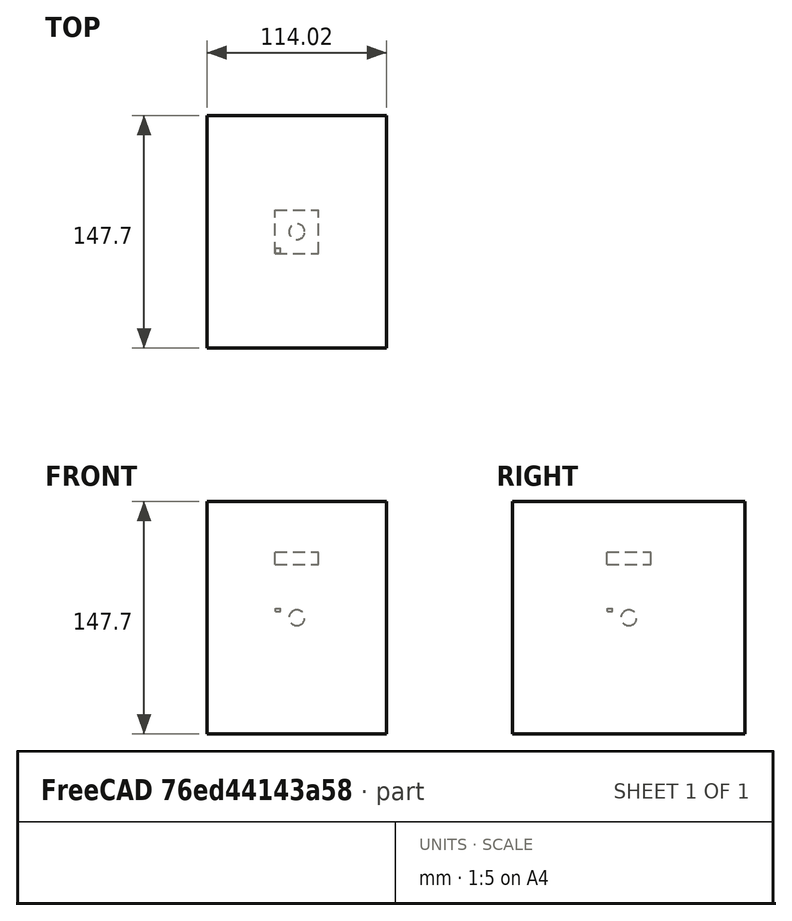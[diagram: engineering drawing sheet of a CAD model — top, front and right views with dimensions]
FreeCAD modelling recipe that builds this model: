
FCSTD DOCUMENT  (FreeCAD 0.20R29177 (Git))
Label: borderTest-1
License: All rights reserved
objects: App::DocumentObjectGroupPython×1272, Part::FeaturePython×7, App::Part×4, App::FeaturePython×1
note: 4 computed .brp shape members not serialized (recipe doc carries the construction recipe); baked Part::Feature solids carry a one-line shape summary decoded from their .brp

FEATURE [App::DocumentObjectGroupPython] HALFPI  # scripted group (container) (typed FeaturePython)
  name = HALFPI
  value = pi/2.
FEATURE [App::DocumentObjectGroupPython] PI  # scripted group (container) (typed FeaturePython)
  name = PI
  value = 1.*pi
FEATURE [App::DocumentObjectGroupPython] TWOPI  # scripted group (container) (typed FeaturePython)
  name = TWOPI
  value = 2.*pi
FEATURE [App::DocumentObjectGroupPython] Constants  # scripted group (container) (typed FeaturePython)
  Group = -> [HALFPI,PI,TWOPI]
FEATURE [App::DocumentObjectGroupPython] Variables  # scripted group (container) (typed FeaturePython)
FEATURE [App::DocumentObjectGroupPython] Quantities  # scripted group (container) (typed FeaturePython)
FEATURE [App::DocumentObjectGroupPython] Isotopes  # scripted group (container) (typed FeaturePython)
FEATURE [App::DocumentObjectGroupPython] Elements  # scripted group (container) (typed FeaturePython)
FEATURE [App::DocumentObjectGroupPython] G4_AIR  label="G4_AIR : 1.000"  # scripted group (container) (typed FeaturePython)
  n = 1
FEATURE [App::DocumentObjectGroupPython] Air  # scripted group (container) (typed FeaturePython)
  Dunit = mg/cm3
  Dvalue = 1.29
  Group = -> [G4_AIR]
  RINDEX = AirRINDEX
  conduct = 2
  density = 1
  expand = 3
  name = Air
  specific = 4
FEATURE [App::DocumentObjectGroupPython] SY  # scripted group (container) (typed FeaturePython)
  coldim = 1
  values = 100000/MeV
FEATURE [App::DocumentObjectGroupPython] RS  # scripted group (container) (typed FeaturePython)
  coldim = 1
  values = 1
FEATURE [App::DocumentObjectGroupPython] FTC  # scripted group (container) (typed FeaturePython)
  coldim = 1
  values = 21.5*ns
FEATURE [App::DocumentObjectGroupPython] STC  # scripted group (container) (typed FeaturePython)
  coldim = 1
  values = 43.8*ns
FEATURE [App::DocumentObjectGroupPython] RY1  # scripted group (container) (typed FeaturePython)
  coldim = 1
  values = 95
FEATURE [App::DocumentObjectGroupPython] RY2  # scripted group (container) (typed FeaturePython)
  coldim = 1
  values = 5
FEATURE [App::DocumentObjectGroupPython] YR  # scripted group (container) (typed FeaturePython)
  coldim = 1
  values = 0.8
FEATURE [App::DocumentObjectGroupPython] SCINTLAR  # scripted group (container) (typed FeaturePython)
  coldim = 2
  values = <blob: 2358 chars omitted>
FEATURE [App::DocumentObjectGroupPython] RINDEXLAR  # scripted group (container) (typed FeaturePython)
  coldim = 2
  values = <blob: 9384 chars omitted>
FEATURE [App::DocumentObjectGroupPython] ABSLENGTHLAR  # scripted group (container) (typed FeaturePython)
  coldim = 2
  values = 7.74901*eV 10.0*m 7.77525*eV 10.0*m 7.80167*eV 10.0*m 7.82827*eV 10.0*m 7.85506*eV 10.0*m 7.88202*eV 10.0*m 7.90917*eV 10.0*m 7.93651*eV 10.0*m 7.96404*eV 10.0*m 7.99176*eV 10.0*m 8.01968*eV 10.0*m 8.04779*eV 10.0*m 8.07609*eV 10.0*m 8.1046*eV 10.0*m 8.13331*eV 10.0*m 8.16222*eV 10.0*m 8.19134*eV 10.0*m 8.22067*eV 10.0*m 8.25021*eV 10.0*m 8.27996*eV 10.0*m 8.30993*eV 10.0*m 8.34012*eV 10.0*m 8.37052*eV 10.0*m 8.40115*eV 10.0*m 8.432*eV 10.0*m 8.46308*eV 10.0*m 8.4944*eV 10.0*m 8.52594*eV 10.0*m 8.55772*eV 10.0*m 8.58973*eV 10.0*m 8.62199*eV 10.0*m 8.65449*eV 10.0*m 8.68723*eV 10.0*m 8.72023*eV 10.0*m 8.75347*eV 10.0*m 8.78697*eV 10.0*m 8.82073*eV 10.0*m 8.85475*eV 10.0*m 8.88903*eV 10.0*m 8.92358*eV 10.0*m 8.9584*eV 10.0*m 8.99349*eV 10.0*m 9.02885*eV 10.0*m 9.0645*eV 10.0*m 9.10043*eV 10.0*m 9.13664*eV 10.0*m 9.17314*eV 10.0*m 9.20994*eV 10.0*m 9.24703*eV 10.0*m 9.28442*eV 10.0*m 9.32212*eV 10.0*m 9.36012*eV 10.0*m 9.39844*eV 10.0*m 9.43707*eV 10.0*m 9.47602*eV 10.0*m 9.51529*eV 10.0*m 9.55489*eV 10.0*m 9.59481*eV 10.0*m 9.63508*eV 10.0*m 9.67568*eV 10.0*m 9.71663*eV 10.0*m 9.75792*eV 10.0*m 9.79957*eV 10.0*m 9.84158*eV 10.0*m 9.88394*eV 10.0*m 9.92668*eV 10.0*m 9.96978*eV 10.0*m 10.0133*eV 10.0*m 10.0571*eV 10.0*m 10.1014*eV 10.0*m 10.146*eV 10.0*m 10.191*eV 10.0*m 10.2365*eV 10.0*m 10.2823*eV 10.0*m 10.3286*eV 10.0*m 10.3752*eV 10.0*m 10.4223*eV 10.0*m 10.4699*eV 10.0*m 10.5178*eV 10.0*m 10.5662*eV 10.0*m 10.6151*eV 10.0*m 10.6644*eV 10.0*m 10.7142*eV 10.0*m 10.7644*eV 10.0*m 10.8151*eV 10.0*m 10.8663*eV 10.0*m 10.9179*eV 10.0*m 10.9701*eV 10.0*m 11.0228*eV 10.0*m 11.076*eV 10.0*m 11.1296*eV 10.0*m 11.1839*eV 10.0*m 11.2386*eV 10.0*m 11.2939*eV 10.0*m 11.3497*eV 10.0*m 11.4061*eV 10.0*m 11.463*eV 10.0*m 11.5206*eV 10.0*m 11.5787*eV 10.0*m 11.6373*eV 10.0*m
FEATURE [App::DocumentObjectGroupPython] RAYLEIGHLAR  # scripted group (container) (typed FeaturePython)
  coldim = 2
  values = 7.74901*eV 90.0*cm 7.77525*eV 90.0*cm 7.80167*eV 90.0*cm 7.82827*eV 90.0*cm 7.85506*eV 90.0*cm 7.88202*eV 90.0*cm 7.90917*eV 90.0*cm 7.93651*eV 90.0*cm 7.96404*eV 90.0*cm 7.99176*eV 90.0*cm 8.01968*eV 90.0*cm 8.04779*eV 90.0*cm 8.07609*eV 90.0*cm 8.1046*eV 90.0*cm 8.13331*eV 90.0*cm 8.16222*eV 90.0*cm 8.19134*eV 90.0*cm 8.22067*eV 90.0*cm 8.25021*eV 90.0*cm 8.27996*eV 90.0*cm 8.30993*eV 90.0*cm 8.34012*eV 90.0*cm 8.37052*eV 90.0*cm 8.40115*eV 90.0*cm 8.432*eV 90.0*cm 8.46308*eV 90.0*cm 8.4944*eV 90.0*cm 8.52594*eV 90.0*cm 8.55772*eV 90.0*cm 8.58973*eV 90.0*cm 8.62199*eV 90.0*cm 8.65449*eV 90.0*cm 8.68723*eV 90.0*cm 8.72023*eV 90.0*cm 8.75347*eV 90.0*cm 8.78697*eV 90.0*cm 8.82073*eV 90.0*cm 8.85475*eV 90.0*cm 8.88903*eV 90.0*cm 8.92358*eV 90.0*cm 8.9584*eV 90.0*cm 8.99349*eV 90.0*cm 9.02885*eV 90.0*cm 9.0645*eV 90.0*cm 9.10043*eV 90.0*cm 9.13664*eV 90.0*cm 9.17314*eV 90.0*cm 9.20994*eV 90.0*cm 9.24703*eV 90.0*cm 9.28442*eV 90.0*cm 9.32212*eV 90.0*cm 9.36012*eV 90.0*cm 9.39844*eV 90.0*cm 9.43707*eV 90.0*cm 9.47602*eV 90.0*cm 9.51529*eV 90.0*cm 9.55489*eV 90.0*cm 9.59481*eV 90.0*cm 9.63508*eV 90.0*cm 9.67568*eV 90.0*cm 9.71663*eV 90.0*cm 9.75792*eV 90.0*cm 9.79957*eV 90.0*cm 9.84158*eV 90.0*cm 9.88394*eV 90.0*cm 9.92668*eV 90.0*cm 9.96978*eV 90.0*cm 10.0133*eV 90.0*cm 10.0571*eV 90.0*cm 10.1014*eV 90.0*cm 10.146*eV 90.0*cm 10.191*eV 90.0*cm 10.2365*eV 90.0*cm 10.2823*eV 90.0*cm 10.3286*eV 90.0*cm 10.3752*eV 90.0*cm 10.4223*eV 90.0*cm 10.4699*eV 90.0*cm 10.5178*eV 90.0*cm 10.5662*eV 90.0*cm 10.6151*eV 90.0*cm 10.6644*eV 90.0*cm 10.7142*eV 90.0*cm 10.7644*eV 90.0*cm 10.8151*eV 90.0*cm 10.8663*eV 90.0*cm 10.9179*eV 90.0*cm 10.9701*eV 90.0*cm 11.0228*eV 90.0*cm 11.076*eV 90.0*cm 11.1296*eV 90.0*cm 11.1839*eV 90.0*cm 11.2386*eV 90.0*cm 11.2939*eV 90.0*cm 11.3497*eV 90.0*cm 11.4061*eV 90.0*cm 11.463*eV 90.0*cm 11.5206*eV 90.0*cm 11.5787*eV 90.0*cm 11.6373*eV 90.0*cm
FEATURE [App::DocumentObjectGroupPython] REFLECTIVITY  # scripted group (container) (typed FeaturePython)
  coldim = 2
  values = 2.034*eV 0.98 2.068*eV 0.98 2.103*eV 0.98 2.139*eV 0.98 2.177*eV 0.98 2.216*eV 0.98 2.256*eV 0.98 2.298*eV 0.98 2.341*eV 0.98 2.386*eV 0.98 2.433*eV 0.98 2.481*eV 0.98 2.532*eV 0.98 2.585*eV 0.98 2.64*eV 0.98 2.697*eV 0.98 2.757*eV 0.98 2.82*eV 0.98 2.885*eV 0.98 2.954*eV 0.98 3.026*eV 0.98 3.102*eV 0.98 3.181*eV 0.98 3.265*eV 0.98 3.353*eV 0.98 3.446*eV 0.98 3.545*eV 0.98 3.649*eV 0.98 3.76*eV 0.98 3.877*eV 0.98 4.002*eV 0.98 4.136*eV 0.98 5.0*eV 0.98 6.0*eV 0.98 7.0*eV 0.98 8.0*eV 0.98 9.0*eV 0.98 9.0*eV 0.98 10.0*eV 0.98 11.0*eV 0.98 11.6*eV 0.98
FEATURE [App::DocumentObjectGroupPython] EFFICIENCY  # scripted group (container) (typed FeaturePython)
  coldim = 2
  values = 2.034*eV 1 2.068*eV 1 2.103*eV 1 2.139*eV 1 2.177*eV 1 2.216*eV 1 2.256*eV 1 2.298*eV 1 2.341*eV 1 2.386*eV 1 2.433*eV 1 2.481*eV 1 2.532*eV 1 2.585*eV 1 2.64*eV 1 2.697*eV 1 2.757*eV 1 2.82*eV 1 2.885*eV 1 2.954*eV 1 3.026*eV 1 3.102*eV 1 3.181*eV  1 3.265*eV 1 3.353*eV 1 3.446*eV 1 3.545*eV 1 3.649*eV 1 3.76*eV 1 3.877*eV 1 4.002*eV 1 4.136*eV 1 5.0*eV 1 6.0*eV 1 7.0*eV 1 8.0*eV 1 9.0*eV 1 9.0*eV 1 10.0*eV 1 11.0*eV 1 11.6*eV 1
FEATURE [App::DocumentObjectGroupPython] AirRINDEX  # scripted group (container) (typed FeaturePython)
  coldim = 2
  values = 2.034*eV 1 2.068*eV 1 2.103*eV 1 2.139*eV 1 2.177*eV 1 2.216*eV 1 2.256*eV 1 2.298*eV 1 2.341*eV 1 2.386*eV 1 2.433*eV 1 2.481*eV 1 2.532*eV 1 2.585*eV 1 2.64*eV 1 2.697*eV 1 2.757*eV 1 2.82*eV 1 2.885*eV 1 2.954*eV 1 3.026*eV 1 3.102*eV 1 3.181*eV 1 3.265*eV 1 3.353*eV 1 3.446*eV 1 3.545*eV 1 3.649*eV 1 3.76*eV 1 3.877*eV 1 4.002*eV 1 4.136*eV 1 5.0*eV 1 6.0*eV 1 7.0*eV 1 8.0*eV 1 9.0*eV 1 10.0*eV 1 11.0*eV 1 11.6*eV 1
FEATURE [App::DocumentObjectGroupPython] Matrix  # scripted group (container) (typed FeaturePython)
  Group = -> [SY,RS,FTC,STC,RY1,RY2,YR,SCINTLAR,RINDEXLAR,ABSLENGTHLAR,RAYLEIGHLAR,REFLECTIVITY,EFFICIENCY,AirRINDEX]
FEATURE [App::DocumentObjectGroupPython] ScintWrap  # scripted group (container) (typed FeaturePython)
  EFFICIENCY = EFFICIENCY
  REFLECTIVITY = REFLECTIVITY
  finish = 39
  model = 0
  type = 2
  value = 1
FEATURE [App::DocumentObjectGroupPython] Surfaces  # scripted group (container) (typed FeaturePython)
  Group = -> [ScintWrap]
FEATURE [App::DocumentObjectGroupPython] Opticals  # scripted group (container) (typed FeaturePython)
  Group = -> [Matrix,Surfaces]
FEATURE [App::DocumentObjectGroupPython] G4Isotopes  # scripted group (container) (typed FeaturePython)
FEATURE [App::DocumentObjectGroupPython] H_element  # scripted group (container) (typed FeaturePython)
  Z = 1
  atom_value = 1.008
  formula = H
  name = H_element
FEATURE [App::DocumentObjectGroupPython] He_element  # scripted group (container) (typed FeaturePython)
  Z = 2
  atom_value = 4.0026
  formula = He
  name = He_element
FEATURE [App::DocumentObjectGroupPython] Li_element  # scripted group (container) (typed FeaturePython)
  Z = 3
  atom_value = 6.94
  formula = Li
  name = Li_element
FEATURE [App::DocumentObjectGroupPython] Be_element  # scripted group (container) (typed FeaturePython)
  Z = 4
  atom_value = 9.01218
  formula = Be
  name = Be_element
FEATURE [App::DocumentObjectGroupPython] B_element  # scripted group (container) (typed FeaturePython)
  Z = 5
  atom_value = 10.81
  formula = B
  name = B_element
FEATURE [App::DocumentObjectGroupPython] C_element  # scripted group (container) (typed FeaturePython)
  Z = 6
  atom_value = 12.011
  formula = C
  name = C_element
FEATURE [App::DocumentObjectGroupPython] N_element  # scripted group (container) (typed FeaturePython)
  Z = 7
  atom_value = 14.007
  formula = N
  name = N_element
FEATURE [App::DocumentObjectGroupPython] O_element  # scripted group (container) (typed FeaturePython)
  Z = 8
  atom_value = 15.999
  formula = O
  name = O_element
FEATURE [App::DocumentObjectGroupPython] F_element  # scripted group (container) (typed FeaturePython)
  Z = 9
  atom_value = 18.9984
  formula = F
  name = F_element
FEATURE [App::DocumentObjectGroupPython] Ne_element  # scripted group (container) (typed FeaturePython)
  Z = 10
  atom_value = 20.1797
  formula = Ne
  name = Ne_element
FEATURE [App::DocumentObjectGroupPython] Na_element  # scripted group (container) (typed FeaturePython)
  Z = 11
  atom_value = 22.9898
  formula = Na
  name = Na_element
FEATURE [App::DocumentObjectGroupPython] Mg_element  # scripted group (container) (typed FeaturePython)
  Z = 12
  atom_value = 24.305
  formula = Mg
  name = Mg_element
FEATURE [App::DocumentObjectGroupPython] Al_element  # scripted group (container) (typed FeaturePython)
  Z = 13
  atom_value = 26.9815
  formula = Al
  name = Al_element
FEATURE [App::DocumentObjectGroupPython] Si_element  # scripted group (container) (typed FeaturePython)
  Z = 14
  atom_value = 28.085
  formula = Si
  name = Si_element
FEATURE [App::DocumentObjectGroupPython] P_element  # scripted group (container) (typed FeaturePython)
  Z = 15
  atom_value = 30.9738
  formula = P
  name = P_element
FEATURE [App::DocumentObjectGroupPython] S_element  # scripted group (container) (typed FeaturePython)
  Z = 16
  atom_value = 32.06
  formula = S
  name = S_element
FEATURE [App::DocumentObjectGroupPython] Cl_element  # scripted group (container) (typed FeaturePython)
  Z = 17
  atom_value = 35.45
  formula = Cl
  name = Cl_element
FEATURE [App::DocumentObjectGroupPython] Ar_element  # scripted group (container) (typed FeaturePython)
  Z = 18
  atom_value = 39.95
  formula = Ar
  name = Ar_element
FEATURE [App::DocumentObjectGroupPython] K_element  # scripted group (container) (typed FeaturePython)
  Z = 19
  atom_value = 39.0983
  formula = K
  name = K_element
FEATURE [App::DocumentObjectGroupPython] Ca_element  # scripted group (container) (typed FeaturePython)
  Z = 20
  atom_value = 40.078
  formula = Ca
  name = Ca_element
FEATURE [App::DocumentObjectGroupPython] Sc_element  # scripted group (container) (typed FeaturePython)
  Z = 21
  atom_value = 44.9559
  formula = Sc
  name = Sc_element
FEATURE [App::DocumentObjectGroupPython] Ti_element  # scripted group (container) (typed FeaturePython)
  Z = 22
  atom_value = 47.867
  formula = Ti
  name = Ti_element
FEATURE [App::DocumentObjectGroupPython] V_element  # scripted group (container) (typed FeaturePython)
  Z = 23
  atom_value = 50.9415
  formula = V
  name = V_element
FEATURE [App::DocumentObjectGroupPython] Cr_element  # scripted group (container) (typed FeaturePython)
  Z = 24
  atom_value = 51.9961
  formula = Cr
  name = Cr_element
FEATURE [App::DocumentObjectGroupPython] Mn_element  # scripted group (container) (typed FeaturePython)
  Z = 25
  atom_value = 54.938
  formula = Mn
  name = Mn_element
FEATURE [App::DocumentObjectGroupPython] Fe_element  # scripted group (container) (typed FeaturePython)
  Z = 26
  atom_value = 55.845
  formula = Fe
  name = Fe_element
FEATURE [App::DocumentObjectGroupPython] Co_element  # scripted group (container) (typed FeaturePython)
  Z = 27
  atom_value = 58.9332
  formula = Co
  name = Co_element
FEATURE [App::DocumentObjectGroupPython] Ni_element  # scripted group (container) (typed FeaturePython)
  Z = 28
  atom_value = 58.6934
  formula = Ni
  name = Ni_element
FEATURE [App::DocumentObjectGroupPython] Cu_element  # scripted group (container) (typed FeaturePython)
  Z = 29
  atom_value = 63.546
  formula = Cu
  name = Cu_element
FEATURE [App::DocumentObjectGroupPython] Zn_element  # scripted group (container) (typed FeaturePython)
  Z = 30
  atom_value = 65.38
  formula = Zn
  name = Zn_element
FEATURE [App::DocumentObjectGroupPython] Ga_element  # scripted group (container) (typed FeaturePython)
  Z = 31
  atom_value = 69.723
  formula = Ga
  name = Ga_element
FEATURE [App::DocumentObjectGroupPython] Ge_element  # scripted group (container) (typed FeaturePython)
  Z = 32
  atom_value = 72.63
  formula = Ge
  name = Ge_element
FEATURE [App::DocumentObjectGroupPython] As_element  # scripted group (container) (typed FeaturePython)
  Z = 33
  atom_value = 74.9216
  formula = As
  name = As_element
FEATURE [App::DocumentObjectGroupPython] Se_element  # scripted group (container) (typed FeaturePython)
  Z = 34
  atom_value = 78.971
  formula = Se
  name = Se_element
FEATURE [App::DocumentObjectGroupPython] Br_element  # scripted group (container) (typed FeaturePython)
  Z = 35
  atom_value = 79.904
  formula = Br
  name = Br_element
FEATURE [App::DocumentObjectGroupPython] Kr_element  # scripted group (container) (typed FeaturePython)
  Z = 36
  atom_value = 83.798
  formula = Kr
  name = Kr_element
FEATURE [App::DocumentObjectGroupPython] Rb_element  # scripted group (container) (typed FeaturePython)
  Z = 37
  atom_value = 85.4678
  formula = Rb
  name = Rb_element
FEATURE [App::DocumentObjectGroupPython] Sr_element  # scripted group (container) (typed FeaturePython)
  Z = 38
  atom_value = 87.62
  formula = Sr
  name = Sr_element
FEATURE [App::DocumentObjectGroupPython] Y_element  # scripted group (container) (typed FeaturePython)
  Z = 39
  atom_value = 88.9058
  formula = Y
  name = Y_element
FEATURE [App::DocumentObjectGroupPython] Zr_element  # scripted group (container) (typed FeaturePython)
  Z = 40
  atom_value = 91.224
  formula = Zr
  name = Zr_element
FEATURE [App::DocumentObjectGroupPython] Nb_element  # scripted group (container) (typed FeaturePython)
  Z = 41
  atom_value = 92.9064
  formula = Nb
  name = Nb_element
FEATURE [App::DocumentObjectGroupPython] Mo_element  # scripted group (container) (typed FeaturePython)
  Z = 42
  atom_value = 95.95
  formula = Mo
  name = Mo_element
FEATURE [App::DocumentObjectGroupPython] Tc_element  # scripted group (container) (typed FeaturePython)
  Z = 43
  atom_value = 97
  formula = Tc
  name = Tc_element
FEATURE [App::DocumentObjectGroupPython] Ru_element  # scripted group (container) (typed FeaturePython)
  Z = 44
  atom_value = 101.07
  formula = Ru
  name = Ru_element
FEATURE [App::DocumentObjectGroupPython] Rh_element  # scripted group (container) (typed FeaturePython)
  Z = 45
  atom_value = 102.905
  formula = Rh
  name = Rh_element
FEATURE [App::DocumentObjectGroupPython] Pd_element  # scripted group (container) (typed FeaturePython)
  Z = 46
  atom_value = 106.42
  formula = Pd
  name = Pd_element
FEATURE [App::DocumentObjectGroupPython] Ag_element  # scripted group (container) (typed FeaturePython)
  Z = 47
  atom_value = 107.868
  formula = Ag
  name = Ag_element
FEATURE [App::DocumentObjectGroupPython] Cd_element  # scripted group (container) (typed FeaturePython)
  Z = 48
  atom_value = 112.414
  formula = Cd
  name = Cd_element
FEATURE [App::DocumentObjectGroupPython] In_element  # scripted group (container) (typed FeaturePython)
  Z = 49
  atom_value = 114.818
  formula = In
  name = In_element
FEATURE [App::DocumentObjectGroupPython] Sn_element  # scripted group (container) (typed FeaturePython)
  Z = 50
  atom_value = 118.71
  formula = Sn
  name = Sn_element
FEATURE [App::DocumentObjectGroupPython] Sb_element  # scripted group (container) (typed FeaturePython)
  Z = 51
  atom_value = 121.76
  formula = Sb
  name = Sb_element
FEATURE [App::DocumentObjectGroupPython] Te_element  # scripted group (container) (typed FeaturePython)
  Z = 52
  atom_value = 127.6
  formula = Te
  name = Te_element
FEATURE [App::DocumentObjectGroupPython] I_element  # scripted group (container) (typed FeaturePython)
  Z = 53
  atom_value = 126.904
  formula = I
  name = I_element
FEATURE [App::DocumentObjectGroupPython] Xe_element  # scripted group (container) (typed FeaturePython)
  Z = 54
  atom_value = 131.293
  formula = Xe
  name = Xe_element
FEATURE [App::DocumentObjectGroupPython] Cs_element  # scripted group (container) (typed FeaturePython)
  Z = 55
  atom_value = 132.905
  formula = Cs
  name = Cs_element
FEATURE [App::DocumentObjectGroupPython] Ba_element  # scripted group (container) (typed FeaturePython)
  Z = 56
  atom_value = 137.327
  formula = Ba
  name = Ba_element
FEATURE [App::DocumentObjectGroupPython] La_element  # scripted group (container) (typed FeaturePython)
  Z = 57
  atom_value = 138.905
  formula = La
  name = La_element
FEATURE [App::DocumentObjectGroupPython] Ce_element  # scripted group (container) (typed FeaturePython)
  Z = 58
  atom_value = 140.116
  formula = Ce
  name = Ce_element
FEATURE [App::DocumentObjectGroupPython] Pr_element  # scripted group (container) (typed FeaturePython)
  Z = 59
  atom_value = 140.908
  formula = Pr
  name = Pr_element
FEATURE [App::DocumentObjectGroupPython] Nd_element  # scripted group (container) (typed FeaturePython)
  Z = 60
  atom_value = 144.242
  formula = Nd
  name = Nd_element
FEATURE [App::DocumentObjectGroupPython] Pm_element  # scripted group (container) (typed FeaturePython)
  Z = 61
  atom_value = 145
  formula = Pm
  name = Pm_element
FEATURE [App::DocumentObjectGroupPython] Sm_element  # scripted group (container) (typed FeaturePython)
  Z = 62
  atom_value = 150.36
  formula = Sm
  name = Sm_element
FEATURE [App::DocumentObjectGroupPython] Eu_element  # scripted group (container) (typed FeaturePython)
  Z = 63
  atom_value = 151.964
  formula = Eu
  name = Eu_element
FEATURE [App::DocumentObjectGroupPython] Gd_element  # scripted group (container) (typed FeaturePython)
  Z = 64
  atom_value = 157.25
  formula = Gd
  name = Gd_element
FEATURE [App::DocumentObjectGroupPython] Tb_element  # scripted group (container) (typed FeaturePython)
  Z = 65
  atom_value = 158.925
  formula = Tb
  name = Tb_element
FEATURE [App::DocumentObjectGroupPython] Dy_element  # scripted group (container) (typed FeaturePython)
  Z = 66
  atom_value = 162.5
  formula = Dy
  name = Dy_element
FEATURE [App::DocumentObjectGroupPython] Ho_element  # scripted group (container) (typed FeaturePython)
  Z = 67
  atom_value = 164.93
  formula = Ho
  name = Ho_element
FEATURE [App::DocumentObjectGroupPython] Er_element  # scripted group (container) (typed FeaturePython)
  Z = 68
  atom_value = 167.259
  formula = Er
  name = Er_element
FEATURE [App::DocumentObjectGroupPython] Tm_element  # scripted group (container) (typed FeaturePython)
  Z = 69
  atom_value = 168.934
  formula = Tm
  name = Tm_element
FEATURE [App::DocumentObjectGroupPython] Yb_element  # scripted group (container) (typed FeaturePython)
  Z = 70
  atom_value = 173.045
  formula = Yb
  name = Yb_element
FEATURE [App::DocumentObjectGroupPython] Lu_element  # scripted group (container) (typed FeaturePython)
  Z = 71
  atom_value = 174.967
  formula = Lu
  name = Lu_element
FEATURE [App::DocumentObjectGroupPython] Hf_element  # scripted group (container) (typed FeaturePython)
  Z = 72
  atom_value = 178.49
  formula = Hf
  name = Hf_element
FEATURE [App::DocumentObjectGroupPython] Ta_element  # scripted group (container) (typed FeaturePython)
  Z = 73
  atom_value = 180.948
  formula = Ta
  name = Ta_element
FEATURE [App::DocumentObjectGroupPython] W_element  # scripted group (container) (typed FeaturePython)
  Z = 74
  atom_value = 183.84
  formula = W
  name = W_element
FEATURE [App::DocumentObjectGroupPython] Re_element  # scripted group (container) (typed FeaturePython)
  Z = 75
  atom_value = 186.207
  formula = Re
  name = Re_element
FEATURE [App::DocumentObjectGroupPython] Os_element  # scripted group (container) (typed FeaturePython)
  Z = 76
  atom_value = 190.23
  formula = Os
  name = Os_element
FEATURE [App::DocumentObjectGroupPython] Ir_element  # scripted group (container) (typed FeaturePython)
  Z = 77
  atom_value = 192.217
  formula = Ir
  name = Ir_element
FEATURE [App::DocumentObjectGroupPython] Pt_element  # scripted group (container) (typed FeaturePython)
  Z = 78
  atom_value = 195.084
  formula = Pt
  name = Pt_element
FEATURE [App::DocumentObjectGroupPython] Au_element  # scripted group (container) (typed FeaturePython)
  Z = 79
  atom_value = 196.967
  formula = Au
  name = Au_element
FEATURE [App::DocumentObjectGroupPython] Hg_element  # scripted group (container) (typed FeaturePython)
  Z = 80
  atom_value = 200.592
  formula = Hg
  name = Hg_element
FEATURE [App::DocumentObjectGroupPython] Tl_element  # scripted group (container) (typed FeaturePython)
  Z = 81
  atom_value = 204.38
  formula = Tl
  name = Tl_element
FEATURE [App::DocumentObjectGroupPython] Pb_element  # scripted group (container) (typed FeaturePython)
  Z = 82
  atom_value = 207.2
  formula = Pb
  name = Pb_element
FEATURE [App::DocumentObjectGroupPython] Bi_element  # scripted group (container) (typed FeaturePython)
  Z = 83
  atom_value = 208.98
  formula = Bi
  name = Bi_element
FEATURE [App::DocumentObjectGroupPython] Po_element  # scripted group (container) (typed FeaturePython)
  Z = 84
  atom_value = 209
  formula = Po
  name = Po_element
FEATURE [App::DocumentObjectGroupPython] At_element  # scripted group (container) (typed FeaturePython)
  Z = 85
  atom_value = 210
  formula = At
  name = At_element
FEATURE [App::DocumentObjectGroupPython] Rn_element  # scripted group (container) (typed FeaturePython)
  Z = 86
  atom_value = 222
  formula = Rn
  name = Rn_element
FEATURE [App::DocumentObjectGroupPython] Fr_element  # scripted group (container) (typed FeaturePython)
  Z = 87
  atom_value = 223
  formula = Fr
  name = Fr_element
FEATURE [App::DocumentObjectGroupPython] Ra_element  # scripted group (container) (typed FeaturePython)
  Z = 88
  atom_value = 226
  formula = Ra
  name = Ra_element
FEATURE [App::DocumentObjectGroupPython] Ac_element  # scripted group (container) (typed FeaturePython)
  Z = 89
  atom_value = 227
  formula = Ac
  name = Ac_element
FEATURE [App::DocumentObjectGroupPython] Th_element  # scripted group (container) (typed FeaturePython)
  Z = 90
  atom_value = 232.038
  formula = Th
  name = Th_element
FEATURE [App::DocumentObjectGroupPython] Pa_element  # scripted group (container) (typed FeaturePython)
  Z = 91
  atom_value = 231.036
  formula = Pa
  name = Pa_element
FEATURE [App::DocumentObjectGroupPython] U_element  # scripted group (container) (typed FeaturePython)
  Z = 92
  atom_value = 238.029
  formula = U
  name = U_element
FEATURE [App::DocumentObjectGroupPython] Np_element  # scripted group (container) (typed FeaturePython)
  Z = 93
  atom_value = 237
  formula = Np
  name = Np_element
FEATURE [App::DocumentObjectGroupPython] Pu_element  # scripted group (container) (typed FeaturePython)
  Z = 94
  atom_value = 244
  formula = Pu
  name = Pu_element
FEATURE [App::DocumentObjectGroupPython] Am_element  # scripted group (container) (typed FeaturePython)
  Z = 95
  atom_value = 243
  formula = Am
  name = Am_element
FEATURE [App::DocumentObjectGroupPython] Cm_element  # scripted group (container) (typed FeaturePython)
  Z = 96
  atom_value = 247
  formula = Cm
  name = Cm_element
FEATURE [App::DocumentObjectGroupPython] Bk_element  # scripted group (container) (typed FeaturePython)
  Z = 97
  atom_value = 247
  formula = Bk
  name = Bk_element
FEATURE [App::DocumentObjectGroupPython] Cf_element  # scripted group (container) (typed FeaturePython)
  Z = 98
  atom_value = 251
  formula = Cf
  name = Cf_element
FEATURE [App::DocumentObjectGroupPython] G4Elements  # scripted group (container) (typed FeaturePython)
  Group = -> [H_element,He_element,Li_element,Be_element,B_element,C_element,N_element,O_element,F_element,Ne_element,Na_element,Mg_element,Al_element,Si_element,P_element,S_element,Cl_element,Ar_element,K_element,Ca_element,Sc_element,Ti_element,V_element,Cr_element,Mn_element,Fe_element,Co_element,Ni_element,Cu_element,Zn_element,Ga_element,Ge_element,As_element,Se_element,Br_element,Kr_element,Rb_element,+61 more]
FEATURE [App::DocumentObjectGroupPython] H_element001  label="H_element : 0.101"  # scripted group (container) (typed FeaturePython)
  n = 0.101327
FEATURE [App::DocumentObjectGroupPython] C_element001  label="C_element : 0.775"  # scripted group (container) (typed FeaturePython)
  n = 0.7755
FEATURE [App::DocumentObjectGroupPython] N_element001  label="N_element : 0.035"  # scripted group (container) (typed FeaturePython)
  n = 0.035057
FEATURE [App::DocumentObjectGroupPython] O_element001  label="O_element : 0.052"  # scripted group (container) (typed FeaturePython)
  n = 0.0523159
FEATURE [App::DocumentObjectGroupPython] F_element001  label="F_element : 0.017"  # scripted group (container) (typed FeaturePython)
  n = 0.017422
FEATURE [App::DocumentObjectGroupPython] Ca_element001  label="Ca_element : 0.018"  # scripted group (container) (typed FeaturePython)
  n = 0.018378
FEATURE [App::DocumentObjectGroupPython] G4_A_150_TISSUE  label="G4_A-150_TISSUE"  # scripted group (container) (typed FeaturePython)
  Dunit = g/cm3
  Dvalue = 1.127
  Group = -> [H_element001,C_element001,N_element001,O_element001,F_element001,Ca_element001]
  conduct = 2
  density = 1
  expand = 3
  formula = G4_A-150_TISSUE
  name = G4_A-150_TISSUE
  specific = 4
FEATURE [App::DocumentObjectGroupPython] C_element002  label="C_element : 3"  # scripted group (container) (typed FeaturePython)
  n = 3
  ref = C_element
FEATURE [App::DocumentObjectGroupPython] H_element002  label="H_element : 6"  # scripted group (container) (typed FeaturePython)
  n = 6
  ref = H_element
FEATURE [App::DocumentObjectGroupPython] O_element002  label="O_element : 1"  # scripted group (container) (typed FeaturePython)
  n = 1
  ref = O_element
FEATURE [App::DocumentObjectGroupPython] G4_ACETONE  # scripted group (container) (typed FeaturePython)
  Dunit = g/cm3
  Dvalue = 0.7899
  Group = -> [C_element002,H_element002,O_element002]
  conduct = 2
  density = 1
  expand = 3
  formula = G4_ACETONE
  name = G4_ACETONE
  specific = 4
FEATURE [App::DocumentObjectGroupPython] C_element003  label="C_element : 2"  # scripted group (container) (typed FeaturePython)
  n = 2
  ref = C_element
FEATURE [App::DocumentObjectGroupPython] H_element003  label="H_element : 2"  # scripted group (container) (typed FeaturePython)
  n = 2
  ref = H_element
FEATURE [App::DocumentObjectGroupPython] G4_ACETYLENE  # scripted group (container) (typed FeaturePython)
  Dunit = g/cm3
  Dvalue = 0.0010967
  Group = -> [C_element003,H_element003]
  conduct = 2
  density = 1
  expand = 3
  formula = G4_ACETYLENE
  name = G4_ACETYLENE
  specific = 4
FEATURE [App::DocumentObjectGroupPython] C_element004  label="C_element : 5"  # scripted group (container) (typed FeaturePython)
  n = 5
  ref = C_element
FEATURE [App::DocumentObjectGroupPython] H_element004  label="H_element : 5"  # scripted group (container) (typed FeaturePython)
  n = 5
  ref = H_element
FEATURE [App::DocumentObjectGroupPython] N_element002  label="N_element : 5"  # scripted group (container) (typed FeaturePython)
  n = 5
  ref = N_element
FEATURE [App::DocumentObjectGroupPython] G4_ADENINE  # scripted group (container) (typed FeaturePython)
  Dunit = g/cm3
  Dvalue = 1.6
  Group = -> [C_element004,H_element004,N_element002]
  conduct = 2
  density = 1
  expand = 3
  formula = G4_ADENINE
  name = G4_ADENINE
  specific = 4
FEATURE [App::DocumentObjectGroupPython] H_element005  label="H_element : 0.114"  # scripted group (container) (typed FeaturePython)
  n = 0.114
FEATURE [App::DocumentObjectGroupPython] C_element005  label="C_element : 0.598"  # scripted group (container) (typed FeaturePython)
  n = 0.598
FEATURE [App::DocumentObjectGroupPython] N_element003  label="N_element : 0.007"  # scripted group (container) (typed FeaturePython)
  n = 0.007
FEATURE [App::DocumentObjectGroupPython] O_element003  label="O_element : 0.278"  # scripted group (container) (typed FeaturePython)
  n = 0.278
FEATURE [App::DocumentObjectGroupPython] Na_element001  label="Na_element : 0.001"  # scripted group (container) (typed FeaturePython)
  n = 0.001
FEATURE [App::DocumentObjectGroupPython] S_element001  label="S_element : 0.001"  # scripted group (container) (typed FeaturePython)
  n = 0.001
FEATURE [App::DocumentObjectGroupPython] Cl_element001  label="Cl_element : 0.001"  # scripted group (container) (typed FeaturePython)
  n = 0.001
FEATURE [App::DocumentObjectGroupPython] G4_ADIPOSE_TISSUE_ICRP  # scripted group (container) (typed FeaturePython)
  Dunit = g/cm3
  Dvalue = 0.95
  Group = -> [H_element005,C_element005,N_element003,O_element003,Na_element001,S_element001,Cl_element001]
  conduct = 2
  density = 1
  expand = 3
  formula = G4_ADIPOSE_TISSUE_ICRP
  name = G4_ADIPOSE_TISSUE_ICRP
  specific = 4
FEATURE [App::DocumentObjectGroupPython] C_element006  label="C_element : 0.000"  # scripted group (container) (typed FeaturePython)
  n = 0.000124
FEATURE [App::DocumentObjectGroupPython] N_element004  label="N_element : 0.755"  # scripted group (container) (typed FeaturePython)
  n = 0.755268
FEATURE [App::DocumentObjectGroupPython] O_element004  label="O_element : 0.232"  # scripted group (container) (typed FeaturePython)
  n = 0.231781
FEATURE [App::DocumentObjectGroupPython] Ar_element001  label="Ar_element : 0.013"  # scripted group (container) (typed FeaturePython)
  n = 0.012827
FEATURE [App::DocumentObjectGroupPython] G4_AIR001  label="G4_AIR"  # scripted group (container) (typed FeaturePython)
  Dunit = g/cm3
  Dvalue = 0.00120479
  Group = -> [C_element006,N_element004,O_element004,Ar_element001]
  conduct = 2
  density = 1
  expand = 3
  formula = G4_AIR
  name = G4_AIR
  specific = 4
FEATURE [App::DocumentObjectGroupPython] C_element007  label="C_element : 006"  # scripted group (container) (typed FeaturePython)
  n = 3
  ref = C_element
FEATURE [App::DocumentObjectGroupPython] H_element006  label="H_element : 7"  # scripted group (container) (typed FeaturePython)
  n = 7
  ref = H_element
FEATURE [App::DocumentObjectGroupPython] N_element005  label="N_element : 1"  # scripted group (container) (typed FeaturePython)
  n = 1
  ref = N_element
FEATURE [App::DocumentObjectGroupPython] O_element005  label="O_element : 2"  # scripted group (container) (typed FeaturePython)
  n = 2
  ref = O_element
FEATURE [App::DocumentObjectGroupPython] G4_ALANINE  # scripted group (container) (typed FeaturePython)
  Dunit = g/cm3
  Dvalue = 1.42
  Group = -> [C_element007,H_element006,N_element005,O_element005]
  conduct = 2
  density = 1
  expand = 3
  formula = G4_ALANINE
  name = G4_ALANINE
  specific = 4
FEATURE [App::DocumentObjectGroupPython] Al_element001  label="Al_element : 2"  # scripted group (container) (typed FeaturePython)
  n = 2
  ref = Al_element
FEATURE [App::DocumentObjectGroupPython] O_element006  label="O_element : 3"  # scripted group (container) (typed FeaturePython)
  n = 3
  ref = O_element
FEATURE [App::DocumentObjectGroupPython] G4_ALUMINUM_OXIDE  # scripted group (container) (typed FeaturePython)
  Dunit = g/cm3
  Dvalue = 3.97
  Group = -> [Al_element001,O_element006]
  conduct = 2
  density = 1
  expand = 3
  formula = G4_ALUMINUM_OXIDE
  name = G4_ALUMINUM_OXIDE
  specific = 4
FEATURE [App::DocumentObjectGroupPython] H_element007  label="H_element : 0.106"  # scripted group (container) (typed FeaturePython)
  n = 0.10593
FEATURE [App::DocumentObjectGroupPython] C_element008  label="C_element : 0.789"  # scripted group (container) (typed FeaturePython)
  n = 0.788974
FEATURE [App::DocumentObjectGroupPython] O_element007  label="O_element : 0.105"  # scripted group (container) (typed FeaturePython)
  n = 0.105096
FEATURE [App::DocumentObjectGroupPython] G4_AMBER  # scripted group (container) (typed FeaturePython)
  Dunit = g/cm3
  Dvalue = 1.1
  Group = -> [H_element007,C_element008,O_element007]
  conduct = 2
  density = 1
  expand = 3
  formula = G4_AMBER
  name = G4_AMBER
  specific = 4
FEATURE [App::DocumentObjectGroupPython] N_element006  label="N_element : 006"  # scripted group (container) (typed FeaturePython)
  n = 1
  ref = N_element
FEATURE [App::DocumentObjectGroupPython] H_element008  label="H_element : 3"  # scripted group (container) (typed FeaturePython)
  n = 3
  ref = H_element
FEATURE [App::DocumentObjectGroupPython] G4_AMMONIA  # scripted group (container) (typed FeaturePython)
  Dunit = g/cm3
  Dvalue = 0.000826019
  Group = -> [N_element006,H_element008]
  conduct = 2
  density = 1
  expand = 3
  formula = G4_AMMONIA
  name = G4_AMMONIA
  specific = 4
FEATURE [App::DocumentObjectGroupPython] C_element009  label="C_element : 6"  # scripted group (container) (typed FeaturePython)
  n = 6
  ref = C_element
FEATURE [App::DocumentObjectGroupPython] H_element009  label="H_element : 008"  # scripted group (container) (typed FeaturePython)
  n = 7
  ref = H_element
FEATURE [App::DocumentObjectGroupPython] N_element007  label="N_element : 007"  # scripted group (container) (typed FeaturePython)
  n = 1
  ref = N_element
FEATURE [App::DocumentObjectGroupPython] G4_ANILINE  # scripted group (container) (typed FeaturePython)
  Dunit = g/cm3
  Dvalue = 1.0235
  Group = -> [C_element009,H_element009,N_element007]
  conduct = 2
  density = 1
  expand = 3
  formula = G4_ANILINE
  name = G4_ANILINE
  specific = 4
FEATURE [App::DocumentObjectGroupPython] C_element010  label="C_element : 14"  # scripted group (container) (typed FeaturePython)
  n = 14
  ref = C_element
FEATURE [App::DocumentObjectGroupPython] H_element010  label="H_element : 10"  # scripted group (container) (typed FeaturePython)
  n = 10
  ref = H_element
FEATURE [App::DocumentObjectGroupPython] G4_ANTHRACENE  # scripted group (container) (typed FeaturePython)
  Dunit = g/cm3
  Dvalue = 1.283
  Group = -> [C_element010,H_element010]
  conduct = 2
  density = 1
  expand = 3
  formula = G4_ANTHRACENE
  name = G4_ANTHRACENE
  specific = 4
FEATURE [App::DocumentObjectGroupPython] H_element011  label="H_element : 0.065"  # scripted group (container) (typed FeaturePython)
  n = 0.0654709
FEATURE [App::DocumentObjectGroupPython] C_element011  label="C_element : 0.537"  # scripted group (container) (typed FeaturePython)
  n = 0.536944
FEATURE [App::DocumentObjectGroupPython] N_element008  label="N_element : 0.021"  # scripted group (container) (typed FeaturePython)
  n = 0.0215
FEATURE [App::DocumentObjectGroupPython] O_element008  label="O_element : 0.032"  # scripted group (container) (typed FeaturePython)
  n = 0.032085
FEATURE [App::DocumentObjectGroupPython] F_element002  label="F_element : 0.167"  # scripted group (container) (typed FeaturePython)
  n = 0.167411
FEATURE [App::DocumentObjectGroupPython] Ca_element002  label="Ca_element : 0.177"  # scripted group (container) (typed FeaturePython)
  n = 0.176589
FEATURE [App::DocumentObjectGroupPython] G4_B_100_BONE  label="G4_B-100_BONE"  # scripted group (container) (typed FeaturePython)
  Dunit = g/cm3
  Dvalue = 1.45
  Group = -> [H_element011,C_element011,N_element008,O_element008,F_element002,Ca_element002]
  conduct = 2
  density = 1
  expand = 3
  formula = G4_B-100_BONE
  name = G4_B-100_BONE
  specific = 4
FEATURE [App::DocumentObjectGroupPython] H_element012  label="H_element : 0.057"  # scripted group (container) (typed FeaturePython)
  n = 0.057441
FEATURE [App::DocumentObjectGroupPython] C_element012  label="C_element : 0.790"  # scripted group (container) (typed FeaturePython)
  n = 0.774591
FEATURE [App::DocumentObjectGroupPython] O_element009  label="O_element : 0.168"  # scripted group (container) (typed FeaturePython)
  n = 0.167968
FEATURE [App::DocumentObjectGroupPython] G4_BAKELITE  # scripted group (container) (typed FeaturePython)
  Dunit = g/cm3
  Dvalue = 1.25
  Group = -> [H_element012,C_element012,O_element009]
  conduct = 2
  density = 1
  expand = 3
  formula = G4_BAKELITE
  name = G4_BAKELITE
  specific = 4
FEATURE [App::DocumentObjectGroupPython] Ba_element001  label="Ba_element : 1"  # scripted group (container) (typed FeaturePython)
  n = 1
  ref = Ba_element
FEATURE [App::DocumentObjectGroupPython] F_element003  label="F_element : 2"  # scripted group (container) (typed FeaturePython)
  n = 2
  ref = F_element
FEATURE [App::DocumentObjectGroupPython] G4_BARIUM_FLUORIDE  # scripted group (container) (typed FeaturePython)
  Dunit = g/cm3
  Dvalue = 4.89
  Group = -> [Ba_element001,F_element003]
  conduct = 2
  density = 1
  expand = 3
  formula = G4_BARIUM_FLUORIDE
  name = G4_BARIUM_FLUORIDE
  specific = 4
FEATURE [App::DocumentObjectGroupPython] Ba_element002  label="Ba_element : 002"  # scripted group (container) (typed FeaturePython)
  n = 1
  ref = Ba_element
FEATURE [App::DocumentObjectGroupPython] S_element002  label="S_element : 1"  # scripted group (container) (typed FeaturePython)
  n = 1
  ref = S_element
FEATURE [App::DocumentObjectGroupPython] O_element010  label="O_element : 4"  # scripted group (container) (typed FeaturePython)
  n = 4
  ref = O_element
FEATURE [App::DocumentObjectGroupPython] G4_BARIUM_SULFATE  # scripted group (container) (typed FeaturePython)
  Dunit = g/cm3
  Dvalue = 4.5
  Group = -> [Ba_element002,S_element002,O_element010]
  conduct = 2
  density = 1
  expand = 3
  formula = G4_BARIUM_SULFATE
  name = G4_BARIUM_SULFATE
  specific = 4
FEATURE [App::DocumentObjectGroupPython] C_element013  label="C_element : 007"  # scripted group (container) (typed FeaturePython)
  n = 6
  ref = C_element
FEATURE [App::DocumentObjectGroupPython] H_element013  label="H_element : 009"  # scripted group (container) (typed FeaturePython)
  n = 6
  ref = H_element
FEATURE [App::DocumentObjectGroupPython] G4_BENZENE  # scripted group (container) (typed FeaturePython)
  Dunit = g/cm3
  Dvalue = 0.87865
  Group = -> [C_element013,H_element013]
  conduct = 2
  density = 1
  expand = 3
  formula = G4_BENZENE
  name = G4_BENZENE
  specific = 4
FEATURE [App::DocumentObjectGroupPython] Be_element001  label="Be_element : 1"  # scripted group (container) (typed FeaturePython)
  n = 1
  ref = Be_element
FEATURE [App::DocumentObjectGroupPython] O_element011  label="O_element : 005"  # scripted group (container) (typed FeaturePython)
  n = 1
  ref = O_element
FEATURE [App::DocumentObjectGroupPython] G4_BERYLLIUM_OXIDE  # scripted group (container) (typed FeaturePython)
  Dunit = g/cm3
  Dvalue = 3.01
  Group = -> [Be_element001,O_element011]
  conduct = 2
  density = 1
  expand = 3
  formula = G4_BERYLLIUM_OXIDE
  name = G4_BERYLLIUM_OXIDE
  specific = 4
FEATURE [App::DocumentObjectGroupPython] Bi_element001  label="Bi_element : 4"  # scripted group (container) (typed FeaturePython)
  n = 4
  ref = Bi_element
FEATURE [App::DocumentObjectGroupPython] Ge_element001  label="Ge_element : 3"  # scripted group (container) (typed FeaturePython)
  n = 3
  ref = Ge_element
FEATURE [App::DocumentObjectGroupPython] O_element012  label="O_element : 12"  # scripted group (container) (typed FeaturePython)
  n = 12
  ref = O_element
FEATURE [App::DocumentObjectGroupPython] G4_BGO  # scripted group (container) (typed FeaturePython)
  Dunit = g/cm3
  Dvalue = 7.13
  Group = -> [Bi_element001,Ge_element001,O_element012]
  conduct = 2
  density = 1
  expand = 3
  formula = G4_BGO
  name = G4_BGO
  specific = 4
FEATURE [App::DocumentObjectGroupPython] H_element014  label="H_element : 0.102"  # scripted group (container) (typed FeaturePython)
  n = 0.102
FEATURE [App::DocumentObjectGroupPython] C_element014  label="C_element : 0.110"  # scripted group (container) (typed FeaturePython)
  n = 0.11
FEATURE [App::DocumentObjectGroupPython] N_element009  label="N_element : 0.033"  # scripted group (container) (typed FeaturePython)
  n = 0.033
FEATURE [App::DocumentObjectGroupPython] O_element013  label="O_element : 0.745"  # scripted group (container) (typed FeaturePython)
  n = 0.745
FEATURE [App::DocumentObjectGroupPython] Na_element002  label="Na_element : 0.002"  # scripted group (container) (typed FeaturePython)
  n = 0.001
FEATURE [App::DocumentObjectGroupPython] P_element001  label="P_element : 0.001"  # scripted group (container) (typed FeaturePython)
  n = 0.001
FEATURE [App::DocumentObjectGroupPython] S_element003  label="S_element : 0.002"  # scripted group (container) (typed FeaturePython)
  n = 0.002
FEATURE [App::DocumentObjectGroupPython] Cl_element002  label="Cl_element : 0.003"  # scripted group (container) (typed FeaturePython)
  n = 0.003
FEATURE [App::DocumentObjectGroupPython] K_element001  label="K_element : 0.002"  # scripted group (container) (typed FeaturePython)
  n = 0.002
FEATURE [App::DocumentObjectGroupPython] Fe_element001  label="Fe_element : 0.001"  # scripted group (container) (typed FeaturePython)
  n = 0.001
FEATURE [App::DocumentObjectGroupPython] G4_BLOOD_ICRP  # scripted group (container) (typed FeaturePython)
  Dunit = g/cm3
  Dvalue = 1.06
  Group = -> [H_element014,C_element014,N_element009,O_element013,Na_element002,P_element001,S_element003,Cl_element002,K_element001,Fe_element001]
  conduct = 2
  density = 1
  expand = 3
  formula = G4_BLOOD_ICRP
  name = G4_BLOOD_ICRP
  specific = 4
FEATURE [App::DocumentObjectGroupPython] H_element015  label="H_element : 0.064"  # scripted group (container) (typed FeaturePython)
  n = 0.064
FEATURE [App::DocumentObjectGroupPython] C_element015  label="C_element : 0.278"  # scripted group (container) (typed FeaturePython)
  n = 0.278
FEATURE [App::DocumentObjectGroupPython] N_element010  label="N_element : 0.027"  # scripted group (container) (typed FeaturePython)
  n = 0.027
FEATURE [App::DocumentObjectGroupPython] O_element014  label="O_element : 0.410"  # scripted group (container) (typed FeaturePython)
  n = 0.41
FEATURE [App::DocumentObjectGroupPython] Mg_element001  label="Mg_element : 0.002"  # scripted group (container) (typed FeaturePython)
  n = 0.002
FEATURE [App::DocumentObjectGroupPython] P_element002  label="P_element : 0.070"  # scripted group (container) (typed FeaturePython)
  n = 0.07
FEATURE [App::DocumentObjectGroupPython] S_element004  label="S_element : 0.003"  # scripted group (container) (typed FeaturePython)
  n = 0.002
FEATURE [App::DocumentObjectGroupPython] Ca_element003  label="Ca_element : 0.147"  # scripted group (container) (typed FeaturePython)
  n = 0.147
FEATURE [App::DocumentObjectGroupPython] G4_BONE_COMPACT_ICRU  # scripted group (container) (typed FeaturePython)
  Dunit = g/cm3
  Dvalue = 1.85
  Group = -> [H_element015,C_element015,N_element010,O_element014,Mg_element001,P_element002,S_element004,Ca_element003]
  conduct = 2
  density = 1
  expand = 3
  formula = G4_BONE_COMPACT_ICRU
  name = G4_BONE_COMPACT_ICRU
  specific = 4
FEATURE [App::DocumentObjectGroupPython] H_element016  label="H_element : 0.034"  # scripted group (container) (typed FeaturePython)
  n = 0.034
FEATURE [App::DocumentObjectGroupPython] C_element016  label="C_element : 0.155"  # scripted group (container) (typed FeaturePython)
  n = 0.155
FEATURE [App::DocumentObjectGroupPython] N_element011  label="N_element : 0.042"  # scripted group (container) (typed FeaturePython)
  n = 0.042
FEATURE [App::DocumentObjectGroupPython] O_element015  label="O_element : 0.435"  # scripted group (container) (typed FeaturePython)
  n = 0.435
FEATURE [App::DocumentObjectGroupPython] Na_element003  label="Na_element : 0.003"  # scripted group (container) (typed FeaturePython)
  n = 0.001
FEATURE [App::DocumentObjectGroupPython] Mg_element002  label="Mg_element : 0.003"  # scripted group (container) (typed FeaturePython)
  n = 0.002
FEATURE [App::DocumentObjectGroupPython] P_element003  label="P_element : 0.103"  # scripted group (container) (typed FeaturePython)
  n = 0.103
FEATURE [App::DocumentObjectGroupPython] S_element005  label="S_element : 0.004"  # scripted group (container) (typed FeaturePython)
  n = 0.003
FEATURE [App::DocumentObjectGroupPython] Ca_element004  label="Ca_element : 0.225"  # scripted group (container) (typed FeaturePython)
  n = 0.225
FEATURE [App::DocumentObjectGroupPython] G4_BONE_CORTICAL_ICRP  # scripted group (container) (typed FeaturePython)
  Dunit = g/cm3
  Dvalue = 1.92
  Group = -> [H_element016,C_element016,N_element011,O_element015,Na_element003,Mg_element002,P_element003,S_element005,Ca_element004]
  conduct = 2
  density = 1
  expand = 3
  formula = G4_BONE_CORTICAL_ICRP
  name = G4_BONE_CORTICAL_ICRP
  specific = 4
FEATURE [App::DocumentObjectGroupPython] B_element001  label="B_element : 4"  # scripted group (container) (typed FeaturePython)
  n = 4
  ref = B_element
FEATURE [App::DocumentObjectGroupPython] C_element017  label="C_element : 1"  # scripted group (container) (typed FeaturePython)
  n = 1
  ref = C_element
FEATURE [App::DocumentObjectGroupPython] G4_BORON_CARBIDE  # scripted group (container) (typed FeaturePython)
  Dunit = g/cm3
  Dvalue = 2.52
  Group = -> [B_element001,C_element017]
  conduct = 2
  density = 1
  expand = 3
  formula = G4_BORON_CARBIDE
  name = G4_BORON_CARBIDE
  specific = 4
FEATURE [App::DocumentObjectGroupPython] B_element002  label="B_element : 2"  # scripted group (container) (typed FeaturePython)
  n = 2
  ref = B_element
FEATURE [App::DocumentObjectGroupPython] O_element016  label="O_element : 006"  # scripted group (container) (typed FeaturePython)
  n = 3
  ref = O_element
FEATURE [App::DocumentObjectGroupPython] G4_BORON_OXIDE  # scripted group (container) (typed FeaturePython)
  Dunit = g/cm3
  Dvalue = 1.812
  Group = -> [B_element002,O_element016]
  conduct = 2
  density = 1
  expand = 3
  formula = G4_BORON_OXIDE
  name = G4_BORON_OXIDE
  specific = 4
FEATURE [App::DocumentObjectGroupPython] H_element017  label="H_element : 0.107"  # scripted group (container) (typed FeaturePython)
  n = 0.107
FEATURE [App::DocumentObjectGroupPython] C_element018  label="C_element : 0.145"  # scripted group (container) (typed FeaturePython)
  n = 0.145
FEATURE [App::DocumentObjectGroupPython] N_element012  label="N_element : 0.022"  # scripted group (container) (typed FeaturePython)
  n = 0.022
FEATURE [App::DocumentObjectGroupPython] O_element017  label="O_element : 0.712"  # scripted group (container) (typed FeaturePython)
  n = 0.712
FEATURE [App::DocumentObjectGroupPython] Na_element004  label="Na_element : 0.004"  # scripted group (container) (typed FeaturePython)
  n = 0.002
FEATURE [App::DocumentObjectGroupPython] P_element004  label="P_element : 0.004"  # scripted group (container) (typed FeaturePython)
  n = 0.004
FEATURE [App::DocumentObjectGroupPython] S_element006  label="S_element : 0.005"  # scripted group (container) (typed FeaturePython)
  n = 0.002
FEATURE [App::DocumentObjectGroupPython] Cl_element003  label="Cl_element : 0.004"  # scripted group (container) (typed FeaturePython)
  n = 0.003
FEATURE [App::DocumentObjectGroupPython] K_element002  label="K_element : 0.003"  # scripted group (container) (typed FeaturePython)
  n = 0.003
FEATURE [App::DocumentObjectGroupPython] G4_BRAIN_ICRP  # scripted group (container) (typed FeaturePython)
  Dunit = g/cm3
  Dvalue = 1.04
  Group = -> [H_element017,C_element018,N_element012,O_element017,Na_element004,P_element004,S_element006,Cl_element003,K_element002]
  conduct = 2
  density = 1
  expand = 3
  formula = G4_BRAIN_ICRP
  name = G4_BRAIN_ICRP
  specific = 4
FEATURE [App::DocumentObjectGroupPython] C_element019  label="C_element : 4"  # scripted group (container) (typed FeaturePython)
  n = 4
  ref = C_element
FEATURE [App::DocumentObjectGroupPython] H_element018  label="H_element : 010"  # scripted group (container) (typed FeaturePython)
  n = 10
  ref = H_element
FEATURE [App::DocumentObjectGroupPython] G4_BUTANE  # scripted group (container) (typed FeaturePython)
  Dunit = g/cm3
  Dvalue = 0.00249343
  Group = -> [C_element019,H_element018]
  conduct = 2
  density = 1
  expand = 3
  formula = G4_BUTANE
  name = G4_BUTANE
  specific = 4
FEATURE [App::DocumentObjectGroupPython] C_element020  label="C_element : 008"  # scripted group (container) (typed FeaturePython)
  n = 4
  ref = C_element
FEATURE [App::DocumentObjectGroupPython] H_element019  label="H_element : 011"  # scripted group (container) (typed FeaturePython)
  n = 10
  ref = H_element
FEATURE [App::DocumentObjectGroupPython] O_element018  label="O_element : 007"  # scripted group (container) (typed FeaturePython)
  n = 1
  ref = O_element
FEATURE [App::DocumentObjectGroupPython] G4_N_BUTYL_ALCOHOL  label="G4_N-BUTYL_ALCOHOL"  # scripted group (container) (typed FeaturePython)
  Dunit = g/cm3
  Dvalue = 0.8098
  Group = -> [C_element020,H_element019,O_element018]
  conduct = 2
  density = 1
  expand = 3
  formula = G4_N-BUTYL_ALCOHOL
  name = G4_N-BUTYL_ALCOHOL
  specific = 4
FEATURE [App::DocumentObjectGroupPython] H_element020  label="H_element : 0.025"  # scripted group (container) (typed FeaturePython)
  n = 0.02468
FEATURE [App::DocumentObjectGroupPython] C_element021  label="C_element : 0.502"  # scripted group (container) (typed FeaturePython)
  n = 0.501611
FEATURE [App::DocumentObjectGroupPython] O_element019  label="O_element : 0.005"  # scripted group (container) (typed FeaturePython)
  n = 0.004527
FEATURE [App::DocumentObjectGroupPython] F_element004  label="F_element : 0.465"  # scripted group (container) (typed FeaturePython)
  n = 0.465209
FEATURE [App::DocumentObjectGroupPython] Si_element001  label="Si_element : 0.004"  # scripted group (container) (typed FeaturePython)
  n = 0.003973
FEATURE [App::DocumentObjectGroupPython] G4_C_552  label="G4_C-552"  # scripted group (container) (typed FeaturePython)
  Dunit = g/cm3
  Dvalue = 1.76
  Group = -> [H_element020,C_element021,O_element019,F_element004,Si_element001]
  conduct = 2
  density = 1
  expand = 3
  formula = G4_C-552
  name = G4_C-552
  specific = 4
FEATURE [App::DocumentObjectGroupPython] Cd_element001  label="Cd_element : 1"  # scripted group (container) (typed FeaturePython)
  n = 1
  ref = Cd_element
FEATURE [App::DocumentObjectGroupPython] Te_element001  label="Te_element : 1"  # scripted group (container) (typed FeaturePython)
  n = 1
  ref = Te_element
FEATURE [App::DocumentObjectGroupPython] G4_CADMIUM_TELLURIDE  # scripted group (container) (typed FeaturePython)
  Dunit = g/cm3
  Dvalue = 6.2
  Group = -> [Cd_element001,Te_element001]
  conduct = 2
  density = 1
  expand = 3
  formula = G4_CADMIUM_TELLURIDE
  name = G4_CADMIUM_TELLURIDE
  specific = 4
FEATURE [App::DocumentObjectGroupPython] Cd_element002  label="Cd_element : 002"  # scripted group (container) (typed FeaturePython)
  n = 1
  ref = Cd_element
FEATURE [App::DocumentObjectGroupPython] W_element001  label="W_element : 1"  # scripted group (container) (typed FeaturePython)
  n = 1
  ref = W_element
FEATURE [App::DocumentObjectGroupPython] O_element020  label="O_element : 008"  # scripted group (container) (typed FeaturePython)
  n = 4
  ref = O_element
FEATURE [App::DocumentObjectGroupPython] G4_CADMIUM_TUNGSTATE  # scripted group (container) (typed FeaturePython)
  Dunit = g/cm3
  Dvalue = 7.9
  Group = -> [Cd_element002,W_element001,O_element020]
  conduct = 2
  density = 1
  expand = 3
  formula = G4_CADMIUM_TUNGSTATE
  name = G4_CADMIUM_TUNGSTATE
  specific = 4
FEATURE [App::DocumentObjectGroupPython] Ca_element005  label="Ca_element : 1"  # scripted group (container) (typed FeaturePython)
  n = 1
  ref = Ca_element
FEATURE [App::DocumentObjectGroupPython] C_element022  label="C_element : 009"  # scripted group (container) (typed FeaturePython)
  n = 1
  ref = C_element
FEATURE [App::DocumentObjectGroupPython] O_element021  label="O_element : 009"  # scripted group (container) (typed FeaturePython)
  n = 3
  ref = O_element
FEATURE [App::DocumentObjectGroupPython] G4_CALCIUM_CARBONATE  # scripted group (container) (typed FeaturePython)
  Dunit = g/cm3
  Dvalue = 2.8
  Group = -> [Ca_element005,C_element022,O_element021]
  conduct = 2
  density = 1
  expand = 3
  formula = G4_CALCIUM_CARBONATE
  name = G4_CALCIUM_CARBONATE
  specific = 4
FEATURE [App::DocumentObjectGroupPython] Ca_element006  label="Ca_element : 002"  # scripted group (container) (typed FeaturePython)
  n = 1
  ref = Ca_element
FEATURE [App::DocumentObjectGroupPython] F_element005  label="F_element : 003"  # scripted group (container) (typed FeaturePython)
  n = 2
  ref = F_element
FEATURE [App::DocumentObjectGroupPython] G4_CALCIUM_FLUORIDE  # scripted group (container) (typed FeaturePython)
  Dunit = g/cm3
  Dvalue = 3.18
  Group = -> [Ca_element006,F_element005]
  conduct = 2
  density = 1
  expand = 3
  formula = G4_CALCIUM_FLUORIDE
  name = G4_CALCIUM_FLUORIDE
  specific = 4
FEATURE [App::DocumentObjectGroupPython] Ca_element007  label="Ca_element : 003"  # scripted group (container) (typed FeaturePython)
  n = 1
  ref = Ca_element
FEATURE [App::DocumentObjectGroupPython] O_element022  label="O_element : 010"  # scripted group (container) (typed FeaturePython)
  n = 1
  ref = O_element
FEATURE [App::DocumentObjectGroupPython] G4_CALCIUM_OXIDE  # scripted group (container) (typed FeaturePython)
  Dunit = g/cm3
  Dvalue = 3.3
  Group = -> [Ca_element007,O_element022]
  conduct = 2
  density = 1
  expand = 3
  formula = G4_CALCIUM_OXIDE
  name = G4_CALCIUM_OXIDE
  specific = 4
FEATURE [App::DocumentObjectGroupPython] Ca_element008  label="Ca_element : 004"  # scripted group (container) (typed FeaturePython)
  n = 1
  ref = Ca_element
FEATURE [App::DocumentObjectGroupPython] S_element007  label="S_element : 002"  # scripted group (container) (typed FeaturePython)
  n = 1
  ref = S_element
FEATURE [App::DocumentObjectGroupPython] O_element023  label="O_element : 011"  # scripted group (container) (typed FeaturePython)
  n = 4
  ref = O_element
FEATURE [App::DocumentObjectGroupPython] G4_CALCIUM_SULFATE  # scripted group (container) (typed FeaturePython)
  Dunit = g/cm3
  Dvalue = 2.96
  Group = -> [Ca_element008,S_element007,O_element023]
  conduct = 2
  density = 1
  expand = 3
  formula = G4_CALCIUM_SULFATE
  name = G4_CALCIUM_SULFATE
  specific = 4
FEATURE [App::DocumentObjectGroupPython] Ca_element009  label="Ca_element : 005"  # scripted group (container) (typed FeaturePython)
  n = 1
  ref = Ca_element
FEATURE [App::DocumentObjectGroupPython] W_element002  label="W_element : 002"  # scripted group (container) (typed FeaturePython)
  n = 1
  ref = W_element
FEATURE [App::DocumentObjectGroupPython] O_element024  label="O_element : 012"  # scripted group (container) (typed FeaturePython)
  n = 4
  ref = O_element
FEATURE [App::DocumentObjectGroupPython] G4_CALCIUM_TUNGSTATE  # scripted group (container) (typed FeaturePython)
  Dunit = g/cm3
  Dvalue = 6.062
  Group = -> [Ca_element009,W_element002,O_element024]
  conduct = 2
  density = 1
  expand = 3
  formula = G4_CALCIUM_TUNGSTATE
  name = G4_CALCIUM_TUNGSTATE
  specific = 4
FEATURE [App::DocumentObjectGroupPython] C_element023  label="C_element : 010"  # scripted group (container) (typed FeaturePython)
  n = 1
  ref = C_element
FEATURE [App::DocumentObjectGroupPython] O_element025  label="O_element : 013"  # scripted group (container) (typed FeaturePython)
  n = 2
  ref = O_element
FEATURE [App::DocumentObjectGroupPython] G4_CARBON_DIOXIDE  # scripted group (container) (typed FeaturePython)
  Dunit = g/cm3
  Dvalue = 0.00184212
  Group = -> [C_element023,O_element025]
  conduct = 2
  density = 1
  expand = 3
  formula = G4_CARBON_DIOXIDE
  name = G4_CARBON_DIOXIDE
  specific = 4
FEATURE [App::DocumentObjectGroupPython] C_element024  label="C_element : 011"  # scripted group (container) (typed FeaturePython)
  n = 1
  ref = C_element
FEATURE [App::DocumentObjectGroupPython] Cl_element004  label="Cl_element : 4"  # scripted group (container) (typed FeaturePython)
  n = 4
  ref = Cl_element
FEATURE [App::DocumentObjectGroupPython] G4_CARBON_TETRACHLORIDE  # scripted group (container) (typed FeaturePython)
  Dunit = g/cm3
  Dvalue = 1.594
  Group = -> [C_element024,Cl_element004]
  conduct = 2
  density = 1
  expand = 3
  formula = G4_CARBON_TETRACHLORIDE
  name = G4_CARBON_TETRACHLORIDE
  specific = 4
FEATURE [App::DocumentObjectGroupPython] C_element025  label="C_element : 012"  # scripted group (container) (typed FeaturePython)
  n = 6
  ref = C_element
FEATURE [App::DocumentObjectGroupPython] H_element021  label="H_element : 012"  # scripted group (container) (typed FeaturePython)
  n = 10
  ref = H_element
FEATURE [App::DocumentObjectGroupPython] O_element026  label="O_element : 5"  # scripted group (container) (typed FeaturePython)
  n = 5
  ref = O_element
FEATURE [App::DocumentObjectGroupPython] G4_CELLULOSE_CELLOPHANE  # scripted group (container) (typed FeaturePython)
  Dunit = g/cm3
  Dvalue = 1.42
  Group = -> [C_element025,H_element021,O_element026]
  conduct = 2
  density = 1
  expand = 3
  formula = G4_CELLULOSE_CELLOPHANE
  name = G4_CELLULOSE_CELLOPHANE
  specific = 4
FEATURE [App::DocumentObjectGroupPython] H_element022  label="H_element : 0.067"  # scripted group (container) (typed FeaturePython)
  n = 0.067125
FEATURE [App::DocumentObjectGroupPython] C_element026  label="C_element : 0.545"  # scripted group (container) (typed FeaturePython)
  n = 0.545403
FEATURE [App::DocumentObjectGroupPython] O_element027  label="O_element : 0.387"  # scripted group (container) (typed FeaturePython)
  n = 0.387472
FEATURE [App::DocumentObjectGroupPython] G4_CELLULOSE_BUTYRATE  # scripted group (container) (typed FeaturePython)
  Dunit = g/cm3
  Dvalue = 1.2
  Group = -> [H_element022,C_element026,O_element027]
  conduct = 2
  density = 1
  expand = 3
  formula = G4_CELLULOSE_BUTYRATE
  name = G4_CELLULOSE_BUTYRATE
  specific = 4
FEATURE [App::DocumentObjectGroupPython] H_element023  label="H_element : 0.029"  # scripted group (container) (typed FeaturePython)
  n = 0.029216
FEATURE [App::DocumentObjectGroupPython] C_element027  label="C_element : 0.271"  # scripted group (container) (typed FeaturePython)
  n = 0.271296
FEATURE [App::DocumentObjectGroupPython] N_element013  label="N_element : 0.121"  # scripted group (container) (typed FeaturePython)
  n = 0.121276
FEATURE [App::DocumentObjectGroupPython] O_element028  label="O_element : 0.578"  # scripted group (container) (typed FeaturePython)
  n = 0.578212
FEATURE [App::DocumentObjectGroupPython] G4_CELLULOSE_NITRATE  # scripted group (container) (typed FeaturePython)
  Dunit = g/cm3
  Dvalue = 1.49
  Group = -> [H_element023,C_element027,N_element013,O_element028]
  conduct = 2
  density = 1
  expand = 3
  formula = G4_CELLULOSE_NITRATE
  name = G4_CELLULOSE_NITRATE
  specific = 4
FEATURE [App::DocumentObjectGroupPython] H_element024  label="H_element : 0.108"  # scripted group (container) (typed FeaturePython)
  n = 0.107596
FEATURE [App::DocumentObjectGroupPython] N_element014  label="N_element : 0.001"  # scripted group (container) (typed FeaturePython)
  n = 0.0008
FEATURE [App::DocumentObjectGroupPython] O_element029  label="O_element : 0.875"  # scripted group (container) (typed FeaturePython)
  n = 0.874976
FEATURE [App::DocumentObjectGroupPython] S_element008  label="S_element : 0.015"  # scripted group (container) (typed FeaturePython)
  n = 0.014627
FEATURE [App::DocumentObjectGroupPython] Ce_element001  label="Ce_element : 0.002"  # scripted group (container) (typed FeaturePython)
  n = 0.002001
FEATURE [App::DocumentObjectGroupPython] G4_CERIC_SULFATE  # scripted group (container) (typed FeaturePython)
  Dunit = g/cm3
  Dvalue = 1.03
  Group = -> [H_element024,N_element014,O_element029,S_element008,Ce_element001]
  conduct = 2
  density = 1
  expand = 3
  formula = G4_CERIC_SULFATE
  name = G4_CERIC_SULFATE
  specific = 4
FEATURE [App::DocumentObjectGroupPython] Cs_element001  label="Cs_element : 1"  # scripted group (container) (typed FeaturePython)
  n = 1
  ref = Cs_element
FEATURE [App::DocumentObjectGroupPython] F_element006  label="F_element : 1"  # scripted group (container) (typed FeaturePython)
  n = 1
  ref = F_element
FEATURE [App::DocumentObjectGroupPython] G4_CESIUM_FLUORIDE  # scripted group (container) (typed FeaturePython)
  Dunit = g/cm3
  Dvalue = 4.115
  Group = -> [Cs_element001,F_element006]
  conduct = 2
  density = 1
  expand = 3
  formula = G4_CESIUM_FLUORIDE
  name = G4_CESIUM_FLUORIDE
  specific = 4
FEATURE [App::DocumentObjectGroupPython] Cs_element002  label="Cs_element : 002"  # scripted group (container) (typed FeaturePython)
  n = 1
  ref = Cs_element
FEATURE [App::DocumentObjectGroupPython] I_element001  label="I_element : 1"  # scripted group (container) (typed FeaturePython)
  n = 1
  ref = I_element
FEATURE [App::DocumentObjectGroupPython] G4_CESIUM_IODIDE001  label="G4_CESIUM_IODIDE"  # scripted group (container) (typed FeaturePython)
  Dunit = g/cm3
  Dvalue = 4.51
  Group = -> [Cs_element002,I_element001]
  conduct = 2
  density = 1
  expand = 3
  formula = G4_CESIUM_IODIDE
  name = G4_CESIUM_IODIDE
  specific = 4
FEATURE [App::DocumentObjectGroupPython] C_element028  label="C_element : 013"  # scripted group (container) (typed FeaturePython)
  n = 6
  ref = C_element
FEATURE [App::DocumentObjectGroupPython] H_element025  label="H_element : 013"  # scripted group (container) (typed FeaturePython)
  n = 5
  ref = H_element
FEATURE [App::DocumentObjectGroupPython] Cl_element005  label="Cl_element : 1"  # scripted group (container) (typed FeaturePython)
  n = 1
  ref = Cl_element
FEATURE [App::DocumentObjectGroupPython] G4_CHLOROBENZENE  # scripted group (container) (typed FeaturePython)
  Dunit = g/cm3
  Dvalue = 1.1058
  Group = -> [C_element028,H_element025,Cl_element005]
  conduct = 2
  density = 1
  expand = 3
  formula = G4_CHLOROBENZENE
  name = G4_CHLOROBENZENE
  specific = 4
FEATURE [App::DocumentObjectGroupPython] C_element029  label="C_element : 014"  # scripted group (container) (typed FeaturePython)
  n = 1
  ref = C_element
FEATURE [App::DocumentObjectGroupPython] H_element026  label="H_element : 1"  # scripted group (container) (typed FeaturePython)
  n = 1
  ref = H_element
FEATURE [App::DocumentObjectGroupPython] Cl_element006  label="Cl_element : 3"  # scripted group (container) (typed FeaturePython)
  n = 3
  ref = Cl_element
FEATURE [App::DocumentObjectGroupPython] G4_CHLOROFORM  # scripted group (container) (typed FeaturePython)
  Dunit = g/cm3
  Dvalue = 1.4832
  Group = -> [C_element029,H_element026,Cl_element006]
  conduct = 2
  density = 1
  expand = 3
  formula = G4_CHLOROFORM
  name = G4_CHLOROFORM
  specific = 4
FEATURE [App::DocumentObjectGroupPython] H_element027  label="H_element : 0.010"  # scripted group (container) (typed FeaturePython)
  n = 0.01
FEATURE [App::DocumentObjectGroupPython] C_element030  label="C_element : 0.001"  # scripted group (container) (typed FeaturePython)
  n = 0.001
FEATURE [App::DocumentObjectGroupPython] O_element030  label="O_element : 0.529"  # scripted group (container) (typed FeaturePython)
  n = 0.529107
FEATURE [App::DocumentObjectGroupPython] Na_element005  label="Na_element : 0.016"  # scripted group (container) (typed FeaturePython)
  n = 0.016
FEATURE [App::DocumentObjectGroupPython] Mg_element003  label="Mg_element : 0.004"  # scripted group (container) (typed FeaturePython)
  n = 0.002
FEATURE [App::DocumentObjectGroupPython] Al_element002  label="Al_element : 0.034"  # scripted group (container) (typed FeaturePython)
  n = 0.033872
FEATURE [App::DocumentObjectGroupPython] Si_element002  label="Si_element : 0.337"  # scripted group (container) (typed FeaturePython)
  n = 0.337021
FEATURE [App::DocumentObjectGroupPython] K_element003  label="K_element : 0.013"  # scripted group (container) (typed FeaturePython)
  n = 0.013
FEATURE [App::DocumentObjectGroupPython] Ca_element010  label="Ca_element : 0.044"  # scripted group (container) (typed FeaturePython)
  n = 0.044
FEATURE [App::DocumentObjectGroupPython] Fe_element002  label="Fe_element : 0.014"  # scripted group (container) (typed FeaturePython)
  n = 0.014
FEATURE [App::DocumentObjectGroupPython] G4_CONCRETE  # scripted group (container) (typed FeaturePython)
  Dunit = g/cm3
  Dvalue = 2.3
  Group = -> [H_element027,C_element030,O_element030,Na_element005,Mg_element003,Al_element002,Si_element002,K_element003,Ca_element010,Fe_element002]
  conduct = 2
  density = 1
  expand = 3
  formula = G4_CONCRETE
  name = G4_CONCRETE
  specific = 4
FEATURE [App::DocumentObjectGroupPython] C_element031  label="C_element : 015"  # scripted group (container) (typed FeaturePython)
  n = 6
  ref = C_element
FEATURE [App::DocumentObjectGroupPython] H_element028  label="H_element : 12"  # scripted group (container) (typed FeaturePython)
  n = 12
  ref = H_element
FEATURE [App::DocumentObjectGroupPython] G4_CYCLOHEXANE  # scripted group (container) (typed FeaturePython)
  Dunit = g/cm3
  Dvalue = 0.779
  Group = -> [C_element031,H_element028]
  conduct = 2
  density = 1
  expand = 3
  formula = G4_CYCLOHEXANE
  name = G4_CYCLOHEXANE
  specific = 4
FEATURE [App::DocumentObjectGroupPython] C_element032  label="C_element : 016"  # scripted group (container) (typed FeaturePython)
  n = 6
  ref = C_element
FEATURE [App::DocumentObjectGroupPython] H_element029  label="H_element : 4"  # scripted group (container) (typed FeaturePython)
  n = 4
  ref = H_element
FEATURE [App::DocumentObjectGroupPython] Cl_element007  label="Cl_element : 2"  # scripted group (container) (typed FeaturePython)
  n = 2
  ref = Cl_element
FEATURE [App::DocumentObjectGroupPython] G4_1_2_DICHLOROBENZENE  label="G4_1.2-DICHLOROBENZENE"  # scripted group (container) (typed FeaturePython)
  Dunit = g/cm3
  Dvalue = 1.3048
  Group = -> [C_element032,H_element029,Cl_element007]
  conduct = 2
  density = 1
  expand = 3
  formula = G4_1.2-DICHLOROBENZENE
  name = G4_1.2-DICHLOROBENZENE
  specific = 4
FEATURE [App::DocumentObjectGroupPython] C_element033  label="C_element : 017"  # scripted group (container) (typed FeaturePython)
  n = 4
  ref = C_element
FEATURE [App::DocumentObjectGroupPython] H_element030  label="H_element : 8"  # scripted group (container) (typed FeaturePython)
  n = 8
  ref = H_element
FEATURE [App::DocumentObjectGroupPython] O_element031  label="O_element : 014"  # scripted group (container) (typed FeaturePython)
  n = 1
  ref = O_element
FEATURE [App::DocumentObjectGroupPython] Cl_element008  label="Cl_element : 005"  # scripted group (container) (typed FeaturePython)
  n = 2
  ref = Cl_element
FEATURE [App::DocumentObjectGroupPython] G4_DICHLORODIETHYL_ETHER  # scripted group (container) (typed FeaturePython)
  Dunit = g/cm3
  Dvalue = 1.2199
  Group = -> [C_element033,H_element030,O_element031,Cl_element008]
  conduct = 2
  density = 1
  expand = 3
  formula = G4_DICHLORODIETHYL_ETHER
  name = G4_DICHLORODIETHYL_ETHER
  specific = 4
FEATURE [App::DocumentObjectGroupPython] C_element034  label="C_element : 018"  # scripted group (container) (typed FeaturePython)
  n = 2
  ref = C_element
FEATURE [App::DocumentObjectGroupPython] H_element031  label="H_element : 014"  # scripted group (container) (typed FeaturePython)
  n = 4
  ref = H_element
FEATURE [App::DocumentObjectGroupPython] Cl_element009  label="Cl_element : 006"  # scripted group (container) (typed FeaturePython)
  n = 2
  ref = Cl_element
FEATURE [App::DocumentObjectGroupPython] G4_1_2_DICHLOROETHANE  label="G4_1.2-DICHLOROETHANE"  # scripted group (container) (typed FeaturePython)
  Dunit = g/cm3
  Dvalue = 1.2351
  Group = -> [C_element034,H_element031,Cl_element009]
  conduct = 2
  density = 1
  expand = 3
  formula = G4_1.2-DICHLOROETHANE
  name = G4_1.2-DICHLOROETHANE
  specific = 4
FEATURE [App::DocumentObjectGroupPython] C_element035  label="C_element : 019"  # scripted group (container) (typed FeaturePython)
  n = 4
  ref = C_element
FEATURE [App::DocumentObjectGroupPython] H_element032  label="H_element : 015"  # scripted group (container) (typed FeaturePython)
  n = 10
  ref = H_element
FEATURE [App::DocumentObjectGroupPython] O_element032  label="O_element : 015"  # scripted group (container) (typed FeaturePython)
  n = 1
  ref = O_element
FEATURE [App::DocumentObjectGroupPython] G4_DIETHYL_ETHER  # scripted group (container) (typed FeaturePython)
  Dunit = g/cm3
  Dvalue = 0.71378
  Group = -> [C_element035,H_element032,O_element032]
  conduct = 2
  density = 1
  expand = 3
  formula = G4_DIETHYL_ETHER
  name = G4_DIETHYL_ETHER
  specific = 4
FEATURE [App::DocumentObjectGroupPython] C_element036  label="C_element : 020"  # scripted group (container) (typed FeaturePython)
  n = 3
  ref = C_element
FEATURE [App::DocumentObjectGroupPython] H_element033  label="H_element : 016"  # scripted group (container) (typed FeaturePython)
  n = 7
  ref = H_element
FEATURE [App::DocumentObjectGroupPython] N_element015  label="N_element : 008"  # scripted group (container) (typed FeaturePython)
  n = 1
  ref = N_element
FEATURE [App::DocumentObjectGroupPython] O_element033  label="O_element : 016"  # scripted group (container) (typed FeaturePython)
  n = 1
  ref = O_element
FEATURE [App::DocumentObjectGroupPython] G4_N_N_DIMETHYL_FORMAMIDE  label="G4_N.N-DIMETHYL_FORMAMIDE"  # scripted group (container) (typed FeaturePython)
  Dunit = g/cm3
  Dvalue = 0.9487
  Group = -> [C_element036,H_element033,N_element015,O_element033]
  conduct = 2
  density = 1
  expand = 3
  formula = G4_N.N-DIMETHYL_FORMAMIDE
  name = G4_N.N-DIMETHYL_FORMAMIDE
  specific = 4
FEATURE [App::DocumentObjectGroupPython] C_element037  label="C_element : 021"  # scripted group (container) (typed FeaturePython)
  n = 2
  ref = C_element
FEATURE [App::DocumentObjectGroupPython] H_element034  label="H_element : 017"  # scripted group (container) (typed FeaturePython)
  n = 6
  ref = H_element
FEATURE [App::DocumentObjectGroupPython] O_element034  label="O_element : 017"  # scripted group (container) (typed FeaturePython)
  n = 1
  ref = O_element
FEATURE [App::DocumentObjectGroupPython] S_element009  label="S_element : 003"  # scripted group (container) (typed FeaturePython)
  n = 1
  ref = S_element
FEATURE [App::DocumentObjectGroupPython] G4_DIMETHYL_SULFOXIDE  # scripted group (container) (typed FeaturePython)
  Dunit = g/cm3
  Dvalue = 1.1014
  Group = -> [C_element037,H_element034,O_element034,S_element009]
  conduct = 2
  density = 1
  expand = 3
  formula = G4_DIMETHYL_SULFOXIDE
  name = G4_DIMETHYL_SULFOXIDE
  specific = 4
FEATURE [App::DocumentObjectGroupPython] C_element038  label="C_element : 022"  # scripted group (container) (typed FeaturePython)
  n = 2
  ref = C_element
FEATURE [App::DocumentObjectGroupPython] H_element035  label="H_element : 018"  # scripted group (container) (typed FeaturePython)
  n = 6
  ref = H_element
FEATURE [App::DocumentObjectGroupPython] G4_ETHANE  # scripted group (container) (typed FeaturePython)
  Dunit = g/cm3
  Dvalue = 0.00125324
  Group = -> [C_element038,H_element035]
  conduct = 2
  density = 1
  expand = 3
  formula = G4_ETHANE
  name = G4_ETHANE
  specific = 4
FEATURE [App::DocumentObjectGroupPython] C_element039  label="C_element : 023"  # scripted group (container) (typed FeaturePython)
  n = 2
  ref = C_element
FEATURE [App::DocumentObjectGroupPython] H_element036  label="H_element : 019"  # scripted group (container) (typed FeaturePython)
  n = 6
  ref = H_element
FEATURE [App::DocumentObjectGroupPython] O_element035  label="O_element : 018"  # scripted group (container) (typed FeaturePython)
  n = 1
  ref = O_element
FEATURE [App::DocumentObjectGroupPython] G4_ETHYL_ALCOHOL  # scripted group (container) (typed FeaturePython)
  Dunit = g/cm3
  Dvalue = 0.7893
  Group = -> [C_element039,H_element036,O_element035]
  conduct = 2
  density = 1
  expand = 3
  formula = G4_ETHYL_ALCOHOL
  name = G4_ETHYL_ALCOHOL
  specific = 4
FEATURE [App::DocumentObjectGroupPython] H_element037  label="H_element : 0.090"  # scripted group (container) (typed FeaturePython)
  n = 0.090027
FEATURE [App::DocumentObjectGroupPython] C_element040  label="C_element : 0.585"  # scripted group (container) (typed FeaturePython)
  n = 0.585182
FEATURE [App::DocumentObjectGroupPython] O_element036  label="O_element : 0.325"  # scripted group (container) (typed FeaturePython)
  n = 0.324791
FEATURE [App::DocumentObjectGroupPython] G4_ETHYL_CELLULOSE  # scripted group (container) (typed FeaturePython)
  Dunit = g/cm3
  Dvalue = 1.13
  Group = -> [H_element037,C_element040,O_element036]
  conduct = 2
  density = 1
  expand = 3
  formula = G4_ETHYL_CELLULOSE
  name = G4_ETHYL_CELLULOSE
  specific = 4
FEATURE [App::DocumentObjectGroupPython] C_element041  label="C_element : 024"  # scripted group (container) (typed FeaturePython)
  n = 2
  ref = C_element
FEATURE [App::DocumentObjectGroupPython] H_element038  label="H_element : 020"  # scripted group (container) (typed FeaturePython)
  n = 4
  ref = H_element
FEATURE [App::DocumentObjectGroupPython] G4_ETHYLENE  # scripted group (container) (typed FeaturePython)
  Dunit = g/cm3
  Dvalue = 0.00117497
  Group = -> [C_element041,H_element038]
  conduct = 2
  density = 1
  expand = 3
  formula = G4_ETHYLENE
  name = G4_ETHYLENE
  specific = 4
FEATURE [App::DocumentObjectGroupPython] H_element039  label="H_element : 0.096"  # scripted group (container) (typed FeaturePython)
  n = 0.096
FEATURE [App::DocumentObjectGroupPython] C_element042  label="C_element : 0.195"  # scripted group (container) (typed FeaturePython)
  n = 0.195
FEATURE [App::DocumentObjectGroupPython] N_element016  label="N_element : 0.057"  # scripted group (container) (typed FeaturePython)
  n = 0.057
FEATURE [App::DocumentObjectGroupPython] O_element037  label="O_element : 0.646"  # scripted group (container) (typed FeaturePython)
  n = 0.646
FEATURE [App::DocumentObjectGroupPython] Na_element006  label="Na_element : 0.017"  # scripted group (container) (typed FeaturePython)
  n = 0.001
FEATURE [App::DocumentObjectGroupPython] P_element005  label="P_element : 0.104"  # scripted group (container) (typed FeaturePython)
  n = 0.001
FEATURE [App::DocumentObjectGroupPython] S_element010  label="S_element : 0.016"  # scripted group (container) (typed FeaturePython)
  n = 0.003
FEATURE [App::DocumentObjectGroupPython] Cl_element010  label="Cl_element : 0.005"  # scripted group (container) (typed FeaturePython)
  n = 0.001
FEATURE [App::DocumentObjectGroupPython] G4_EYE_LENS_ICRP  # scripted group (container) (typed FeaturePython)
  Dunit = g/cm3
  Dvalue = 1.07
  Group = -> [H_element039,C_element042,N_element016,O_element037,Na_element006,P_element005,S_element010,Cl_element010]
  conduct = 2
  density = 1
  expand = 3
  formula = G4_EYE_LENS_ICRP
  name = G4_EYE_LENS_ICRP
  specific = 4
FEATURE [App::DocumentObjectGroupPython] Fe_element003  label="Fe_element : 2"  # scripted group (container) (typed FeaturePython)
  n = 2
  ref = Fe_element
FEATURE [App::DocumentObjectGroupPython] O_element038  label="O_element : 019"  # scripted group (container) (typed FeaturePython)
  n = 3
  ref = O_element
FEATURE [App::DocumentObjectGroupPython] G4_FERRIC_OXIDE  # scripted group (container) (typed FeaturePython)
  Dunit = g/cm3
  Dvalue = 5.2
  Group = -> [Fe_element003,O_element038]
  conduct = 2
  density = 1
  expand = 3
  formula = G4_FERRIC_OXIDE
  name = G4_FERRIC_OXIDE
  specific = 4
FEATURE [App::DocumentObjectGroupPython] Fe_element004  label="Fe_element : 1"  # scripted group (container) (typed FeaturePython)
  n = 1
  ref = Fe_element
FEATURE [App::DocumentObjectGroupPython] B_element003  label="B_element : 1"  # scripted group (container) (typed FeaturePython)
  n = 1
  ref = B_element
FEATURE [App::DocumentObjectGroupPython] G4_FERROBORIDE  # scripted group (container) (typed FeaturePython)
  Dunit = g/cm3
  Dvalue = 7.15
  Group = -> [Fe_element004,B_element003]
  conduct = 2
  density = 1
  expand = 3
  formula = G4_FERROBORIDE
  name = G4_FERROBORIDE
  specific = 4
FEATURE [App::DocumentObjectGroupPython] Fe_element005  label="Fe_element : 003"  # scripted group (container) (typed FeaturePython)
  n = 1
  ref = Fe_element
FEATURE [App::DocumentObjectGroupPython] O_element039  label="O_element : 020"  # scripted group (container) (typed FeaturePython)
  n = 1
  ref = O_element
FEATURE [App::DocumentObjectGroupPython] G4_FERROUS_OXIDE  # scripted group (container) (typed FeaturePython)
  Dunit = g/cm3
  Dvalue = 5.7
  Group = -> [Fe_element005,O_element039]
  conduct = 2
  density = 1
  expand = 3
  formula = G4_FERROUS_OXIDE
  name = G4_FERROUS_OXIDE
  specific = 4
FEATURE [App::DocumentObjectGroupPython] H_element040  label="H_element : 0.115"  # scripted group (container) (typed FeaturePython)
  n = 0.108259
FEATURE [App::DocumentObjectGroupPython] N_element017  label="N_element : 0.000"  # scripted group (container) (typed FeaturePython)
  n = 2.7e-05
FEATURE [App::DocumentObjectGroupPython] O_element040  label="O_element : 0.879"  # scripted group (container) (typed FeaturePython)
  n = 0.878636
FEATURE [App::DocumentObjectGroupPython] Na_element007  label="Na_element : 0.000"  # scripted group (container) (typed FeaturePython)
  n = 2.2e-05
FEATURE [App::DocumentObjectGroupPython] S_element011  label="S_element : 0.013"  # scripted group (container) (typed FeaturePython)
  n = 0.012968
FEATURE [App::DocumentObjectGroupPython] Cl_element011  label="Cl_element : 0.000"  # scripted group (container) (typed FeaturePython)
  n = 3.4e-05
FEATURE [App::DocumentObjectGroupPython] Fe_element006  label="Fe_element : 0.000"  # scripted group (container) (typed FeaturePython)
  n = 5.4e-05
FEATURE [App::DocumentObjectGroupPython] G4_FERROUS_SULFATE  # scripted group (container) (typed FeaturePython)
  Dunit = g/cm3
  Dvalue = 1.024
  Group = -> [H_element040,N_element017,O_element040,Na_element007,S_element011,Cl_element011,Fe_element006]
  conduct = 2
  density = 1
  expand = 3
  formula = G4_FERROUS_SULFATE
  name = G4_FERROUS_SULFATE
  specific = 4
FEATURE [App::DocumentObjectGroupPython] C_element043  label="C_element : 0.099"  # scripted group (container) (typed FeaturePython)
  n = 0.099335
FEATURE [App::DocumentObjectGroupPython] F_element007  label="F_element : 0.314"  # scripted group (container) (typed FeaturePython)
  n = 0.314247
FEATURE [App::DocumentObjectGroupPython] Cl_element012  label="Cl_element : 0.586"  # scripted group (container) (typed FeaturePython)
  n = 0.586418
FEATURE [App::DocumentObjectGroupPython] G4_FREON_12  label="G4_FREON-12"  # scripted group (container) (typed FeaturePython)
  Dunit = g/cm3
  Dvalue = 1.12
  Group = -> [C_element043,F_element007,Cl_element012]
  conduct = 2
  density = 1
  expand = 3
  formula = G4_FREON-12
  name = G4_FREON-12
  specific = 4
FEATURE [App::DocumentObjectGroupPython] C_element044  label="C_element : 0.057"  # scripted group (container) (typed FeaturePython)
  n = 0.057245
FEATURE [App::DocumentObjectGroupPython] F_element008  label="F_element : 0.181"  # scripted group (container) (typed FeaturePython)
  n = 0.181096
FEATURE [App::DocumentObjectGroupPython] Br_element001  label="Br_element : 0.762"  # scripted group (container) (typed FeaturePython)
  n = 0.761659
FEATURE [App::DocumentObjectGroupPython] G4_FREON_12B2  label="G4_FREON-12B2"  # scripted group (container) (typed FeaturePython)
  Dunit = g/cm3
  Dvalue = 1.8
  Group = -> [C_element044,F_element008,Br_element001]
  conduct = 2
  density = 1
  expand = 3
  formula = G4_FREON-12B2
  name = G4_FREON-12B2
  specific = 4
FEATURE [App::DocumentObjectGroupPython] C_element045  label="C_element : 0.115"  # scripted group (container) (typed FeaturePython)
  n = 0.114983
FEATURE [App::DocumentObjectGroupPython] F_element009  label="F_element : 0.546"  # scripted group (container) (typed FeaturePython)
  n = 0.545621
FEATURE [App::DocumentObjectGroupPython] Cl_element013  label="Cl_element : 0.339"  # scripted group (container) (typed FeaturePython)
  n = 0.339396
FEATURE [App::DocumentObjectGroupPython] G4_FREON_13  label="G4_FREON-13"  # scripted group (container) (typed FeaturePython)
  Dunit = g/cm3
  Dvalue = 0.95
  Group = -> [C_element045,F_element009,Cl_element013]
  conduct = 2
  density = 1
  expand = 3
  formula = G4_FREON-13
  name = G4_FREON-13
  specific = 4
FEATURE [App::DocumentObjectGroupPython] C_element046  label="C_element : 025"  # scripted group (container) (typed FeaturePython)
  n = 1
  ref = C_element
FEATURE [App::DocumentObjectGroupPython] F_element010  label="F_element : 3"  # scripted group (container) (typed FeaturePython)
  n = 3
  ref = F_element
FEATURE [App::DocumentObjectGroupPython] Br_element002  label="Br_element : 1"  # scripted group (container) (typed FeaturePython)
  n = 1
  ref = Br_element
FEATURE [App::DocumentObjectGroupPython] G4_FREON_13B1  label="G4_FREON-13B1"  # scripted group (container) (typed FeaturePython)
  Dunit = g/cm3
  Dvalue = 1.5
  Group = -> [C_element046,F_element010,Br_element002]
  conduct = 2
  density = 1
  expand = 3
  formula = G4_FREON-13B1
  name = G4_FREON-13B1
  specific = 4
FEATURE [App::DocumentObjectGroupPython] C_element047  label="C_element : 0.061"  # scripted group (container) (typed FeaturePython)
  n = 0.061309
FEATURE [App::DocumentObjectGroupPython] F_element011  label="F_element : 0.291"  # scripted group (container) (typed FeaturePython)
  n = 0.290924
FEATURE [App::DocumentObjectGroupPython] I_element002  label="I_element : 0.648"  # scripted group (container) (typed FeaturePython)
  n = 0.647767
FEATURE [App::DocumentObjectGroupPython] G4_FREON_13I1  label="G4_FREON-13I1"  # scripted group (container) (typed FeaturePython)
  Dunit = g/cm3
  Dvalue = 1.8
  Group = -> [C_element047,F_element011,I_element002]
  conduct = 2
  density = 1
  expand = 3
  formula = G4_FREON-13I1
  name = G4_FREON-13I1
  specific = 4
FEATURE [App::DocumentObjectGroupPython] Gd_element001  label="Gd_element : 2"  # scripted group (container) (typed FeaturePython)
  n = 2
  ref = Gd_element
FEATURE [App::DocumentObjectGroupPython] O_element041  label="O_element : 021"  # scripted group (container) (typed FeaturePython)
  n = 2
  ref = O_element
FEATURE [App::DocumentObjectGroupPython] S_element012  label="S_element : 004"  # scripted group (container) (typed FeaturePython)
  n = 1
  ref = S_element
FEATURE [App::DocumentObjectGroupPython] G4_GADOLINIUM_OXYSULFIDE  # scripted group (container) (typed FeaturePython)
  Dunit = g/cm3
  Dvalue = 7.44
  Group = -> [Gd_element001,O_element041,S_element012]
  conduct = 2
  density = 1
  expand = 3
  formula = G4_GADOLINIUM_OXYSULFIDE
  name = G4_GADOLINIUM_OXYSULFIDE
  specific = 4
FEATURE [App::DocumentObjectGroupPython] Ga_element001  label="Ga_element : 1"  # scripted group (container) (typed FeaturePython)
  n = 1
  ref = Ga_element
FEATURE [App::DocumentObjectGroupPython] As_element001  label="As_element : 1"  # scripted group (container) (typed FeaturePython)
  n = 1
  ref = As_element
FEATURE [App::DocumentObjectGroupPython] G4_GALLIUM_ARSENIDE  # scripted group (container) (typed FeaturePython)
  Dunit = g/cm3
  Dvalue = 5.31
  Group = -> [Ga_element001,As_element001]
  conduct = 2
  density = 1
  expand = 3
  formula = G4_GALLIUM_ARSENIDE
  name = G4_GALLIUM_ARSENIDE
  specific = 4
FEATURE [App::DocumentObjectGroupPython] H_element041  label="H_element : 0.081"  # scripted group (container) (typed FeaturePython)
  n = 0.08118
FEATURE [App::DocumentObjectGroupPython] C_element048  label="C_element : 0.416"  # scripted group (container) (typed FeaturePython)
  n = 0.41606
FEATURE [App::DocumentObjectGroupPython] N_element018  label="N_element : 0.111"  # scripted group (container) (typed FeaturePython)
  n = 0.11124
FEATURE [App::DocumentObjectGroupPython] O_element042  label="O_element : 0.381"  # scripted group (container) (typed FeaturePython)
  n = 0.38064
FEATURE [App::DocumentObjectGroupPython] S_element013  label="S_element : 0.011"  # scripted group (container) (typed FeaturePython)
  n = 0.01088
FEATURE [App::DocumentObjectGroupPython] G4_GEL_PHOTO_EMULSION  # scripted group (container) (typed FeaturePython)
  Dunit = g/cm3
  Dvalue = 1.2914
  Group = -> [H_element041,C_element048,N_element018,O_element042,S_element013]
  conduct = 2
  density = 1
  expand = 3
  formula = G4_GEL_PHOTO_EMULSION
  name = G4_GEL_PHOTO_EMULSION
  specific = 4
FEATURE [App::DocumentObjectGroupPython] B_element004  label="B_element : 0.040"  # scripted group (container) (typed FeaturePython)
  n = 0.0400639
FEATURE [App::DocumentObjectGroupPython] O_element043  label="O_element : 0.540"  # scripted group (container) (typed FeaturePython)
  n = 0.539561
FEATURE [App::DocumentObjectGroupPython] Na_element008  label="Na_element : 0.028"  # scripted group (container) (typed FeaturePython)
  n = 0.0281909
FEATURE [App::DocumentObjectGroupPython] Al_element003  label="Al_element : 0.012"  # scripted group (container) (typed FeaturePython)
  n = 0.011644
FEATURE [App::DocumentObjectGroupPython] Si_element003  label="Si_element : 0.377"  # scripted group (container) (typed FeaturePython)
  n = 0.377219
FEATURE [App::DocumentObjectGroupPython] K_element004  label="K_element : 0.014"  # scripted group (container) (typed FeaturePython)
  n = 0.00332099
FEATURE [App::DocumentObjectGroupPython] G4_Pyrex_Glass  # scripted group (container) (typed FeaturePython)
  Dunit = g/cm3
  Dvalue = 2.23
  Group = -> [B_element004,O_element043,Na_element008,Al_element003,Si_element003,K_element004]
  conduct = 2
  density = 1
  expand = 3
  formula = G4_Pyrex_Glass
  name = G4_Pyrex_Glass
  specific = 4
FEATURE [App::DocumentObjectGroupPython] O_element044  label="O_element : 0.156"  # scripted group (container) (typed FeaturePython)
  n = 0.156453
FEATURE [App::DocumentObjectGroupPython] Si_element004  label="Si_element : 0.081"  # scripted group (container) (typed FeaturePython)
  n = 0.080866
FEATURE [App::DocumentObjectGroupPython] Ti_element001  label="Ti_element : 0.008"  # scripted group (container) (typed FeaturePython)
  n = 0.008092
FEATURE [App::DocumentObjectGroupPython] As_element002  label="As_element : 0.003"  # scripted group (container) (typed FeaturePython)
  n = 0.002651
FEATURE [App::DocumentObjectGroupPython] Pb_element001  label="Pb_element : 0.752"  # scripted group (container) (typed FeaturePython)
  n = 0.751938
FEATURE [App::DocumentObjectGroupPython] G4_GLASS_LEAD  # scripted group (container) (typed FeaturePython)
  Dunit = g/cm3
  Dvalue = 6.22
  Group = -> [O_element044,Si_element004,Ti_element001,As_element002,Pb_element001]
  conduct = 2
  density = 1
  expand = 3
  formula = G4_GLASS_LEAD
  name = G4_GLASS_LEAD
  specific = 4
FEATURE [App::DocumentObjectGroupPython] O_element045  label="O_element : 0.460"  # scripted group (container) (typed FeaturePython)
  n = 0.4598
FEATURE [App::DocumentObjectGroupPython] Na_element009  label="Na_element : 0.096"  # scripted group (container) (typed FeaturePython)
  n = 0.0964411
FEATURE [App::DocumentObjectGroupPython] Si_element005  label="Si_element : 0.378"  # scripted group (container) (typed FeaturePython)
  n = 0.336553
FEATURE [App::DocumentObjectGroupPython] Ca_element011  label="Ca_element : 0.107"  # scripted group (container) (typed FeaturePython)
  n = 0.107205
FEATURE [App::DocumentObjectGroupPython] G4_GLASS_PLATE  # scripted group (container) (typed FeaturePython)
  Dunit = g/cm3
  Dvalue = 2.4
  Group = -> [O_element045,Na_element009,Si_element005,Ca_element011]
  conduct = 2
  density = 1
  expand = 3
  formula = G4_GLASS_PLATE
  name = G4_GLASS_PLATE
  specific = 4
FEATURE [App::DocumentObjectGroupPython] C_element049  label="C_element : 026"  # scripted group (container) (typed FeaturePython)
  n = 5
  ref = C_element
FEATURE [App::DocumentObjectGroupPython] H_element042  label="H_element : 021"  # scripted group (container) (typed FeaturePython)
  n = 10
  ref = H_element
FEATURE [App::DocumentObjectGroupPython] N_element019  label="N_element : 2"  # scripted group (container) (typed FeaturePython)
  n = 2
  ref = N_element
FEATURE [App::DocumentObjectGroupPython] O_element046  label="O_element : 022"  # scripted group (container) (typed FeaturePython)
  n = 3
  ref = O_element
FEATURE [App::DocumentObjectGroupPython] G4_GLUTAMINE  # scripted group (container) (typed FeaturePython)
  Dunit = g/cm3
  Dvalue = 1.46
  Group = -> [C_element049,H_element042,N_element019,O_element046]
  conduct = 2
  density = 1
  expand = 3
  formula = G4_GLUTAMINE
  name = G4_GLUTAMINE
  specific = 4
FEATURE [App::DocumentObjectGroupPython] C_element050  label="C_element : 027"  # scripted group (container) (typed FeaturePython)
  n = 3
  ref = C_element
FEATURE [App::DocumentObjectGroupPython] H_element043  label="H_element : 022"  # scripted group (container) (typed FeaturePython)
  n = 8
  ref = H_element
FEATURE [App::DocumentObjectGroupPython] O_element047  label="O_element : 023"  # scripted group (container) (typed FeaturePython)
  n = 3
  ref = O_element
FEATURE [App::DocumentObjectGroupPython] G4_GLYCEROL  # scripted group (container) (typed FeaturePython)
  Dunit = g/cm3
  Dvalue = 1.2613
  Group = -> [C_element050,H_element043,O_element047]
  conduct = 2
  density = 1
  expand = 3
  formula = G4_GLYCEROL
  name = G4_GLYCEROL
  specific = 4
FEATURE [App::DocumentObjectGroupPython] C_element051  label="C_element : 028"  # scripted group (container) (typed FeaturePython)
  n = 5
  ref = C_element
FEATURE [App::DocumentObjectGroupPython] H_element044  label="H_element : 023"  # scripted group (container) (typed FeaturePython)
  n = 5
  ref = H_element
FEATURE [App::DocumentObjectGroupPython] N_element020  label="N_element : 009"  # scripted group (container) (typed FeaturePython)
  n = 5
  ref = N_element
FEATURE [App::DocumentObjectGroupPython] O_element048  label="O_element : 024"  # scripted group (container) (typed FeaturePython)
  n = 1
  ref = O_element
FEATURE [App::DocumentObjectGroupPython] G4_GUANINE  # scripted group (container) (typed FeaturePython)
  Dunit = g/cm3
  Dvalue = 2.2
  Group = -> [C_element051,H_element044,N_element020,O_element048]
  conduct = 2
  density = 1
  expand = 3
  formula = G4_GUANINE
  name = G4_GUANINE
  specific = 4
FEATURE [App::DocumentObjectGroupPython] Ca_element012  label="Ca_element : 006"  # scripted group (container) (typed FeaturePython)
  n = 1
  ref = Ca_element
FEATURE [App::DocumentObjectGroupPython] S_element014  label="S_element : 005"  # scripted group (container) (typed FeaturePython)
  n = 1
  ref = S_element
FEATURE [App::DocumentObjectGroupPython] O_element049  label="O_element : 6"  # scripted group (container) (typed FeaturePython)
  n = 6
  ref = O_element
FEATURE [App::DocumentObjectGroupPython] H_element045  label="H_element : 024"  # scripted group (container) (typed FeaturePython)
  n = 4
  ref = H_element
FEATURE [App::DocumentObjectGroupPython] G4_GYPSUM  # scripted group (container) (typed FeaturePython)
  Dunit = g/cm3
  Dvalue = 2.32
  Group = -> [Ca_element012,S_element014,O_element049,H_element045]
  conduct = 2
  density = 1
  expand = 3
  formula = G4_GYPSUM
  name = G4_GYPSUM
  specific = 4
FEATURE [App::DocumentObjectGroupPython] C_element052  label="C_element : 7"  # scripted group (container) (typed FeaturePython)
  n = 7
  ref = C_element
FEATURE [App::DocumentObjectGroupPython] H_element046  label="H_element : 16"  # scripted group (container) (typed FeaturePython)
  n = 16
  ref = H_element
FEATURE [App::DocumentObjectGroupPython] G4_N_HEPTANE  label="G4_N-HEPTANE"  # scripted group (container) (typed FeaturePython)
  Dunit = g/cm3
  Dvalue = 0.68376
  Group = -> [C_element052,H_element046]
  conduct = 2
  density = 1
  expand = 3
  formula = G4_N-HEPTANE
  name = G4_N-HEPTANE
  specific = 4
FEATURE [App::DocumentObjectGroupPython] C_element053  label="C_element : 029"  # scripted group (container) (typed FeaturePython)
  n = 6
  ref = C_element
FEATURE [App::DocumentObjectGroupPython] H_element047  label="H_element : 14"  # scripted group (container) (typed FeaturePython)
  n = 14
  ref = H_element
FEATURE [App::DocumentObjectGroupPython] G4_N_HEXANE  label="G4_N-HEXANE"  # scripted group (container) (typed FeaturePython)
  Dunit = g/cm3
  Dvalue = 0.6603
  Group = -> [C_element053,H_element047]
  conduct = 2
  density = 1
  expand = 3
  formula = G4_N-HEXANE
  name = G4_N-HEXANE
  specific = 4
FEATURE [App::DocumentObjectGroupPython] C_element054  label="C_element : 22"  # scripted group (container) (typed FeaturePython)
  n = 22
  ref = C_element
FEATURE [App::DocumentObjectGroupPython] H_element048  label="H_element : 025"  # scripted group (container) (typed FeaturePython)
  n = 10
  ref = H_element
FEATURE [App::DocumentObjectGroupPython] N_element021  label="N_element : 010"  # scripted group (container) (typed FeaturePython)
  n = 2
  ref = N_element
FEATURE [App::DocumentObjectGroupPython] O_element050  label="O_element : 025"  # scripted group (container) (typed FeaturePython)
  n = 5
  ref = O_element
FEATURE [App::DocumentObjectGroupPython] G4_KAPTON  # scripted group (container) (typed FeaturePython)
  Dunit = g/cm3
  Dvalue = 1.42
  Group = -> [C_element054,H_element048,N_element021,O_element050]
  conduct = 2
  density = 1
  expand = 3
  formula = G4_KAPTON
  name = G4_KAPTON
  specific = 4
FEATURE [App::DocumentObjectGroupPython] La_element001  label="La_element : 1"  # scripted group (container) (typed FeaturePython)
  n = 1
  ref = La_element
FEATURE [App::DocumentObjectGroupPython] Br_element003  label="Br_element : 002"  # scripted group (container) (typed FeaturePython)
  n = 1
  ref = Br_element
FEATURE [App::DocumentObjectGroupPython] O_element051  label="O_element : 026"  # scripted group (container) (typed FeaturePython)
  n = 1
  ref = O_element
FEATURE [App::DocumentObjectGroupPython] G4_LANTHANUM_OXYBROMIDE  # scripted group (container) (typed FeaturePython)
  Dunit = g/cm3
  Dvalue = 6.28
  Group = -> [La_element001,Br_element003,O_element051]
  conduct = 2
  density = 1
  expand = 3
  formula = G4_LANTHANUM_OXYBROMIDE
  name = G4_LANTHANUM_OXYBROMIDE
  specific = 4
FEATURE [App::DocumentObjectGroupPython] La_element002  label="La_element : 2"  # scripted group (container) (typed FeaturePython)
  n = 2
  ref = La_element
FEATURE [App::DocumentObjectGroupPython] O_element052  label="O_element : 027"  # scripted group (container) (typed FeaturePython)
  n = 2
  ref = O_element
FEATURE [App::DocumentObjectGroupPython] S_element015  label="S_element : 006"  # scripted group (container) (typed FeaturePython)
  n = 1
  ref = S_element
FEATURE [App::DocumentObjectGroupPython] G4_LANTHANUM_OXYSULFIDE  # scripted group (container) (typed FeaturePython)
  Dunit = g/cm3
  Dvalue = 5.86
  Group = -> [La_element002,O_element052,S_element015]
  conduct = 2
  density = 1
  expand = 3
  formula = G4_LANTHANUM_OXYSULFIDE
  name = G4_LANTHANUM_OXYSULFIDE
  specific = 4
FEATURE [App::DocumentObjectGroupPython] O_element053  label="O_element : 0.072"  # scripted group (container) (typed FeaturePython)
  n = 0.071682
FEATURE [App::DocumentObjectGroupPython] Pb_element002  label="Pb_element : 0.928"  # scripted group (container) (typed FeaturePython)
  n = 0.928318
FEATURE [App::DocumentObjectGroupPython] G4_LEAD_OXIDE  # scripted group (container) (typed FeaturePython)
  Dunit = g/cm3
  Dvalue = 9.53
  Group = -> [O_element053,Pb_element002]
  conduct = 2
  density = 1
  expand = 3
  formula = G4_LEAD_OXIDE
  name = G4_LEAD_OXIDE
  specific = 4
FEATURE [App::DocumentObjectGroupPython] Li_element001  label="Li_element : 1"  # scripted group (container) (typed FeaturePython)
  n = 1
  ref = Li_element
FEATURE [App::DocumentObjectGroupPython] N_element022  label="N_element : 011"  # scripted group (container) (typed FeaturePython)
  n = 1
  ref = N_element
FEATURE [App::DocumentObjectGroupPython] H_element049  label="H_element : 026"  # scripted group (container) (typed FeaturePython)
  n = 2
  ref = H_element
FEATURE [App::DocumentObjectGroupPython] G4_LITHIUM_AMIDE  # scripted group (container) (typed FeaturePython)
  Dunit = g/cm3
  Dvalue = 1.178
  Group = -> [Li_element001,N_element022,H_element049]
  conduct = 2
  density = 1
  expand = 3
  formula = G4_LITHIUM_AMIDE
  name = G4_LITHIUM_AMIDE
  specific = 4
FEATURE [App::DocumentObjectGroupPython] Li_element002  label="Li_element : 2"  # scripted group (container) (typed FeaturePython)
  n = 2
  ref = Li_element
FEATURE [App::DocumentObjectGroupPython] C_element055  label="C_element : 030"  # scripted group (container) (typed FeaturePython)
  n = 1
  ref = C_element
FEATURE [App::DocumentObjectGroupPython] O_element054  label="O_element : 028"  # scripted group (container) (typed FeaturePython)
  n = 3
  ref = O_element
FEATURE [App::DocumentObjectGroupPython] G4_LITHIUM_CARBONATE  # scripted group (container) (typed FeaturePython)
  Dunit = g/cm3
  Dvalue = 2.11
  Group = -> [Li_element002,C_element055,O_element054]
  conduct = 2
  density = 1
  expand = 3
  formula = G4_LITHIUM_CARBONATE
  name = G4_LITHIUM_CARBONATE
  specific = 4
FEATURE [App::DocumentObjectGroupPython] Li_element003  label="Li_element : 003"  # scripted group (container) (typed FeaturePython)
  n = 1
  ref = Li_element
FEATURE [App::DocumentObjectGroupPython] F_element012  label="F_element : 004"  # scripted group (container) (typed FeaturePython)
  n = 1
  ref = F_element
FEATURE [App::DocumentObjectGroupPython] G4_LITHIUM_FLUORIDE  # scripted group (container) (typed FeaturePython)
  Dunit = g/cm3
  Dvalue = 2.635
  Group = -> [Li_element003,F_element012]
  conduct = 2
  density = 1
  expand = 3
  formula = G4_LITHIUM_FLUORIDE
  name = G4_LITHIUM_FLUORIDE
  specific = 4
FEATURE [App::DocumentObjectGroupPython] Li_element004  label="Li_element : 004"  # scripted group (container) (typed FeaturePython)
  n = 1
  ref = Li_element
FEATURE [App::DocumentObjectGroupPython] H_element050  label="H_element : 027"  # scripted group (container) (typed FeaturePython)
  n = 1
  ref = H_element
FEATURE [App::DocumentObjectGroupPython] G4_LITHIUM_HYDRIDE  # scripted group (container) (typed FeaturePython)
  Dunit = g/cm3
  Dvalue = 0.82
  Group = -> [Li_element004,H_element050]
  conduct = 2
  density = 1
  expand = 3
  formula = G4_LITHIUM_HYDRIDE
  name = G4_LITHIUM_HYDRIDE
  specific = 4
FEATURE [App::DocumentObjectGroupPython] Li_element005  label="Li_element : 005"  # scripted group (container) (typed FeaturePython)
  n = 1
  ref = Li_element
FEATURE [App::DocumentObjectGroupPython] I_element003  label="I_element : 002"  # scripted group (container) (typed FeaturePython)
  n = 1
  ref = I_element
FEATURE [App::DocumentObjectGroupPython] G4_LITHIUM_IODIDE  # scripted group (container) (typed FeaturePython)
  Dunit = g/cm3
  Dvalue = 3.494
  Group = -> [Li_element005,I_element003]
  conduct = 2
  density = 1
  expand = 3
  formula = G4_LITHIUM_IODIDE
  name = G4_LITHIUM_IODIDE
  specific = 4
FEATURE [App::DocumentObjectGroupPython] Li_element006  label="Li_element : 006"  # scripted group (container) (typed FeaturePython)
  n = 2
  ref = Li_element
FEATURE [App::DocumentObjectGroupPython] O_element055  label="O_element : 029"  # scripted group (container) (typed FeaturePython)
  n = 1
  ref = O_element
FEATURE [App::DocumentObjectGroupPython] G4_LITHIUM_OXIDE  # scripted group (container) (typed FeaturePython)
  Dunit = g/cm3
  Dvalue = 2.013
  Group = -> [Li_element006,O_element055]
  conduct = 2
  density = 1
  expand = 3
  formula = G4_LITHIUM_OXIDE
  name = G4_LITHIUM_OXIDE
  specific = 4
FEATURE [App::DocumentObjectGroupPython] Li_element007  label="Li_element : 007"  # scripted group (container) (typed FeaturePython)
  n = 2
  ref = Li_element
FEATURE [App::DocumentObjectGroupPython] B_element005  label="B_element : 005"  # scripted group (container) (typed FeaturePython)
  n = 4
  ref = B_element
FEATURE [App::DocumentObjectGroupPython] O_element056  label="O_element : 7"  # scripted group (container) (typed FeaturePython)
  n = 7
  ref = O_element
FEATURE [App::DocumentObjectGroupPython] G4_LITHIUM_TETRABORATE  # scripted group (container) (typed FeaturePython)
  Dunit = g/cm3
  Dvalue = 2.44
  Group = -> [Li_element007,B_element005,O_element056]
  conduct = 2
  density = 1
  expand = 3
  formula = G4_LITHIUM_TETRABORATE
  name = G4_LITHIUM_TETRABORATE
  specific = 4
FEATURE [App::DocumentObjectGroupPython] H_element051  label="H_element : 0.105"  # scripted group (container) (typed FeaturePython)
  n = 0.105
FEATURE [App::DocumentObjectGroupPython] C_element056  label="C_element : 0.083"  # scripted group (container) (typed FeaturePython)
  n = 0.083
FEATURE [App::DocumentObjectGroupPython] N_element023  label="N_element : 0.023"  # scripted group (container) (typed FeaturePython)
  n = 0.023
FEATURE [App::DocumentObjectGroupPython] O_element057  label="O_element : 0.779"  # scripted group (container) (typed FeaturePython)
  n = 0.779
FEATURE [App::DocumentObjectGroupPython] Na_element010  label="Na_element : 0.097"  # scripted group (container) (typed FeaturePython)
  n = 0.002
FEATURE [App::DocumentObjectGroupPython] P_element006  label="P_element : 0.105"  # scripted group (container) (typed FeaturePython)
  n = 0.001
FEATURE [App::DocumentObjectGroupPython] S_element016  label="S_element : 0.017"  # scripted group (container) (typed FeaturePython)
  n = 0.002
FEATURE [App::DocumentObjectGroupPython] Cl_element014  label="Cl_element : 0.587"  # scripted group (container) (typed FeaturePython)
  n = 0.003
FEATURE [App::DocumentObjectGroupPython] K_element005  label="K_element : 0.015"  # scripted group (container) (typed FeaturePython)
  n = 0.002
FEATURE [App::DocumentObjectGroupPython] G4_LUNG_ICRP  # scripted group (container) (typed FeaturePython)
  Dunit = g/cm3
  Dvalue = 1.04
  Group = -> [H_element051,C_element056,N_element023,O_element057,Na_element010,P_element006,S_element016,Cl_element014,K_element005]
  conduct = 2
  density = 1
  expand = 3
  formula = G4_LUNG_ICRP
  name = G4_LUNG_ICRP
  specific = 4
FEATURE [App::DocumentObjectGroupPython] H_element052  label="H_element : 0.116"  # scripted group (container) (typed FeaturePython)
  n = 0.114318
FEATURE [App::DocumentObjectGroupPython] C_element057  label="C_element : 0.656"  # scripted group (container) (typed FeaturePython)
  n = 0.655824
FEATURE [App::DocumentObjectGroupPython] O_element058  label="O_element : 0.092"  # scripted group (container) (typed FeaturePython)
  n = 0.0921831
FEATURE [App::DocumentObjectGroupPython] Mg_element004  label="Mg_element : 0.135"  # scripted group (container) (typed FeaturePython)
  n = 0.134792
FEATURE [App::DocumentObjectGroupPython] Ca_element013  label="Ca_element : 0.003"  # scripted group (container) (typed FeaturePython)
  n = 0.002883
FEATURE [App::DocumentObjectGroupPython] G4_M3_WAX  # scripted group (container) (typed FeaturePython)
  Dunit = g/cm3
  Dvalue = 1.05
  Group = -> [H_element052,C_element057,O_element058,Mg_element004,Ca_element013]
  conduct = 2
  density = 1
  expand = 3
  formula = G4_M3_WAX
  name = G4_M3_WAX
  specific = 4
FEATURE [App::DocumentObjectGroupPython] Mg_element005  label="Mg_element : 1"  # scripted group (container) (typed FeaturePython)
  n = 1
  ref = Mg_element
FEATURE [App::DocumentObjectGroupPython] C_element058  label="C_element : 031"  # scripted group (container) (typed FeaturePython)
  n = 1
  ref = C_element
FEATURE [App::DocumentObjectGroupPython] O_element059  label="O_element : 030"  # scripted group (container) (typed FeaturePython)
  n = 3
  ref = O_element
FEATURE [App::DocumentObjectGroupPython] G4_MAGNESIUM_CARBONATE  # scripted group (container) (typed FeaturePython)
  Dunit = g/cm3
  Dvalue = 2.958
  Group = -> [Mg_element005,C_element058,O_element059]
  conduct = 2
  density = 1
  expand = 3
  formula = G4_MAGNESIUM_CARBONATE
  name = G4_MAGNESIUM_CARBONATE
  specific = 4
FEATURE [App::DocumentObjectGroupPython] Mg_element006  label="Mg_element : 002"  # scripted group (container) (typed FeaturePython)
  n = 1
  ref = Mg_element
FEATURE [App::DocumentObjectGroupPython] F_element013  label="F_element : 005"  # scripted group (container) (typed FeaturePython)
  n = 2
  ref = F_element
FEATURE [App::DocumentObjectGroupPython] G4_MAGNESIUM_FLUORIDE  # scripted group (container) (typed FeaturePython)
  Dunit = g/cm3
  Dvalue = 3
  Group = -> [Mg_element006,F_element013]
  conduct = 2
  density = 1
  expand = 3
  formula = G4_MAGNESIUM_FLUORIDE
  name = G4_MAGNESIUM_FLUORIDE
  specific = 4
FEATURE [App::DocumentObjectGroupPython] Mg_element007  label="Mg_element : 003"  # scripted group (container) (typed FeaturePython)
  n = 1
  ref = Mg_element
FEATURE [App::DocumentObjectGroupPython] O_element060  label="O_element : 031"  # scripted group (container) (typed FeaturePython)
  n = 1
  ref = O_element
FEATURE [App::DocumentObjectGroupPython] G4_MAGNESIUM_OXIDE  # scripted group (container) (typed FeaturePython)
  Dunit = g/cm3
  Dvalue = 3.58
  Group = -> [Mg_element007,O_element060]
  conduct = 2
  density = 1
  expand = 3
  formula = G4_MAGNESIUM_OXIDE
  name = G4_MAGNESIUM_OXIDE
  specific = 4
FEATURE [App::DocumentObjectGroupPython] Mg_element008  label="Mg_element : 004"  # scripted group (container) (typed FeaturePython)
  n = 1
  ref = Mg_element
FEATURE [App::DocumentObjectGroupPython] B_element006  label="B_element : 006"  # scripted group (container) (typed FeaturePython)
  n = 4
  ref = B_element
FEATURE [App::DocumentObjectGroupPython] O_element061  label="O_element : 032"  # scripted group (container) (typed FeaturePython)
  n = 7
  ref = O_element
FEATURE [App::DocumentObjectGroupPython] G4_MAGNESIUM_TETRABORATE  # scripted group (container) (typed FeaturePython)
  Dunit = g/cm3
  Dvalue = 2.53
  Group = -> [Mg_element008,B_element006,O_element061]
  conduct = 2
  density = 1
  expand = 3
  formula = G4_MAGNESIUM_TETRABORATE
  name = G4_MAGNESIUM_TETRABORATE
  specific = 4
FEATURE [App::DocumentObjectGroupPython] Hg_element001  label="Hg_element : 1"  # scripted group (container) (typed FeaturePython)
  n = 1
  ref = Hg_element
FEATURE [App::DocumentObjectGroupPython] I_element004  label="I_element : 2"  # scripted group (container) (typed FeaturePython)
  n = 2
  ref = I_element
FEATURE [App::DocumentObjectGroupPython] G4_MERCURIC_IODIDE  # scripted group (container) (typed FeaturePython)
  Dunit = g/cm3
  Dvalue = 6.36
  Group = -> [Hg_element001,I_element004]
  conduct = 2
  density = 1
  expand = 3
  formula = G4_MERCURIC_IODIDE
  name = G4_MERCURIC_IODIDE
  specific = 4
FEATURE [App::DocumentObjectGroupPython] C_element059  label="C_element : 032"  # scripted group (container) (typed FeaturePython)
  n = 1
  ref = C_element
FEATURE [App::DocumentObjectGroupPython] H_element053  label="H_element : 028"  # scripted group (container) (typed FeaturePython)
  n = 4
  ref = H_element
FEATURE [App::DocumentObjectGroupPython] G4_METHANE  # scripted group (container) (typed FeaturePython)
  Dunit = g/cm3
  Dvalue = 0.000667151
  Group = -> [C_element059,H_element053]
  conduct = 2
  density = 1
  expand = 3
  formula = G4_METHANE
  name = G4_METHANE
  specific = 4
FEATURE [App::DocumentObjectGroupPython] C_element060  label="C_element : 033"  # scripted group (container) (typed FeaturePython)
  n = 1
  ref = C_element
FEATURE [App::DocumentObjectGroupPython] H_element054  label="H_element : 029"  # scripted group (container) (typed FeaturePython)
  n = 4
  ref = H_element
FEATURE [App::DocumentObjectGroupPython] O_element062  label="O_element : 033"  # scripted group (container) (typed FeaturePython)
  n = 1
  ref = O_element
FEATURE [App::DocumentObjectGroupPython] G4_METHANOL  # scripted group (container) (typed FeaturePython)
  Dunit = g/cm3
  Dvalue = 0.7914
  Group = -> [C_element060,H_element054,O_element062]
  conduct = 2
  density = 1
  expand = 3
  formula = G4_METHANOL
  name = G4_METHANOL
  specific = 4
FEATURE [App::DocumentObjectGroupPython] H_element055  label="H_element : 0.134"  # scripted group (container) (typed FeaturePython)
  n = 0.13404
FEATURE [App::DocumentObjectGroupPython] C_element061  label="C_element : 0.778"  # scripted group (container) (typed FeaturePython)
  n = 0.77796
FEATURE [App::DocumentObjectGroupPython] O_element063  label="O_element : 0.035"  # scripted group (container) (typed FeaturePython)
  n = 0.03502
FEATURE [App::DocumentObjectGroupPython] Mg_element009  label="Mg_element : 0.039"  # scripted group (container) (typed FeaturePython)
  n = 0.038594
FEATURE [App::DocumentObjectGroupPython] Ti_element002  label="Ti_element : 0.014"  # scripted group (container) (typed FeaturePython)
  n = 0.014386
FEATURE [App::DocumentObjectGroupPython] G4_MIX_D_WAX  # scripted group (container) (typed FeaturePython)
  Dunit = g/cm3
  Dvalue = 0.99
  Group = -> [H_element055,C_element061,O_element063,Mg_element009,Ti_element002]
  conduct = 2
  density = 1
  expand = 3
  formula = G4_MIX_D_WAX
  name = G4_MIX_D_WAX
  specific = 4
FEATURE [App::DocumentObjectGroupPython] H_element056  label="H_element : 0.135"  # scripted group (container) (typed FeaturePython)
  n = 0.081192
FEATURE [App::DocumentObjectGroupPython] C_element062  label="C_element : 0.583"  # scripted group (container) (typed FeaturePython)
  n = 0.583442
FEATURE [App::DocumentObjectGroupPython] N_element024  label="N_element : 0.018"  # scripted group (container) (typed FeaturePython)
  n = 0.017798
FEATURE [App::DocumentObjectGroupPython] O_element064  label="O_element : 0.186"  # scripted group (container) (typed FeaturePython)
  n = 0.186381
FEATURE [App::DocumentObjectGroupPython] Mg_element010  label="Mg_element : 0.130"  # scripted group (container) (typed FeaturePython)
  n = 0.130287
FEATURE [App::DocumentObjectGroupPython] Cl_element015  label="Cl_element : 0.588"  # scripted group (container) (typed FeaturePython)
  n = 0.0009
FEATURE [App::DocumentObjectGroupPython] G4_MS20_TISSUE  # scripted group (container) (typed FeaturePython)
  Dunit = g/cm3
  Dvalue = 1
  Group = -> [H_element056,C_element062,N_element024,O_element064,Mg_element010,Cl_element015]
  conduct = 2
  density = 1
  expand = 3
  formula = G4_MS20_TISSUE
  name = G4_MS20_TISSUE
  specific = 4
FEATURE [App::DocumentObjectGroupPython] H_element057  label="H_element : 0.136"  # scripted group (container) (typed FeaturePython)
  n = 0.102
FEATURE [App::DocumentObjectGroupPython] C_element063  label="C_element : 0.143"  # scripted group (container) (typed FeaturePython)
  n = 0.143
FEATURE [App::DocumentObjectGroupPython] N_element025  label="N_element : 0.034"  # scripted group (container) (typed FeaturePython)
  n = 0.034
FEATURE [App::DocumentObjectGroupPython] O_element065  label="O_element : 0.710"  # scripted group (container) (typed FeaturePython)
  n = 0.71
FEATURE [App::DocumentObjectGroupPython] Na_element011  label="Na_element : 0.098"  # scripted group (container) (typed FeaturePython)
  n = 0.001
FEATURE [App::DocumentObjectGroupPython] P_element007  label="P_element : 0.002"  # scripted group (container) (typed FeaturePython)
  n = 0.002
FEATURE [App::DocumentObjectGroupPython] S_element017  label="S_element : 0.018"  # scripted group (container) (typed FeaturePython)
  n = 0.003
FEATURE [App::DocumentObjectGroupPython] Cl_element016  label="Cl_element : 0.589"  # scripted group (container) (typed FeaturePython)
  n = 0.001
FEATURE [App::DocumentObjectGroupPython] K_element006  label="K_element : 0.004"  # scripted group (container) (typed FeaturePython)
  n = 0.004
FEATURE [App::DocumentObjectGroupPython] G4_MUSCLE_SKELETAL_ICRP  # scripted group (container) (typed FeaturePython)
  Dunit = g/cm3
  Dvalue = 1.05
  Group = -> [H_element057,C_element063,N_element025,O_element065,Na_element011,P_element007,S_element017,Cl_element016,K_element006]
  conduct = 2
  density = 1
  expand = 3
  formula = G4_MUSCLE_SKELETAL_ICRP
  name = G4_MUSCLE_SKELETAL_ICRP
  specific = 4
FEATURE [App::DocumentObjectGroupPython] H_element058  label="H_element : 0.137"  # scripted group (container) (typed FeaturePython)
  n = 0.102102
FEATURE [App::DocumentObjectGroupPython] C_element064  label="C_element : 0.123"  # scripted group (container) (typed FeaturePython)
  n = 0.123123
FEATURE [App::DocumentObjectGroupPython] N_element026  label="N_element : 0.756"  # scripted group (container) (typed FeaturePython)
  n = 0.035035
FEATURE [App::DocumentObjectGroupPython] O_element066  label="O_element : 0.730"  # scripted group (container) (typed FeaturePython)
  n = 0.72973
FEATURE [App::DocumentObjectGroupPython] Na_element012  label="Na_element : 0.099"  # scripted group (container) (typed FeaturePython)
  n = 0.001001
FEATURE [App::DocumentObjectGroupPython] P_element008  label="P_element : 0.106"  # scripted group (container) (typed FeaturePython)
  n = 0.002002
FEATURE [App::DocumentObjectGroupPython] S_element018  label="S_element : 0.019"  # scripted group (container) (typed FeaturePython)
  n = 0.004004
FEATURE [App::DocumentObjectGroupPython] K_element007  label="K_element : 0.016"  # scripted group (container) (typed FeaturePython)
  n = 0.003003
FEATURE [App::DocumentObjectGroupPython] G4_MUSCLE_STRIATED_ICRU  # scripted group (container) (typed FeaturePython)
  Dunit = g/cm3
  Dvalue = 1.04
  Group = -> [H_element058,C_element064,N_element026,O_element066,Na_element012,P_element008,S_element018,K_element007]
  conduct = 2
  density = 1
  expand = 3
  formula = G4_MUSCLE_STRIATED_ICRU
  name = G4_MUSCLE_STRIATED_ICRU
  specific = 4
FEATURE [App::DocumentObjectGroupPython] H_element059  label="H_element : 0.098"  # scripted group (container) (typed FeaturePython)
  n = 0.0982341
FEATURE [App::DocumentObjectGroupPython] C_element065  label="C_element : 0.156"  # scripted group (container) (typed FeaturePython)
  n = 0.156214
FEATURE [App::DocumentObjectGroupPython] N_element027  label="N_element : 0.757"  # scripted group (container) (typed FeaturePython)
  n = 0.035451
FEATURE [App::DocumentObjectGroupPython] O_element067  label="O_element : 0.880"  # scripted group (container) (typed FeaturePython)
  n = 0.710101
FEATURE [App::DocumentObjectGroupPython] G4_MUSCLE_WITH_SUCROSE  # scripted group (container) (typed FeaturePython)
  Dunit = g/cm3
  Dvalue = 1.11
  Group = -> [H_element059,C_element065,N_element027,O_element067]
  conduct = 2
  density = 1
  expand = 3
  formula = G4_MUSCLE_WITH_SUCROSE
  name = G4_MUSCLE_WITH_SUCROSE
  specific = 4
FEATURE [App::DocumentObjectGroupPython] H_element060  label="H_element : 0.138"  # scripted group (container) (typed FeaturePython)
  n = 0.101969
FEATURE [App::DocumentObjectGroupPython] C_element066  label="C_element : 0.120"  # scripted group (container) (typed FeaturePython)
  n = 0.120058
FEATURE [App::DocumentObjectGroupPython] N_element028  label="N_element : 0.758"  # scripted group (container) (typed FeaturePython)
  n = 0.035451
FEATURE [App::DocumentObjectGroupPython] O_element068  label="O_element : 0.743"  # scripted group (container) (typed FeaturePython)
  n = 0.742522
FEATURE [App::DocumentObjectGroupPython] G4_MUSCLE_WITHOUT_SUCROSE  # scripted group (container) (typed FeaturePython)
  Dunit = g/cm3
  Dvalue = 1.07
  Group = -> [H_element060,C_element066,N_element028,O_element068]
  conduct = 2
  density = 1
  expand = 3
  formula = G4_MUSCLE_WITHOUT_SUCROSE
  name = G4_MUSCLE_WITHOUT_SUCROSE
  specific = 4
FEATURE [App::DocumentObjectGroupPython] C_element067  label="C_element : 10"  # scripted group (container) (typed FeaturePython)
  n = 10
  ref = C_element
FEATURE [App::DocumentObjectGroupPython] H_element061  label="H_element : 030"  # scripted group (container) (typed FeaturePython)
  n = 8
  ref = H_element
FEATURE [App::DocumentObjectGroupPython] G4_NAPHTHALENE  # scripted group (container) (typed FeaturePython)
  Dunit = g/cm3
  Dvalue = 1.145
  Group = -> [C_element067,H_element061]
  conduct = 2
  density = 1
  expand = 3
  formula = G4_NAPHTHALENE
  name = G4_NAPHTHALENE
  specific = 4
FEATURE [App::DocumentObjectGroupPython] C_element068  label="C_element : 034"  # scripted group (container) (typed FeaturePython)
  n = 6
  ref = C_element
FEATURE [App::DocumentObjectGroupPython] H_element062  label="H_element : 031"  # scripted group (container) (typed FeaturePython)
  n = 5
  ref = H_element
FEATURE [App::DocumentObjectGroupPython] N_element029  label="N_element : 012"  # scripted group (container) (typed FeaturePython)
  n = 1
  ref = N_element
FEATURE [App::DocumentObjectGroupPython] O_element069  label="O_element : 034"  # scripted group (container) (typed FeaturePython)
  n = 2
  ref = O_element
FEATURE [App::DocumentObjectGroupPython] G4_NITROBENZENE  # scripted group (container) (typed FeaturePython)
  Dunit = g/cm3
  Dvalue = 1.19867
  Group = -> [C_element068,H_element062,N_element029,O_element069]
  conduct = 2
  density = 1
  expand = 3
  formula = G4_NITROBENZENE
  name = G4_NITROBENZENE
  specific = 4
FEATURE [App::DocumentObjectGroupPython] N_element030  label="N_element : 013"  # scripted group (container) (typed FeaturePython)
  n = 2
  ref = N_element
FEATURE [App::DocumentObjectGroupPython] O_element070  label="O_element : 035"  # scripted group (container) (typed FeaturePython)
  n = 1
  ref = O_element
FEATURE [App::DocumentObjectGroupPython] G4_NITROUS_OXIDE  # scripted group (container) (typed FeaturePython)
  Dunit = g/cm3
  Dvalue = 0.00183094
  Group = -> [N_element030,O_element070]
  conduct = 2
  density = 1
  expand = 3
  formula = G4_NITROUS_OXIDE
  name = G4_NITROUS_OXIDE
  specific = 4
FEATURE [App::DocumentObjectGroupPython] H_element063  label="H_element : 0.104"  # scripted group (container) (typed FeaturePython)
  n = 0.103509
FEATURE [App::DocumentObjectGroupPython] C_element069  label="C_element : 0.648"  # scripted group (container) (typed FeaturePython)
  n = 0.648416
FEATURE [App::DocumentObjectGroupPython] N_element031  label="N_element : 0.100"  # scripted group (container) (typed FeaturePython)
  n = 0.0995361
FEATURE [App::DocumentObjectGroupPython] O_element071  label="O_element : 0.149"  # scripted group (container) (typed FeaturePython)
  n = 0.148539
FEATURE [App::DocumentObjectGroupPython] G4_NYLON_8062  label="G4_NYLON-8062"  # scripted group (container) (typed FeaturePython)
  Dunit = g/cm3
  Dvalue = 1.08
  Group = -> [H_element063,C_element069,N_element031,O_element071]
  conduct = 2
  density = 1
  expand = 3
  formula = G4_NYLON-8062
  name = G4_NYLON-8062
  specific = 4
FEATURE [App::DocumentObjectGroupPython] C_element070  label="C_element : 035"  # scripted group (container) (typed FeaturePython)
  n = 6
  ref = C_element
FEATURE [App::DocumentObjectGroupPython] H_element064  label="H_element : 11"  # scripted group (container) (typed FeaturePython)
  n = 11
  ref = H_element
FEATURE [App::DocumentObjectGroupPython] N_element032  label="N_element : 014"  # scripted group (container) (typed FeaturePython)
  n = 1
  ref = N_element
FEATURE [App::DocumentObjectGroupPython] O_element072  label="O_element : 036"  # scripted group (container) (typed FeaturePython)
  n = 1
  ref = O_element
FEATURE [App::DocumentObjectGroupPython] G4_NYLON_6_6  label="G4_NYLON-6-6"  # scripted group (container) (typed FeaturePython)
  Dunit = g/cm3
  Dvalue = 1.14
  Group = -> [C_element070,H_element064,N_element032,O_element072]
  conduct = 2
  density = 1
  expand = 3
  formula = G4_NYLON-6-6
  name = G4_NYLON-6-6
  specific = 4
FEATURE [App::DocumentObjectGroupPython] H_element065  label="H_element : 0.139"  # scripted group (container) (typed FeaturePython)
  n = 0.107062
FEATURE [App::DocumentObjectGroupPython] C_element071  label="C_element : 0.680"  # scripted group (container) (typed FeaturePython)
  n = 0.680449
FEATURE [App::DocumentObjectGroupPython] N_element033  label="N_element : 0.099"  # scripted group (container) (typed FeaturePython)
  n = 0.099189
FEATURE [App::DocumentObjectGroupPython] O_element073  label="O_element : 0.113"  # scripted group (container) (typed FeaturePython)
  n = 0.1133
FEATURE [App::DocumentObjectGroupPython] G4_NYLON_6_10  label="G4_NYLON-6-10"  # scripted group (container) (typed FeaturePython)
  Dunit = g/cm3
  Dvalue = 1.14
  Group = -> [H_element065,C_element071,N_element033,O_element073]
  conduct = 2
  density = 1
  expand = 3
  formula = G4_NYLON-6-10
  name = G4_NYLON-6-10
  specific = 4
FEATURE [App::DocumentObjectGroupPython] H_element066  label="H_element : 0.140"  # scripted group (container) (typed FeaturePython)
  n = 0.115476
FEATURE [App::DocumentObjectGroupPython] C_element072  label="C_element : 0.721"  # scripted group (container) (typed FeaturePython)
  n = 0.720818
FEATURE [App::DocumentObjectGroupPython] N_element034  label="N_element : 0.076"  # scripted group (container) (typed FeaturePython)
  n = 0.0764169
FEATURE [App::DocumentObjectGroupPython] O_element074  label="O_element : 0.087"  # scripted group (container) (typed FeaturePython)
  n = 0.0872889
FEATURE [App::DocumentObjectGroupPython] G4_NYLON_11_RILSAN  label="G4_NYLON-11_RILSAN"  # scripted group (container) (typed FeaturePython)
  Dunit = g/cm3
  Dvalue = 1.425
  Group = -> [H_element066,C_element072,N_element034,O_element074]
  conduct = 2
  density = 1
  expand = 3
  formula = G4_NYLON-11_RILSAN
  name = G4_NYLON-11_RILSAN
  specific = 4
FEATURE [App::DocumentObjectGroupPython] C_element073  label="C_element : 8"  # scripted group (container) (typed FeaturePython)
  n = 8
  ref = C_element
FEATURE [App::DocumentObjectGroupPython] H_element067  label="H_element : 18"  # scripted group (container) (typed FeaturePython)
  n = 18
  ref = H_element
FEATURE [App::DocumentObjectGroupPython] G4_OCTANE  # scripted group (container) (typed FeaturePython)
  Dunit = g/cm3
  Dvalue = 0.7026
  Group = -> [C_element073,H_element067]
  conduct = 2
  density = 1
  expand = 3
  formula = G4_OCTANE
  name = G4_OCTANE
  specific = 4
FEATURE [App::DocumentObjectGroupPython] C_element074  label="C_element : 25"  # scripted group (container) (typed FeaturePython)
  n = 25
  ref = C_element
FEATURE [App::DocumentObjectGroupPython] H_element068  label="H_element : 52"  # scripted group (container) (typed FeaturePython)
  n = 52
  ref = H_element
FEATURE [App::DocumentObjectGroupPython] G4_PARAFFIN  # scripted group (container) (typed FeaturePython)
  Dunit = g/cm3
  Dvalue = 0.93
  Group = -> [C_element074,H_element068]
  conduct = 2
  density = 1
  expand = 3
  formula = G4_PARAFFIN
  name = G4_PARAFFIN
  specific = 4
FEATURE [App::DocumentObjectGroupPython] C_element075  label="C_element : 036"  # scripted group (container) (typed FeaturePython)
  n = 5
  ref = C_element
FEATURE [App::DocumentObjectGroupPython] H_element069  label="H_element : 032"  # scripted group (container) (typed FeaturePython)
  n = 12
  ref = H_element
FEATURE [App::DocumentObjectGroupPython] G4_N_PENTANE  label="G4_N-PENTANE"  # scripted group (container) (typed FeaturePython)
  Dunit = g/cm3
  Dvalue = 0.6262
  Group = -> [C_element075,H_element069]
  conduct = 2
  density = 1
  expand = 3
  formula = G4_N-PENTANE
  name = G4_N-PENTANE
  specific = 4
FEATURE [App::DocumentObjectGroupPython] H_element070  label="H_element : 0.014"  # scripted group (container) (typed FeaturePython)
  n = 0.0141
FEATURE [App::DocumentObjectGroupPython] C_element076  label="C_element : 0.072"  # scripted group (container) (typed FeaturePython)
  n = 0.072261
FEATURE [App::DocumentObjectGroupPython] N_element035  label="N_element : 0.019"  # scripted group (container) (typed FeaturePython)
  n = 0.01932
FEATURE [App::DocumentObjectGroupPython] O_element075  label="O_element : 0.066"  # scripted group (container) (typed FeaturePython)
  n = 0.066101
FEATURE [App::DocumentObjectGroupPython] S_element019  label="S_element : 0.020"  # scripted group (container) (typed FeaturePython)
  n = 0.00189
FEATURE [App::DocumentObjectGroupPython] Br_element004  label="Br_element : 0.349"  # scripted group (container) (typed FeaturePython)
  n = 0.349103
FEATURE [App::DocumentObjectGroupPython] Ag_element001  label="Ag_element : 0.474"  # scripted group (container) (typed FeaturePython)
  n = 0.474105
FEATURE [App::DocumentObjectGroupPython] I_element005  label="I_element : 0.003"  # scripted group (container) (typed FeaturePython)
  n = 0.00312
FEATURE [App::DocumentObjectGroupPython] G4_PHOTO_EMULSION  # scripted group (container) (typed FeaturePython)
  Dunit = g/cm3
  Dvalue = 3.815
  Group = -> [H_element070,C_element076,N_element035,O_element075,S_element019,Br_element004,Ag_element001,I_element005]
  conduct = 2
  density = 1
  expand = 3
  formula = G4_PHOTO_EMULSION
  name = G4_PHOTO_EMULSION
  specific = 4
FEATURE [App::DocumentObjectGroupPython] C_element077  label="C_element : 9"  # scripted group (container) (typed FeaturePython)
  n = 9
  ref = C_element
FEATURE [App::DocumentObjectGroupPython] H_element071  label="H_element : 033"  # scripted group (container) (typed FeaturePython)
  n = 10
  ref = H_element
FEATURE [App::DocumentObjectGroupPython] G4_PLASTIC_SC_VINYLTOLUENE  # scripted group (container) (typed FeaturePython)
  Dunit = g/cm3
  Dvalue = 1.032
  Group = -> [C_element077,H_element071]
  conduct = 2
  density = 1
  expand = 3
  formula = G4_PLASTIC_SC_VINYLTOLUENE
  name = G4_PLASTIC_SC_VINYLTOLUENE
  specific = 4
FEATURE [App::DocumentObjectGroupPython] Pu_element001  label="Pu_element : 1"  # scripted group (container) (typed FeaturePython)
  n = 1
  ref = Pu_element
FEATURE [App::DocumentObjectGroupPython] O_element076  label="O_element : 037"  # scripted group (container) (typed FeaturePython)
  n = 2
  ref = O_element
FEATURE [App::DocumentObjectGroupPython] G4_PLUTONIUM_DIOXIDE  # scripted group (container) (typed FeaturePython)
  Dunit = g/cm3
  Dvalue = 11.46
  Group = -> [Pu_element001,O_element076]
  conduct = 2
  density = 1
  expand = 3
  formula = G4_PLUTONIUM_DIOXIDE
  name = G4_PLUTONIUM_DIOXIDE
  specific = 4
FEATURE [App::DocumentObjectGroupPython] C_element078  label="C_element : 037"  # scripted group (container) (typed FeaturePython)
  n = 3
  ref = C_element
FEATURE [App::DocumentObjectGroupPython] H_element072  label="H_element : 034"  # scripted group (container) (typed FeaturePython)
  n = 3
  ref = H_element
FEATURE [App::DocumentObjectGroupPython] N_element036  label="N_element : 015"  # scripted group (container) (typed FeaturePython)
  n = 1
  ref = N_element
FEATURE [App::DocumentObjectGroupPython] G4_POLYACRYLONITRILE  # scripted group (container) (typed FeaturePython)
  Dunit = g/cm3
  Dvalue = 1.17
  Group = -> [C_element078,H_element072,N_element036]
  conduct = 2
  density = 1
  expand = 3
  formula = G4_POLYACRYLONITRILE
  name = G4_POLYACRYLONITRILE
  specific = 4
FEATURE [App::DocumentObjectGroupPython] C_element079  label="C_element : 16"  # scripted group (container) (typed FeaturePython)
  n = 16
  ref = C_element
FEATURE [App::DocumentObjectGroupPython] H_element073  label="H_element : 035"  # scripted group (container) (typed FeaturePython)
  n = 14
  ref = H_element
FEATURE [App::DocumentObjectGroupPython] O_element077  label="O_element : 038"  # scripted group (container) (typed FeaturePython)
  n = 3
  ref = O_element
FEATURE [App::DocumentObjectGroupPython] G4_POLYCARBONATE  # scripted group (container) (typed FeaturePython)
  Dunit = g/cm3
  Dvalue = 1.2
  Group = -> [C_element079,H_element073,O_element077]
  conduct = 2
  density = 1
  expand = 3
  formula = G4_POLYCARBONATE
  name = G4_POLYCARBONATE
  specific = 4
FEATURE [App::DocumentObjectGroupPython] C_element080  label="C_element : 038"  # scripted group (container) (typed FeaturePython)
  n = 8
  ref = C_element
FEATURE [App::DocumentObjectGroupPython] H_element074  label="H_element : 036"  # scripted group (container) (typed FeaturePython)
  n = 7
  ref = H_element
FEATURE [App::DocumentObjectGroupPython] Cl_element017  label="Cl_element : 007"  # scripted group (container) (typed FeaturePython)
  n = 1
  ref = Cl_element
FEATURE [App::DocumentObjectGroupPython] G4_POLYCHLOROSTYRENE  # scripted group (container) (typed FeaturePython)
  Dunit = g/cm3
  Dvalue = 1.3
  Group = -> [C_element080,H_element074,Cl_element017]
  conduct = 2
  density = 1
  expand = 3
  formula = G4_POLYCHLOROSTYRENE
  name = G4_POLYCHLOROSTYRENE
  specific = 4
FEATURE [App::DocumentObjectGroupPython] C_element081  label="C_element : 039"  # scripted group (container) (typed FeaturePython)
  n = 1
  ref = C_element
FEATURE [App::DocumentObjectGroupPython] H_element075  label="H_element : 037"  # scripted group (container) (typed FeaturePython)
  n = 2
  ref = H_element
FEATURE [App::DocumentObjectGroupPython] G4_POLYETHYLENE  # scripted group (container) (typed FeaturePython)
  Dunit = g/cm3
  Dvalue = 0.94
  Group = -> [C_element081,H_element075]
  conduct = 2
  density = 1
  expand = 3
  formula = G4_POLYETHYLENE
  name = G4_POLYETHYLENE
  specific = 4
FEATURE [App::DocumentObjectGroupPython] C_element082  label="C_element : 040"  # scripted group (container) (typed FeaturePython)
  n = 10
  ref = C_element
FEATURE [App::DocumentObjectGroupPython] H_element076  label="H_element : 038"  # scripted group (container) (typed FeaturePython)
  n = 8
  ref = H_element
FEATURE [App::DocumentObjectGroupPython] O_element078  label="O_element : 039"  # scripted group (container) (typed FeaturePython)
  n = 4
  ref = O_element
FEATURE [App::DocumentObjectGroupPython] G4_MYLAR  # scripted group (container) (typed FeaturePython)
  Dunit = g/cm3
  Dvalue = 1.4
  Group = -> [C_element082,H_element076,O_element078]
  conduct = 2
  density = 1
  expand = 3
  formula = G4_MYLAR
  name = G4_MYLAR
  specific = 4
FEATURE [App::DocumentObjectGroupPython] C_element083  label="C_element : 041"  # scripted group (container) (typed FeaturePython)
  n = 5
  ref = C_element
FEATURE [App::DocumentObjectGroupPython] H_element077  label="H_element : 039"  # scripted group (container) (typed FeaturePython)
  n = 8
  ref = H_element
FEATURE [App::DocumentObjectGroupPython] O_element079  label="O_element : 040"  # scripted group (container) (typed FeaturePython)
  n = 2
  ref = O_element
FEATURE [App::DocumentObjectGroupPython] G4_PLEXIGLASS  # scripted group (container) (typed FeaturePython)
  Dunit = g/cm3
  Dvalue = 1.19
  Group = -> [C_element083,H_element077,O_element079]
  conduct = 2
  density = 1
  expand = 3
  formula = G4_PLEXIGLASS
  name = G4_PLEXIGLASS
  specific = 4
FEATURE [App::DocumentObjectGroupPython] C_element084  label="C_element : 042"  # scripted group (container) (typed FeaturePython)
  n = 1
  ref = C_element
FEATURE [App::DocumentObjectGroupPython] H_element078  label="H_element : 040"  # scripted group (container) (typed FeaturePython)
  n = 2
  ref = H_element
FEATURE [App::DocumentObjectGroupPython] O_element080  label="O_element : 041"  # scripted group (container) (typed FeaturePython)
  n = 1
  ref = O_element
FEATURE [App::DocumentObjectGroupPython] G4_POLYOXYMETHYLENE  # scripted group (container) (typed FeaturePython)
  Dunit = g/cm3
  Dvalue = 1.425
  Group = -> [C_element084,H_element078,O_element080]
  conduct = 2
  density = 1
  expand = 3
  formula = G4_POLYOXYMETHYLENE
  name = G4_POLYOXYMETHYLENE
  specific = 4
FEATURE [App::DocumentObjectGroupPython] C_element085  label="C_element : 043"  # scripted group (container) (typed FeaturePython)
  n = 2
  ref = C_element
FEATURE [App::DocumentObjectGroupPython] H_element079  label="H_element : 041"  # scripted group (container) (typed FeaturePython)
  n = 4
  ref = H_element
FEATURE [App::DocumentObjectGroupPython] G4_POLYPROPYLENE  # scripted group (container) (typed FeaturePython)
  Dunit = g/cm3
  Dvalue = 0.9
  Group = -> [C_element085,H_element079]
  conduct = 2
  density = 1
  expand = 3
  formula = G4_POLYPROPYLENE
  name = G4_POLYPROPYLENE
  specific = 4
FEATURE [App::DocumentObjectGroupPython] C_element086  label="C_element : 044"  # scripted group (container) (typed FeaturePython)
  n = 8
  ref = C_element
FEATURE [App::DocumentObjectGroupPython] H_element080  label="H_element : 042"  # scripted group (container) (typed FeaturePython)
  n = 8
  ref = H_element
FEATURE [App::DocumentObjectGroupPython] G4_POLYSTYRENE  # scripted group (container) (typed FeaturePython)
  Dunit = g/cm3
  Dvalue = 1.06
  Group = -> [C_element086,H_element080]
  conduct = 2
  density = 1
  expand = 3
  formula = G4_POLYSTYRENE
  name = G4_POLYSTYRENE
  specific = 4
FEATURE [App::DocumentObjectGroupPython] C_element087  label="C_element : 045"  # scripted group (container) (typed FeaturePython)
  n = 2
  ref = C_element
FEATURE [App::DocumentObjectGroupPython] F_element014  label="F_element : 4"  # scripted group (container) (typed FeaturePython)
  n = 4
  ref = F_element
FEATURE [App::DocumentObjectGroupPython] G4_TEFLON  # scripted group (container) (typed FeaturePython)
  Dunit = g/cm3
  Dvalue = 2.2
  Group = -> [C_element087,F_element014]
  conduct = 2
  density = 1
  expand = 3
  formula = G4_TEFLON
  name = G4_TEFLON
  specific = 4
FEATURE [App::DocumentObjectGroupPython] C_element088  label="C_element : 046"  # scripted group (container) (typed FeaturePython)
  n = 2
  ref = C_element
FEATURE [App::DocumentObjectGroupPython] F_element015  label="F_element : 006"  # scripted group (container) (typed FeaturePython)
  n = 3
  ref = F_element
FEATURE [App::DocumentObjectGroupPython] Cl_element018  label="Cl_element : 008"  # scripted group (container) (typed FeaturePython)
  n = 1
  ref = Cl_element
FEATURE [App::DocumentObjectGroupPython] G4_POLYTRIFLUOROCHLOROETHYLENE  # scripted group (container) (typed FeaturePython)
  Dunit = g/cm3
  Dvalue = 2.1
  Group = -> [C_element088,F_element015,Cl_element018]
  conduct = 2
  density = 1
  expand = 3
  formula = G4_POLYTRIFLUOROCHLOROETHYLENE
  name = G4_POLYTRIFLUOROCHLOROETHYLENE
  specific = 4
FEATURE [App::DocumentObjectGroupPython] C_element089  label="C_element : 047"  # scripted group (container) (typed FeaturePython)
  n = 4
  ref = C_element
FEATURE [App::DocumentObjectGroupPython] H_element081  label="H_element : 043"  # scripted group (container) (typed FeaturePython)
  n = 6
  ref = H_element
FEATURE [App::DocumentObjectGroupPython] O_element081  label="O_element : 042"  # scripted group (container) (typed FeaturePython)
  n = 2
  ref = O_element
FEATURE [App::DocumentObjectGroupPython] G4_POLYVINYL_ACETATE  # scripted group (container) (typed FeaturePython)
  Dunit = g/cm3
  Dvalue = 1.19
  Group = -> [C_element089,H_element081,O_element081]
  conduct = 2
  density = 1
  expand = 3
  formula = G4_POLYVINYL_ACETATE
  name = G4_POLYVINYL_ACETATE
  specific = 4
FEATURE [App::DocumentObjectGroupPython] C_element090  label="C_element : 048"  # scripted group (container) (typed FeaturePython)
  n = 2
  ref = C_element
FEATURE [App::DocumentObjectGroupPython] H_element082  label="H_element : 044"  # scripted group (container) (typed FeaturePython)
  n = 4
  ref = H_element
FEATURE [App::DocumentObjectGroupPython] O_element082  label="O_element : 043"  # scripted group (container) (typed FeaturePython)
  n = 1
  ref = O_element
FEATURE [App::DocumentObjectGroupPython] G4_POLYVINYL_ALCOHOL  # scripted group (container) (typed FeaturePython)
  Dunit = g/cm3
  Dvalue = 1.3
  Group = -> [C_element090,H_element082,O_element082]
  conduct = 2
  density = 1
  expand = 3
  formula = G4_POLYVINYL_ALCOHOL
  name = G4_POLYVINYL_ALCOHOL
  specific = 4
FEATURE [App::DocumentObjectGroupPython] C_element091  label="C_element : 049"  # scripted group (container) (typed FeaturePython)
  n = 8
  ref = C_element
FEATURE [App::DocumentObjectGroupPython] H_element083  label="H_element : 045"  # scripted group (container) (typed FeaturePython)
  n = 14
  ref = H_element
FEATURE [App::DocumentObjectGroupPython] O_element083  label="O_element : 044"  # scripted group (container) (typed FeaturePython)
  n = 2
  ref = O_element
FEATURE [App::DocumentObjectGroupPython] G4_POLYVINYL_BUTYRAL  # scripted group (container) (typed FeaturePython)
  Dunit = g/cm3
  Dvalue = 1.12
  Group = -> [C_element091,H_element083,O_element083]
  conduct = 2
  density = 1
  expand = 3
  formula = G4_POLYVINYL_BUTYRAL
  name = G4_POLYVINYL_BUTYRAL
  specific = 4
FEATURE [App::DocumentObjectGroupPython] C_element092  label="C_element : 050"  # scripted group (container) (typed FeaturePython)
  n = 2
  ref = C_element
FEATURE [App::DocumentObjectGroupPython] H_element084  label="H_element : 046"  # scripted group (container) (typed FeaturePython)
  n = 3
  ref = H_element
FEATURE [App::DocumentObjectGroupPython] Cl_element019  label="Cl_element : 009"  # scripted group (container) (typed FeaturePython)
  n = 1
  ref = Cl_element
FEATURE [App::DocumentObjectGroupPython] G4_POLYVINYL_CHLORIDE  # scripted group (container) (typed FeaturePython)
  Dunit = g/cm3
  Dvalue = 1.3
  Group = -> [C_element092,H_element084,Cl_element019]
  conduct = 2
  density = 1
  expand = 3
  formula = G4_POLYVINYL_CHLORIDE
  name = G4_POLYVINYL_CHLORIDE
  specific = 4
FEATURE [App::DocumentObjectGroupPython] C_element093  label="C_element : 051"  # scripted group (container) (typed FeaturePython)
  n = 2
  ref = C_element
FEATURE [App::DocumentObjectGroupPython] H_element085  label="H_element : 047"  # scripted group (container) (typed FeaturePython)
  n = 2
  ref = H_element
FEATURE [App::DocumentObjectGroupPython] Cl_element020  label="Cl_element : 010"  # scripted group (container) (typed FeaturePython)
  n = 2
  ref = Cl_element
FEATURE [App::DocumentObjectGroupPython] G4_POLYVINYLIDENE_CHLORIDE  # scripted group (container) (typed FeaturePython)
  Dunit = g/cm3
  Dvalue = 1.7
  Group = -> [C_element093,H_element085,Cl_element020]
  conduct = 2
  density = 1
  expand = 3
  formula = G4_POLYVINYLIDENE_CHLORIDE
  name = G4_POLYVINYLIDENE_CHLORIDE
  specific = 4
FEATURE [App::DocumentObjectGroupPython] C_element094  label="C_element : 052"  # scripted group (container) (typed FeaturePython)
  n = 2
  ref = C_element
FEATURE [App::DocumentObjectGroupPython] H_element086  label="H_element : 048"  # scripted group (container) (typed FeaturePython)
  n = 2
  ref = H_element
FEATURE [App::DocumentObjectGroupPython] F_element016  label="F_element : 007"  # scripted group (container) (typed FeaturePython)
  n = 2
  ref = F_element
FEATURE [App::DocumentObjectGroupPython] G4_POLYVINYLIDENE_FLUORIDE  # scripted group (container) (typed FeaturePython)
  Dunit = g/cm3
  Dvalue = 1.76
  Group = -> [C_element094,H_element086,F_element016]
  conduct = 2
  density = 1
  expand = 3
  formula = G4_POLYVINYLIDENE_FLUORIDE
  name = G4_POLYVINYLIDENE_FLUORIDE
  specific = 4
FEATURE [App::DocumentObjectGroupPython] C_element095  label="C_element : 053"  # scripted group (container) (typed FeaturePython)
  n = 6
  ref = C_element
FEATURE [App::DocumentObjectGroupPython] H_element087  label="H_element : 9"  # scripted group (container) (typed FeaturePython)
  n = 9
  ref = H_element
FEATURE [App::DocumentObjectGroupPython] N_element037  label="N_element : 016"  # scripted group (container) (typed FeaturePython)
  n = 1
  ref = N_element
FEATURE [App::DocumentObjectGroupPython] O_element084  label="O_element : 045"  # scripted group (container) (typed FeaturePython)
  n = 1
  ref = O_element
FEATURE [App::DocumentObjectGroupPython] G4_POLYVINYL_PYRROLIDONE  # scripted group (container) (typed FeaturePython)
  Dunit = g/cm3
  Dvalue = 1.25
  Group = -> [C_element095,H_element087,N_element037,O_element084]
  conduct = 2
  density = 1
  expand = 3
  formula = G4_POLYVINYL_PYRROLIDONE
  name = G4_POLYVINYL_PYRROLIDONE
  specific = 4
FEATURE [App::DocumentObjectGroupPython] K_element008  label="K_element : 1"  # scripted group (container) (typed FeaturePython)
  n = 1
  ref = K_element
FEATURE [App::DocumentObjectGroupPython] I_element006  label="I_element : 003"  # scripted group (container) (typed FeaturePython)
  n = 1
  ref = I_element
FEATURE [App::DocumentObjectGroupPython] G4_POTASSIUM_IODIDE  # scripted group (container) (typed FeaturePython)
  Dunit = g/cm3
  Dvalue = 3.13
  Group = -> [K_element008,I_element006]
  conduct = 2
  density = 1
  expand = 3
  formula = G4_POTASSIUM_IODIDE
  name = G4_POTASSIUM_IODIDE
  specific = 4
FEATURE [App::DocumentObjectGroupPython] K_element009  label="K_element : 2"  # scripted group (container) (typed FeaturePython)
  n = 2
  ref = K_element
FEATURE [App::DocumentObjectGroupPython] O_element085  label="O_element : 046"  # scripted group (container) (typed FeaturePython)
  n = 1
  ref = O_element
FEATURE [App::DocumentObjectGroupPython] G4_POTASSIUM_OXIDE  # scripted group (container) (typed FeaturePython)
  Dunit = g/cm3
  Dvalue = 2.32
  Group = -> [K_element009,O_element085]
  conduct = 2
  density = 1
  expand = 3
  formula = G4_POTASSIUM_OXIDE
  name = G4_POTASSIUM_OXIDE
  specific = 4
FEATURE [App::DocumentObjectGroupPython] C_element096  label="C_element : 054"  # scripted group (container) (typed FeaturePython)
  n = 3
  ref = C_element
FEATURE [App::DocumentObjectGroupPython] H_element088  label="H_element : 049"  # scripted group (container) (typed FeaturePython)
  n = 8
  ref = H_element
FEATURE [App::DocumentObjectGroupPython] G4_PROPANE  # scripted group (container) (typed FeaturePython)
  Dunit = g/cm3
  Dvalue = 0.00187939
  Group = -> [C_element096,H_element088]
  conduct = 2
  density = 1
  expand = 3
  formula = G4_PROPANE
  name = G4_PROPANE
  specific = 4
FEATURE [App::DocumentObjectGroupPython] C_element097  label="C_element : 055"  # scripted group (container) (typed FeaturePython)
  n = 3
  ref = C_element
FEATURE [App::DocumentObjectGroupPython] H_element089  label="H_element : 050"  # scripted group (container) (typed FeaturePython)
  n = 8
  ref = H_element
FEATURE [App::DocumentObjectGroupPython] G4_lPROPANE  # scripted group (container) (typed FeaturePython)
  Dunit = g/cm3
  Dvalue = 0.43
  Group = -> [C_element097,H_element089]
  conduct = 2
  density = 1
  expand = 3
  formula = G4_lPROPANE
  name = G4_lPROPANE
  specific = 4
FEATURE [App::DocumentObjectGroupPython] C_element098  label="C_element : 056"  # scripted group (container) (typed FeaturePython)
  n = 3
  ref = C_element
FEATURE [App::DocumentObjectGroupPython] H_element090  label="H_element : 051"  # scripted group (container) (typed FeaturePython)
  n = 8
  ref = H_element
FEATURE [App::DocumentObjectGroupPython] O_element086  label="O_element : 047"  # scripted group (container) (typed FeaturePython)
  n = 1
  ref = O_element
FEATURE [App::DocumentObjectGroupPython] G4_N_PROPYL_ALCOHOL  label="G4_N-PROPYL_ALCOHOL"  # scripted group (container) (typed FeaturePython)
  Dunit = g/cm3
  Dvalue = 0.8035
  Group = -> [C_element098,H_element090,O_element086]
  conduct = 2
  density = 1
  expand = 3
  formula = G4_N-PROPYL_ALCOHOL
  name = G4_N-PROPYL_ALCOHOL
  specific = 4
FEATURE [App::DocumentObjectGroupPython] C_element099  label="C_element : 057"  # scripted group (container) (typed FeaturePython)
  n = 5
  ref = C_element
FEATURE [App::DocumentObjectGroupPython] H_element091  label="H_element : 052"  # scripted group (container) (typed FeaturePython)
  n = 5
  ref = H_element
FEATURE [App::DocumentObjectGroupPython] N_element038  label="N_element : 017"  # scripted group (container) (typed FeaturePython)
  n = 1
  ref = N_element
FEATURE [App::DocumentObjectGroupPython] G4_PYRIDINE  # scripted group (container) (typed FeaturePython)
  Dunit = g/cm3
  Dvalue = 0.9819
  Group = -> [C_element099,H_element091,N_element038]
  conduct = 2
  density = 1
  expand = 3
  formula = G4_PYRIDINE
  name = G4_PYRIDINE
  specific = 4
FEATURE [App::DocumentObjectGroupPython] H_element092  label="H_element : 0.144"  # scripted group (container) (typed FeaturePython)
  n = 0.143711
FEATURE [App::DocumentObjectGroupPython] C_element100  label="C_element : 0.856"  # scripted group (container) (typed FeaturePython)
  n = 0.856289
FEATURE [App::DocumentObjectGroupPython] G4_RUBBER_BUTYL  # scripted group (container) (typed FeaturePython)
  Dunit = g/cm3
  Dvalue = 0.92
  Group = -> [H_element092,C_element100]
  conduct = 2
  density = 1
  expand = 3
  formula = G4_RUBBER_BUTYL
  name = G4_RUBBER_BUTYL
  specific = 4
FEATURE [App::DocumentObjectGroupPython] H_element093  label="H_element : 0.118"  # scripted group (container) (typed FeaturePython)
  n = 0.118371
FEATURE [App::DocumentObjectGroupPython] C_element101  label="C_element : 0.882"  # scripted group (container) (typed FeaturePython)
  n = 0.881629
FEATURE [App::DocumentObjectGroupPython] G4_RUBBER_NATURAL  # scripted group (container) (typed FeaturePython)
  Dunit = g/cm3
  Dvalue = 0.92
  Group = -> [H_element093,C_element101]
  conduct = 2
  density = 1
  expand = 3
  formula = G4_RUBBER_NATURAL
  name = G4_RUBBER_NATURAL
  specific = 4
FEATURE [App::DocumentObjectGroupPython] H_element094  label="H_element : 0.145"  # scripted group (container) (typed FeaturePython)
  n = 0.05692
FEATURE [App::DocumentObjectGroupPython] C_element102  label="C_element : 0.543"  # scripted group (container) (typed FeaturePython)
  n = 0.542646
FEATURE [App::DocumentObjectGroupPython] Cl_element021  label="Cl_element : 0.400"  # scripted group (container) (typed FeaturePython)
  n = 0.400434
FEATURE [App::DocumentObjectGroupPython] G4_RUBBER_NEOPRENE  # scripted group (container) (typed FeaturePython)
  Dunit = g/cm3
  Dvalue = 1.23
  Group = -> [H_element094,C_element102,Cl_element021]
  conduct = 2
  density = 1
  expand = 3
  formula = G4_RUBBER_NEOPRENE
  name = G4_RUBBER_NEOPRENE
  specific = 4
FEATURE [App::DocumentObjectGroupPython] Si_element006  label="Si_element : 1"  # scripted group (container) (typed FeaturePython)
  n = 1
  ref = Si_element
FEATURE [App::DocumentObjectGroupPython] O_element087  label="O_element : 048"  # scripted group (container) (typed FeaturePython)
  n = 2
  ref = O_element
FEATURE [App::DocumentObjectGroupPython] G4_SILICON_DIOXIDE002  label="G4_SILICON_DIOXIDE"  # scripted group (container) (typed FeaturePython)
  Dunit = g/cm3
  Dvalue = 2.32
  Group = -> [Si_element006,O_element087]
  conduct = 2
  density = 1
  expand = 3
  formula = G4_SILICON_DIOXIDE
  name = G4_SILICON_DIOXIDE
  specific = 4
FEATURE [App::DocumentObjectGroupPython] Ag_element002  label="Ag_element : 1"  # scripted group (container) (typed FeaturePython)
  n = 1
  ref = Ag_element
FEATURE [App::DocumentObjectGroupPython] Br_element005  label="Br_element : 003"  # scripted group (container) (typed FeaturePython)
  n = 1
  ref = Br_element
FEATURE [App::DocumentObjectGroupPython] G4_SILVER_BROMIDE  # scripted group (container) (typed FeaturePython)
  Dunit = g/cm3
  Dvalue = 6.473
  Group = -> [Ag_element002,Br_element005]
  conduct = 2
  density = 1
  expand = 3
  formula = G4_SILVER_BROMIDE
  name = G4_SILVER_BROMIDE
  specific = 4
FEATURE [App::DocumentObjectGroupPython] Ag_element003  label="Ag_element : 002"  # scripted group (container) (typed FeaturePython)
  n = 1
  ref = Ag_element
FEATURE [App::DocumentObjectGroupPython] Cl_element022  label="Cl_element : 011"  # scripted group (container) (typed FeaturePython)
  n = 1
  ref = Cl_element
FEATURE [App::DocumentObjectGroupPython] G4_SILVER_CHLORIDE  # scripted group (container) (typed FeaturePython)
  Dunit = g/cm3
  Dvalue = 5.56
  Group = -> [Ag_element003,Cl_element022]
  conduct = 2
  density = 1
  expand = 3
  formula = G4_SILVER_CHLORIDE
  name = G4_SILVER_CHLORIDE
  specific = 4
FEATURE [App::DocumentObjectGroupPython] Br_element006  label="Br_element : 0.423"  # scripted group (container) (typed FeaturePython)
  n = 0.422895
FEATURE [App::DocumentObjectGroupPython] Ag_element004  label="Ag_element : 0.574"  # scripted group (container) (typed FeaturePython)
  n = 0.573748
FEATURE [App::DocumentObjectGroupPython] I_element007  label="I_element : 0.649"  # scripted group (container) (typed FeaturePython)
  n = 0.003357
FEATURE [App::DocumentObjectGroupPython] G4_SILVER_HALIDES  # scripted group (container) (typed FeaturePython)
  Dunit = g/cm3
  Dvalue = 6.47
  Group = -> [Br_element006,Ag_element004,I_element007]
  conduct = 2
  density = 1
  expand = 3
  formula = G4_SILVER_HALIDES
  name = G4_SILVER_HALIDES
  specific = 4
FEATURE [App::DocumentObjectGroupPython] Ag_element005  label="Ag_element : 003"  # scripted group (container) (typed FeaturePython)
  n = 1
  ref = Ag_element
FEATURE [App::DocumentObjectGroupPython] I_element008  label="I_element : 004"  # scripted group (container) (typed FeaturePython)
  n = 1
  ref = I_element
FEATURE [App::DocumentObjectGroupPython] G4_SILVER_IODIDE  # scripted group (container) (typed FeaturePython)
  Dunit = g/cm3
  Dvalue = 6.01
  Group = -> [Ag_element005,I_element008]
  conduct = 2
  density = 1
  expand = 3
  formula = G4_SILVER_IODIDE
  name = G4_SILVER_IODIDE
  specific = 4
FEATURE [App::DocumentObjectGroupPython] H_element095  label="H_element : 0.100"  # scripted group (container) (typed FeaturePython)
  n = 0.1
FEATURE [App::DocumentObjectGroupPython] C_element103  label="C_element : 0.204"  # scripted group (container) (typed FeaturePython)
  n = 0.204
FEATURE [App::DocumentObjectGroupPython] N_element039  label="N_element : 0.759"  # scripted group (container) (typed FeaturePython)
  n = 0.042
FEATURE [App::DocumentObjectGroupPython] O_element088  label="O_element : 0.645"  # scripted group (container) (typed FeaturePython)
  n = 0.645
FEATURE [App::DocumentObjectGroupPython] Na_element013  label="Na_element : 0.100"  # scripted group (container) (typed FeaturePython)
  n = 0.002
FEATURE [App::DocumentObjectGroupPython] P_element009  label="P_element : 0.107"  # scripted group (container) (typed FeaturePython)
  n = 0.001
FEATURE [App::DocumentObjectGroupPython] S_element020  label="S_element : 0.021"  # scripted group (container) (typed FeaturePython)
  n = 0.002
FEATURE [App::DocumentObjectGroupPython] Cl_element023  label="Cl_element : 0.590"  # scripted group (container) (typed FeaturePython)
  n = 0.003
FEATURE [App::DocumentObjectGroupPython] K_element010  label="K_element : 0.001"  # scripted group (container) (typed FeaturePython)
  n = 0.001
FEATURE [App::DocumentObjectGroupPython] G4_SKIN_ICRP  # scripted group (container) (typed FeaturePython)
  Dunit = g/cm3
  Dvalue = 1.09
  Group = -> [H_element095,C_element103,N_element039,O_element088,Na_element013,P_element009,S_element020,Cl_element023,K_element010]
  conduct = 2
  density = 1
  expand = 3
  formula = G4_SKIN_ICRP
  name = G4_SKIN_ICRP
  specific = 4
FEATURE [App::DocumentObjectGroupPython] Na_element014  label="Na_element : 2"  # scripted group (container) (typed FeaturePython)
  n = 2
  ref = Na_element
FEATURE [App::DocumentObjectGroupPython] C_element104  label="C_element : 058"  # scripted group (container) (typed FeaturePython)
  n = 1
  ref = C_element
FEATURE [App::DocumentObjectGroupPython] O_element089  label="O_element : 049"  # scripted group (container) (typed FeaturePython)
  n = 3
  ref = O_element
FEATURE [App::DocumentObjectGroupPython] G4_SODIUM_CARBONATE  # scripted group (container) (typed FeaturePython)
  Dunit = g/cm3
  Dvalue = 2.532
  Group = -> [Na_element014,C_element104,O_element089]
  conduct = 2
  density = 1
  expand = 3
  formula = G4_SODIUM_CARBONATE
  name = G4_SODIUM_CARBONATE
  specific = 4
FEATURE [App::DocumentObjectGroupPython] Na_element015  label="Na_element : 1"  # scripted group (container) (typed FeaturePython)
  n = 1
  ref = Na_element
FEATURE [App::DocumentObjectGroupPython] I_element009  label="I_element : 005"  # scripted group (container) (typed FeaturePython)
  n = 1
  ref = I_element
FEATURE [App::DocumentObjectGroupPython] G4_SODIUM_IODIDE  # scripted group (container) (typed FeaturePython)
  Dunit = g/cm3
  Dvalue = 3.667
  Group = -> [Na_element015,I_element009]
  conduct = 2
  density = 1
  expand = 3
  formula = G4_SODIUM_IODIDE
  name = G4_SODIUM_IODIDE
  specific = 4
FEATURE [App::DocumentObjectGroupPython] Na_element016  label="Na_element : 003"  # scripted group (container) (typed FeaturePython)
  n = 2
  ref = Na_element
FEATURE [App::DocumentObjectGroupPython] O_element090  label="O_element : 050"  # scripted group (container) (typed FeaturePython)
  n = 1
  ref = O_element
FEATURE [App::DocumentObjectGroupPython] G4_SODIUM_MONOXIDE  # scripted group (container) (typed FeaturePython)
  Dunit = g/cm3
  Dvalue = 2.27
  Group = -> [Na_element016,O_element090]
  conduct = 2
  density = 1
  expand = 3
  formula = G4_SODIUM_MONOXIDE
  name = G4_SODIUM_MONOXIDE
  specific = 4
FEATURE [App::DocumentObjectGroupPython] Na_element017  label="Na_element : 004"  # scripted group (container) (typed FeaturePython)
  n = 1
  ref = Na_element
FEATURE [App::DocumentObjectGroupPython] N_element040  label="N_element : 018"  # scripted group (container) (typed FeaturePython)
  n = 1
  ref = N_element
FEATURE [App::DocumentObjectGroupPython] O_element091  label="O_element : 051"  # scripted group (container) (typed FeaturePython)
  n = 3
  ref = O_element
FEATURE [App::DocumentObjectGroupPython] G4_SODIUM_NITRATE  # scripted group (container) (typed FeaturePython)
  Dunit = g/cm3
  Dvalue = 2.261
  Group = -> [Na_element017,N_element040,O_element091]
  conduct = 2
  density = 1
  expand = 3
  formula = G4_SODIUM_NITRATE
  name = G4_SODIUM_NITRATE
  specific = 4
FEATURE [App::DocumentObjectGroupPython] C_element105  label="C_element : 059"  # scripted group (container) (typed FeaturePython)
  n = 14
  ref = C_element
FEATURE [App::DocumentObjectGroupPython] H_element096  label="H_element : 053"  # scripted group (container) (typed FeaturePython)
  n = 12
  ref = H_element
FEATURE [App::DocumentObjectGroupPython] G4_STILBENE  # scripted group (container) (typed FeaturePython)
  Dunit = g/cm3
  Dvalue = 0.9707
  Group = -> [C_element105,H_element096]
  conduct = 2
  density = 1
  expand = 3
  formula = G4_STILBENE
  name = G4_STILBENE
  specific = 4
FEATURE [App::DocumentObjectGroupPython] C_element106  label="C_element : 12"  # scripted group (container) (typed FeaturePython)
  n = 12
  ref = C_element
FEATURE [App::DocumentObjectGroupPython] H_element097  label="H_element : 22"  # scripted group (container) (typed FeaturePython)
  n = 22
  ref = H_element
FEATURE [App::DocumentObjectGroupPython] O_element092  label="O_element : 11"  # scripted group (container) (typed FeaturePython)
  n = 11
  ref = O_element
FEATURE [App::DocumentObjectGroupPython] G4_SUCROSE  # scripted group (container) (typed FeaturePython)
  Dunit = g/cm3
  Dvalue = 1.5805
  Group = -> [C_element106,H_element097,O_element092]
  conduct = 2
  density = 1
  expand = 3
  formula = G4_SUCROSE
  name = G4_SUCROSE
  specific = 4
FEATURE [App::DocumentObjectGroupPython] C_element107  label="C_element : 18"  # scripted group (container) (typed FeaturePython)
  n = 18
  ref = C_element
FEATURE [App::DocumentObjectGroupPython] H_element098  label="H_element : 054"  # scripted group (container) (typed FeaturePython)
  n = 14
  ref = H_element
FEATURE [App::DocumentObjectGroupPython] G4_TERPHENYL  # scripted group (container) (typed FeaturePython)
  Dunit = g/cm3
  Dvalue = 1.24
  Group = -> [C_element107,H_element098]
  conduct = 2
  density = 1
  expand = 3
  formula = G4_TERPHENYL
  name = G4_TERPHENYL
  specific = 4
FEATURE [App::DocumentObjectGroupPython] H_element099  label="H_element : 0.146"  # scripted group (container) (typed FeaturePython)
  n = 0.106
FEATURE [App::DocumentObjectGroupPython] C_element108  label="C_element : 0.883"  # scripted group (container) (typed FeaturePython)
  n = 0.099
FEATURE [App::DocumentObjectGroupPython] N_element041  label="N_element : 0.020"  # scripted group (container) (typed FeaturePython)
  n = 0.02
FEATURE [App::DocumentObjectGroupPython] O_element093  label="O_element : 0.766"  # scripted group (container) (typed FeaturePython)
  n = 0.766
FEATURE [App::DocumentObjectGroupPython] Na_element018  label="Na_element : 0.101"  # scripted group (container) (typed FeaturePython)
  n = 0.002
FEATURE [App::DocumentObjectGroupPython] P_element010  label="P_element : 0.108"  # scripted group (container) (typed FeaturePython)
  n = 0.001
FEATURE [App::DocumentObjectGroupPython] S_element021  label="S_element : 0.022"  # scripted group (container) (typed FeaturePython)
  n = 0.002
FEATURE [App::DocumentObjectGroupPython] Cl_element024  label="Cl_element : 0.002"  # scripted group (container) (typed FeaturePython)
  n = 0.002
FEATURE [App::DocumentObjectGroupPython] K_element011  label="K_element : 0.017"  # scripted group (container) (typed FeaturePython)
  n = 0.002
FEATURE [App::DocumentObjectGroupPython] G4_TESTIS_ICRP  # scripted group (container) (typed FeaturePython)
  Dunit = g/cm3
  Dvalue = 1.04
  Group = -> [H_element099,C_element108,N_element041,O_element093,Na_element018,P_element010,S_element021,Cl_element024,K_element011]
  conduct = 2
  density = 1
  expand = 3
  formula = G4_TESTIS_ICRP
  name = G4_TESTIS_ICRP
  specific = 4
FEATURE [App::DocumentObjectGroupPython] C_element109  label="C_element : 060"  # scripted group (container) (typed FeaturePython)
  n = 2
  ref = C_element
FEATURE [App::DocumentObjectGroupPython] Cl_element025  label="Cl_element : 012"  # scripted group (container) (typed FeaturePython)
  n = 4
  ref = Cl_element
FEATURE [App::DocumentObjectGroupPython] G4_TETRACHLOROETHYLENE  # scripted group (container) (typed FeaturePython)
  Dunit = g/cm3
  Dvalue = 1.625
  Group = -> [C_element109,Cl_element025]
  conduct = 2
  density = 1
  expand = 3
  formula = G4_TETRACHLOROETHYLENE
  name = G4_TETRACHLOROETHYLENE
  specific = 4
FEATURE [App::DocumentObjectGroupPython] Tl_element001  label="Tl_element : 1"  # scripted group (container) (typed FeaturePython)
  n = 1
  ref = Tl_element
FEATURE [App::DocumentObjectGroupPython] Cl_element026  label="Cl_element : 013"  # scripted group (container) (typed FeaturePython)
  n = 1
  ref = Cl_element
FEATURE [App::DocumentObjectGroupPython] G4_THALLIUM_CHLORIDE  # scripted group (container) (typed FeaturePython)
  Dunit = g/cm3
  Dvalue = 7.004
  Group = -> [Tl_element001,Cl_element026]
  conduct = 2
  density = 1
  expand = 3
  formula = G4_THALLIUM_CHLORIDE
  name = G4_THALLIUM_CHLORIDE
  specific = 4
FEATURE [App::DocumentObjectGroupPython] H_element100  label="H_element : 0.147"  # scripted group (container) (typed FeaturePython)
  n = 0.105
FEATURE [App::DocumentObjectGroupPython] C_element110  label="C_element : 0.256"  # scripted group (container) (typed FeaturePython)
  n = 0.256
FEATURE [App::DocumentObjectGroupPython] N_element042  label="N_element : 0.760"  # scripted group (container) (typed FeaturePython)
  n = 0.027
FEATURE [App::DocumentObjectGroupPython] O_element094  label="O_element : 0.602"  # scripted group (container) (typed FeaturePython)
  n = 0.602
FEATURE [App::DocumentObjectGroupPython] Na_element019  label="Na_element : 0.102"  # scripted group (container) (typed FeaturePython)
  n = 0.001
FEATURE [App::DocumentObjectGroupPython] P_element011  label="P_element : 0.109"  # scripted group (container) (typed FeaturePython)
  n = 0.002
FEATURE [App::DocumentObjectGroupPython] S_element022  label="S_element : 0.023"  # scripted group (container) (typed FeaturePython)
  n = 0.003
FEATURE [App::DocumentObjectGroupPython] Cl_element027  label="Cl_element : 0.591"  # scripted group (container) (typed FeaturePython)
  n = 0.002
FEATURE [App::DocumentObjectGroupPython] K_element012  label="K_element : 0.018"  # scripted group (container) (typed FeaturePython)
  n = 0.002
FEATURE [App::DocumentObjectGroupPython] G4_TISSUE_SOFT_ICRP  # scripted group (container) (typed FeaturePython)
  Dunit = g/cm3
  Dvalue = 1.03
  Group = -> [H_element100,C_element110,N_element042,O_element094,Na_element019,P_element011,S_element022,Cl_element027,K_element012]
  conduct = 2
  density = 1
  expand = 3
  formula = G4_TISSUE_SOFT_ICRP
  name = G4_TISSUE_SOFT_ICRP
  specific = 4
FEATURE [App::DocumentObjectGroupPython] H_element101  label="H_element : 0.148"  # scripted group (container) (typed FeaturePython)
  n = 0.101
FEATURE [App::DocumentObjectGroupPython] C_element111  label="C_element : 0.111"  # scripted group (container) (typed FeaturePython)
  n = 0.111
FEATURE [App::DocumentObjectGroupPython] N_element043  label="N_element : 0.026"  # scripted group (container) (typed FeaturePython)
  n = 0.026
FEATURE [App::DocumentObjectGroupPython] O_element095  label="O_element : 0.762"  # scripted group (container) (typed FeaturePython)
  n = 0.762
FEATURE [App::DocumentObjectGroupPython] G4_TISSUE_SOFT_ICRU_4  label="G4_TISSUE_SOFT_ICRU-4"  # scripted group (container) (typed FeaturePython)
  Dunit = g/cm3
  Dvalue = 1
  Group = -> [H_element101,C_element111,N_element043,O_element095]
  conduct = 2
  density = 1
  expand = 3
  formula = G4_TISSUE_SOFT_ICRU-4
  name = G4_TISSUE_SOFT_ICRU-4
  specific = 4
FEATURE [App::DocumentObjectGroupPython] H_element102  label="H_element : 0.149"  # scripted group (container) (typed FeaturePython)
  n = 0.101869
FEATURE [App::DocumentObjectGroupPython] C_element112  label="C_element : 0.456"  # scripted group (container) (typed FeaturePython)
  n = 0.456179
FEATURE [App::DocumentObjectGroupPython] N_element044  label="N_element : 0.761"  # scripted group (container) (typed FeaturePython)
  n = 0.035172
FEATURE [App::DocumentObjectGroupPython] O_element096  label="O_element : 0.407"  # scripted group (container) (typed FeaturePython)
  n = 0.40678
FEATURE [App::DocumentObjectGroupPython] G4_TISSUE_METHANE  label="G4_TISSUE-METHANE"  # scripted group (container) (typed FeaturePython)
  Dunit = g/cm3
  Dvalue = 0.00106409
  Group = -> [H_element102,C_element112,N_element044,O_element096]
  conduct = 2
  density = 1
  expand = 3
  formula = G4_TISSUE-METHANE
  name = G4_TISSUE-METHANE
  specific = 4
FEATURE [App::DocumentObjectGroupPython] H_element103  label="H_element : 0.103"  # scripted group (container) (typed FeaturePython)
  n = 0.102672
FEATURE [App::DocumentObjectGroupPython] C_element113  label="C_element : 0.569"  # scripted group (container) (typed FeaturePython)
  n = 0.56894
FEATURE [App::DocumentObjectGroupPython] N_element045  label="N_element : 0.762"  # scripted group (container) (typed FeaturePython)
  n = 0.035022
FEATURE [App::DocumentObjectGroupPython] O_element097  label="O_element : 0.293"  # scripted group (container) (typed FeaturePython)
  n = 0.293366
FEATURE [App::DocumentObjectGroupPython] G4_TISSUE_PROPANE  label="G4_TISSUE-PROPANE"  # scripted group (container) (typed FeaturePython)
  Dunit = g/cm3
  Dvalue = 0.00182628
  Group = -> [H_element103,C_element113,N_element045,O_element097]
  conduct = 2
  density = 1
  expand = 3
  formula = G4_TISSUE-PROPANE
  name = G4_TISSUE-PROPANE
  specific = 4
FEATURE [App::DocumentObjectGroupPython] Ti_element003  label="Ti_element : 1"  # scripted group (container) (typed FeaturePython)
  n = 1
  ref = Ti_element
FEATURE [App::DocumentObjectGroupPython] O_element098  label="O_element : 052"  # scripted group (container) (typed FeaturePython)
  n = 2
  ref = O_element
FEATURE [App::DocumentObjectGroupPython] G4_TITANIUM_DIOXIDE  # scripted group (container) (typed FeaturePython)
  Dunit = g/cm3
  Dvalue = 4.26
  Group = -> [Ti_element003,O_element098]
  conduct = 2
  density = 1
  expand = 3
  formula = G4_TITANIUM_DIOXIDE
  name = G4_TITANIUM_DIOXIDE
  specific = 4
FEATURE [App::DocumentObjectGroupPython] C_element114  label="C_element : 061"  # scripted group (container) (typed FeaturePython)
  n = 7
  ref = C_element
FEATURE [App::DocumentObjectGroupPython] H_element104  label="H_element : 055"  # scripted group (container) (typed FeaturePython)
  n = 8
  ref = H_element
FEATURE [App::DocumentObjectGroupPython] G4_TOLUENE  # scripted group (container) (typed FeaturePython)
  Dunit = g/cm3
  Dvalue = 0.8669
  Group = -> [C_element114,H_element104]
  conduct = 2
  density = 1
  expand = 3
  formula = G4_TOLUENE
  name = G4_TOLUENE
  specific = 4
FEATURE [App::DocumentObjectGroupPython] C_element115  label="C_element : 062"  # scripted group (container) (typed FeaturePython)
  n = 2
  ref = C_element
FEATURE [App::DocumentObjectGroupPython] H_element105  label="H_element : 056"  # scripted group (container) (typed FeaturePython)
  n = 1
  ref = H_element
FEATURE [App::DocumentObjectGroupPython] Cl_element028  label="Cl_element : 014"  # scripted group (container) (typed FeaturePython)
  n = 3
  ref = Cl_element
FEATURE [App::DocumentObjectGroupPython] G4_TRICHLOROETHYLENE  # scripted group (container) (typed FeaturePython)
  Dunit = g/cm3
  Dvalue = 1.46
  Group = -> [C_element115,H_element105,Cl_element028]
  conduct = 2
  density = 1
  expand = 3
  formula = G4_TRICHLOROETHYLENE
  name = G4_TRICHLOROETHYLENE
  specific = 4
FEATURE [App::DocumentObjectGroupPython] C_element116  label="C_element : 063"  # scripted group (container) (typed FeaturePython)
  n = 6
  ref = C_element
FEATURE [App::DocumentObjectGroupPython] H_element106  label="H_element : 15"  # scripted group (container) (typed FeaturePython)
  n = 15
  ref = H_element
FEATURE [App::DocumentObjectGroupPython] O_element099  label="O_element : 053"  # scripted group (container) (typed FeaturePython)
  n = 4
  ref = O_element
FEATURE [App::DocumentObjectGroupPython] P_element012  label="P_element : 1"  # scripted group (container) (typed FeaturePython)
  n = 1
  ref = P_element
FEATURE [App::DocumentObjectGroupPython] G4_TRIETHYL_PHOSPHATE  # scripted group (container) (typed FeaturePython)
  Dunit = g/cm3
  Dvalue = 1.07
  Group = -> [C_element116,H_element106,O_element099,P_element012]
  conduct = 2
  density = 1
  expand = 3
  formula = G4_TRIETHYL_PHOSPHATE
  name = G4_TRIETHYL_PHOSPHATE
  specific = 4
FEATURE [App::DocumentObjectGroupPython] W_element003  label="W_element : 003"  # scripted group (container) (typed FeaturePython)
  n = 1
  ref = W_element
FEATURE [App::DocumentObjectGroupPython] F_element017  label="F_element : 6"  # scripted group (container) (typed FeaturePython)
  n = 6
  ref = F_element
FEATURE [App::DocumentObjectGroupPython] G4_TUNGSTEN_HEXAFLUORIDE  # scripted group (container) (typed FeaturePython)
  Dunit = g/cm3
  Dvalue = 2.4
  Group = -> [W_element003,F_element017]
  conduct = 2
  density = 1
  expand = 3
  formula = G4_TUNGSTEN_HEXAFLUORIDE
  name = G4_TUNGSTEN_HEXAFLUORIDE
  specific = 4
FEATURE [App::DocumentObjectGroupPython] U_element001  label="U_element : 1"  # scripted group (container) (typed FeaturePython)
  n = 1
  ref = U_element
FEATURE [App::DocumentObjectGroupPython] C_element117  label="C_element : 064"  # scripted group (container) (typed FeaturePython)
  n = 2
  ref = C_element
FEATURE [App::DocumentObjectGroupPython] G4_URANIUM_DICARBIDE  # scripted group (container) (typed FeaturePython)
  Dunit = g/cm3
  Dvalue = 11.28
  Group = -> [U_element001,C_element117]
  conduct = 2
  density = 1
  expand = 3
  formula = G4_URANIUM_DICARBIDE
  name = G4_URANIUM_DICARBIDE
  specific = 4
FEATURE [App::DocumentObjectGroupPython] U_element002  label="U_element : 002"  # scripted group (container) (typed FeaturePython)
  n = 1
  ref = U_element
FEATURE [App::DocumentObjectGroupPython] C_element118  label="C_element : 065"  # scripted group (container) (typed FeaturePython)
  n = 1
  ref = C_element
FEATURE [App::DocumentObjectGroupPython] G4_URANIUM_MONOCARBIDE  # scripted group (container) (typed FeaturePython)
  Dunit = g/cm3
  Dvalue = 13.63
  Group = -> [U_element002,C_element118]
  conduct = 2
  density = 1
  expand = 3
  formula = G4_URANIUM_MONOCARBIDE
  name = G4_URANIUM_MONOCARBIDE
  specific = 4
FEATURE [App::DocumentObjectGroupPython] U_element003  label="U_element : 003"  # scripted group (container) (typed FeaturePython)
  n = 1
  ref = U_element
FEATURE [App::DocumentObjectGroupPython] O_element100  label="O_element : 054"  # scripted group (container) (typed FeaturePython)
  n = 2
  ref = O_element
FEATURE [App::DocumentObjectGroupPython] G4_URANIUM_OXIDE  # scripted group (container) (typed FeaturePython)
  Dunit = g/cm3
  Dvalue = 10.96
  Group = -> [U_element003,O_element100]
  conduct = 2
  density = 1
  expand = 3
  formula = G4_URANIUM_OXIDE
  name = G4_URANIUM_OXIDE
  specific = 4
FEATURE [App::DocumentObjectGroupPython] C_element119  label="C_element : 066"  # scripted group (container) (typed FeaturePython)
  n = 1
  ref = C_element
FEATURE [App::DocumentObjectGroupPython] H_element107  label="H_element : 057"  # scripted group (container) (typed FeaturePython)
  n = 4
  ref = H_element
FEATURE [App::DocumentObjectGroupPython] N_element046  label="N_element : 019"  # scripted group (container) (typed FeaturePython)
  n = 2
  ref = N_element
FEATURE [App::DocumentObjectGroupPython] O_element101  label="O_element : 055"  # scripted group (container) (typed FeaturePython)
  n = 1
  ref = O_element
FEATURE [App::DocumentObjectGroupPython] G4_UREA  # scripted group (container) (typed FeaturePython)
  Dunit = g/cm3
  Dvalue = 1.323
  Group = -> [C_element119,H_element107,N_element046,O_element101]
  conduct = 2
  density = 1
  expand = 3
  formula = G4_UREA
  name = G4_UREA
  specific = 4
FEATURE [App::DocumentObjectGroupPython] C_element120  label="C_element : 067"  # scripted group (container) (typed FeaturePython)
  n = 5
  ref = C_element
FEATURE [App::DocumentObjectGroupPython] H_element108  label="H_element : 058"  # scripted group (container) (typed FeaturePython)
  n = 11
  ref = H_element
FEATURE [App::DocumentObjectGroupPython] N_element047  label="N_element : 020"  # scripted group (container) (typed FeaturePython)
  n = 1
  ref = N_element
FEATURE [App::DocumentObjectGroupPython] O_element102  label="O_element : 056"  # scripted group (container) (typed FeaturePython)
  n = 2
  ref = O_element
FEATURE [App::DocumentObjectGroupPython] G4_VALINE  # scripted group (container) (typed FeaturePython)
  Dunit = g/cm3
  Dvalue = 1.23
  Group = -> [C_element120,H_element108,N_element047,O_element102]
  conduct = 2
  density = 1
  expand = 3
  formula = G4_VALINE
  name = G4_VALINE
  specific = 4
FEATURE [App::DocumentObjectGroupPython] H_element109  label="H_element : 0.009"  # scripted group (container) (typed FeaturePython)
  n = 0.009417
FEATURE [App::DocumentObjectGroupPython] C_element121  label="C_element : 0.281"  # scripted group (container) (typed FeaturePython)
  n = 0.280555
FEATURE [App::DocumentObjectGroupPython] F_element018  label="F_element : 0.710"  # scripted group (container) (typed FeaturePython)
  n = 0.710028
FEATURE [App::DocumentObjectGroupPython] G4_VITON  # scripted group (container) (typed FeaturePython)
  Dunit = g/cm3
  Dvalue = 1.8
  Group = -> [H_element109,C_element121,F_element018]
  conduct = 2
  density = 1
  expand = 3
  formula = G4_VITON
  name = G4_VITON
  specific = 4
FEATURE [App::DocumentObjectGroupPython] H_element110  label="H_element : 059"  # scripted group (container) (typed FeaturePython)
  n = 2
  ref = H_element
FEATURE [App::DocumentObjectGroupPython] O_element103  label="O_element : 057"  # scripted group (container) (typed FeaturePython)
  n = 1
  ref = O_element
FEATURE [App::DocumentObjectGroupPython] G4_WATER  # scripted group (container) (typed FeaturePython)
  Dunit = g/cm3
  Dvalue = 1
  Group = -> [H_element110,O_element103]
  conduct = 2
  density = 1
  expand = 3
  formula = G4_WATER
  name = G4_WATER
  specific = 4
FEATURE [App::DocumentObjectGroupPython] H_element111  label="H_element : 060"  # scripted group (container) (typed FeaturePython)
  n = 2
  ref = H_element
FEATURE [App::DocumentObjectGroupPython] O_element104  label="O_element : 058"  # scripted group (container) (typed FeaturePython)
  n = 1
  ref = O_element
FEATURE [App::DocumentObjectGroupPython] G4_WATER_VAPOR  # scripted group (container) (typed FeaturePython)
  Dunit = g/cm3
  Dvalue = 0.000756182
  Group = -> [H_element111,O_element104]
  conduct = 2
  density = 1
  expand = 3
  formula = G4_WATER_VAPOR
  name = G4_WATER_VAPOR
  specific = 4
FEATURE [App::DocumentObjectGroupPython] C_element122  label="C_element : 068"  # scripted group (container) (typed FeaturePython)
  n = 8
  ref = C_element
FEATURE [App::DocumentObjectGroupPython] H_element112  label="H_element : 061"  # scripted group (container) (typed FeaturePython)
  n = 10
  ref = H_element
FEATURE [App::DocumentObjectGroupPython] G4_XYLENE  # scripted group (container) (typed FeaturePython)
  Dunit = g/cm3
  Dvalue = 0.87
  Group = -> [C_element122,H_element112]
  conduct = 2
  density = 1
  expand = 3
  formula = G4_XYLENE
  name = G4_XYLENE
  specific = 4
FEATURE [App::DocumentObjectGroupPython] C_element123  label="C_element : 069"  # scripted group (container) (typed FeaturePython)
  n = 1
  ref = C_element
FEATURE [App::DocumentObjectGroupPython] G4_GRAPHITE  # scripted group (container) (typed FeaturePython)
  Dunit = g/cm3
  Dvalue = 2.21
  Group = -> [C_element123]
  conduct = 2
  density = 1
  expand = 3
  formula = G4_GRAPHITE
  name = G4_GRAPHITE
  specific = 4
FEATURE [App::DocumentObjectGroupPython] NIST  # scripted group (container) (typed FeaturePython)
  Group = -> [G4_A_150_TISSUE,G4_ACETONE,G4_ACETYLENE,G4_ADENINE,G4_ADIPOSE_TISSUE_ICRP,G4_AIR001,G4_ALANINE,G4_ALUMINUM_OXIDE,G4_AMBER,G4_AMMONIA,G4_ANILINE,G4_ANTHRACENE,G4_B_100_BONE,G4_BAKELITE,G4_BARIUM_FLUORIDE,G4_BARIUM_SULFATE,G4_BENZENE,G4_BERYLLIUM_OXIDE,G4_BGO,G4_BLOOD_ICRP,G4_BONE_COMPACT_ICRU,G4_BONE_CORTICAL_ICRP,G4_BORON_CARBIDE,G4_BORON_OXIDE,G4_BRAIN_ICRP,G4_BUTANE,G4_N_BUTYL_ALCOHOL,G4_C_552,+152 more]
FEATURE [App::DocumentObjectGroupPython] H_element113  label="H_element : 062"  # scripted group (container) (typed FeaturePython)
  n = 1
  ref = H_element
FEATURE [App::DocumentObjectGroupPython] G4_H  # scripted group (container) (typed FeaturePython)
  Dunit = g/cm3
  Dvalue = 8.3748e-05
  Group = -> [H_element113]
  conduct = 2
  density = 1
  expand = 3
  formula = H
  name = G4_H
  specific = 4
FEATURE [App::DocumentObjectGroupPython] He_element001  label="He_element : 1"  # scripted group (container) (typed FeaturePython)
  n = 1
  ref = He_element
FEATURE [App::DocumentObjectGroupPython] G4_He  # scripted group (container) (typed FeaturePython)
  Dunit = g/cm3
  Dvalue = 0.000166322
  Group = -> [He_element001]
  conduct = 2
  density = 1
  expand = 3
  formula = He
  name = G4_He
  specific = 4
FEATURE [App::DocumentObjectGroupPython] Li_element008  label="Li_element : 008"  # scripted group (container) (typed FeaturePython)
  n = 1
  ref = Li_element
FEATURE [App::DocumentObjectGroupPython] G4_Li  # scripted group (container) (typed FeaturePython)
  Dunit = g/cm3
  Dvalue = 0.534
  Group = -> [Li_element008]
  conduct = 2
  density = 1
  expand = 3
  formula = Li
  name = G4_Li
  specific = 4
FEATURE [App::DocumentObjectGroupPython] Be_element002  label="Be_element : 002"  # scripted group (container) (typed FeaturePython)
  n = 1
  ref = Be_element
FEATURE [App::DocumentObjectGroupPython] G4_Be  # scripted group (container) (typed FeaturePython)
  Dunit = g/cm3
  Dvalue = 1.848
  Group = -> [Be_element002]
  conduct = 2
  density = 1
  expand = 3
  formula = Be
  name = G4_Be
  specific = 4
FEATURE [App::DocumentObjectGroupPython] B_element007  label="B_element : 007"  # scripted group (container) (typed FeaturePython)
  n = 1
  ref = B_element
FEATURE [App::DocumentObjectGroupPython] G4_B  # scripted group (container) (typed FeaturePython)
  Dunit = g/cm3
  Dvalue = 2.37
  Group = -> [B_element007]
  conduct = 2
  density = 1
  expand = 3
  formula = B
  name = G4_B
  specific = 4
FEATURE [App::DocumentObjectGroupPython] C_element124  label="C_element : 070"  # scripted group (container) (typed FeaturePython)
  n = 1
  ref = C_element
FEATURE [App::DocumentObjectGroupPython] G4_C  # scripted group (container) (typed FeaturePython)
  Dunit = g/cm3
  Dvalue = 2
  Group = -> [C_element124]
  conduct = 2
  density = 1
  expand = 3
  formula = C
  name = G4_C
  specific = 4
FEATURE [App::DocumentObjectGroupPython] N_element048  label="N_element : 021"  # scripted group (container) (typed FeaturePython)
  n = 1
  ref = N_element
FEATURE [App::DocumentObjectGroupPython] G4_N  # scripted group (container) (typed FeaturePython)
  Dunit = g/cm3
  Dvalue = 0.0011652
  Group = -> [N_element048]
  conduct = 2
  density = 1
  expand = 3
  formula = N
  name = G4_N
  specific = 4
FEATURE [App::DocumentObjectGroupPython] O_element105  label="O_element : 059"  # scripted group (container) (typed FeaturePython)
  n = 1
  ref = O_element
FEATURE [App::DocumentObjectGroupPython] G4_O  # scripted group (container) (typed FeaturePython)
  Dunit = g/cm3
  Dvalue = 0.00133151
  Group = -> [O_element105]
  conduct = 2
  density = 1
  expand = 3
  formula = O
  name = G4_O
  specific = 4
FEATURE [App::DocumentObjectGroupPython] F_element019  label="F_element : 008"  # scripted group (container) (typed FeaturePython)
  n = 1
  ref = F_element
FEATURE [App::DocumentObjectGroupPython] G4_F  # scripted group (container) (typed FeaturePython)
  Dunit = g/cm3
  Dvalue = 0.00158029
  Group = -> [F_element019]
  conduct = 2
  density = 1
  expand = 3
  formula = F
  name = G4_F
  specific = 4
FEATURE [App::DocumentObjectGroupPython] Ne_element001  label="Ne_element : 1"  # scripted group (container) (typed FeaturePython)
  n = 1
  ref = Ne_element
FEATURE [App::DocumentObjectGroupPython] G4_Ne  # scripted group (container) (typed FeaturePython)
  Dunit = g/cm3
  Dvalue = 0.000838505
  Group = -> [Ne_element001]
  conduct = 2
  density = 1
  expand = 3
  formula = Ne
  name = G4_Ne
  specific = 4
FEATURE [App::DocumentObjectGroupPython] Na_element020  label="Na_element : 005"  # scripted group (container) (typed FeaturePython)
  n = 1
  ref = Na_element
FEATURE [App::DocumentObjectGroupPython] G4_Na  # scripted group (container) (typed FeaturePython)
  Dunit = g/cm3
  Dvalue = 0.971
  Group = -> [Na_element020]
  conduct = 2
  density = 1
  expand = 3
  formula = Na
  name = G4_Na
  specific = 4
FEATURE [App::DocumentObjectGroupPython] Mg_element011  label="Mg_element : 005"  # scripted group (container) (typed FeaturePython)
  n = 1
  ref = Mg_element
FEATURE [App::DocumentObjectGroupPython] G4_Mg  # scripted group (container) (typed FeaturePython)
  Dunit = g/cm3
  Dvalue = 1.74
  Group = -> [Mg_element011]
  conduct = 2
  density = 1
  expand = 3
  formula = Mg
  name = G4_Mg
  specific = 4
FEATURE [App::DocumentObjectGroupPython] Al_element004  label="Al_element : 1"  # scripted group (container) (typed FeaturePython)
  n = 1
  ref = Al_element
FEATURE [App::DocumentObjectGroupPython] G4_Al  # scripted group (container) (typed FeaturePython)
  Dunit = g/cm3
  Dvalue = 2.699
  Group = -> [Al_element004]
  conduct = 2
  density = 1
  expand = 3
  formula = Al
  name = G4_Al
  specific = 4
FEATURE [App::DocumentObjectGroupPython] Si_element007  label="Si_element : 002"  # scripted group (container) (typed FeaturePython)
  n = 1
  ref = Si_element
FEATURE [App::DocumentObjectGroupPython] G4_Si  # scripted group (container) (typed FeaturePython)
  Dunit = g/cm3
  Dvalue = 2.33
  Group = -> [Si_element007]
  conduct = 2
  density = 1
  expand = 3
  formula = Si
  name = G4_Si
  specific = 4
FEATURE [App::DocumentObjectGroupPython] P_element013  label="P_element : 002"  # scripted group (container) (typed FeaturePython)
  n = 1
  ref = P_element
FEATURE [App::DocumentObjectGroupPython] G4_P  # scripted group (container) (typed FeaturePython)
  Dunit = g/cm3
  Dvalue = 2.2
  Group = -> [P_element013]
  conduct = 2
  density = 1
  expand = 3
  formula = P
  name = G4_P
  specific = 4
FEATURE [App::DocumentObjectGroupPython] S_element023  label="S_element : 007"  # scripted group (container) (typed FeaturePython)
  n = 1
  ref = S_element
FEATURE [App::DocumentObjectGroupPython] G4_S  # scripted group (container) (typed FeaturePython)
  Dunit = g/cm3
  Dvalue = 2
  Group = -> [S_element023]
  conduct = 2
  density = 1
  expand = 3
  formula = S
  name = G4_S
  specific = 4
FEATURE [App::DocumentObjectGroupPython] Cl_element029  label="Cl_element : 015"  # scripted group (container) (typed FeaturePython)
  n = 1
  ref = Cl_element
FEATURE [App::DocumentObjectGroupPython] G4_Cl  # scripted group (container) (typed FeaturePython)
  Dunit = g/cm3
  Dvalue = 0.00299473
  Group = -> [Cl_element029]
  conduct = 2
  density = 1
  expand = 3
  formula = Cl
  name = G4_Cl
  specific = 4
FEATURE [App::DocumentObjectGroupPython] Ar_element002  label="Ar_element : 1"  # scripted group (container) (typed FeaturePython)
  n = 1
  ref = Ar_element
FEATURE [App::DocumentObjectGroupPython] G4_Ar  # scripted group (container) (typed FeaturePython)
  Dunit = g/cm3
  Dvalue = 0.00166201
  Group = -> [Ar_element002]
  conduct = 2
  density = 1
  expand = 3
  formula = Ar
  name = G4_Ar
  specific = 4
FEATURE [App::DocumentObjectGroupPython] K_element013  label="K_element : 003"  # scripted group (container) (typed FeaturePython)
  n = 1
  ref = K_element
FEATURE [App::DocumentObjectGroupPython] G4_K  # scripted group (container) (typed FeaturePython)
  Dunit = g/cm3
  Dvalue = 0.862
  Group = -> [K_element013]
  conduct = 2
  density = 1
  expand = 3
  formula = K
  name = G4_K
  specific = 4
FEATURE [App::DocumentObjectGroupPython] Ca_element014  label="Ca_element : 007"  # scripted group (container) (typed FeaturePython)
  n = 1
  ref = Ca_element
FEATURE [App::DocumentObjectGroupPython] G4_Ca  # scripted group (container) (typed FeaturePython)
  Dunit = g/cm3
  Dvalue = 1.55
  Group = -> [Ca_element014]
  conduct = 2
  density = 1
  expand = 3
  formula = Ca
  name = G4_Ca
  specific = 4
FEATURE [App::DocumentObjectGroupPython] Sc_element001  label="Sc_element : 1"  # scripted group (container) (typed FeaturePython)
  n = 1
  ref = Sc_element
FEATURE [App::DocumentObjectGroupPython] G4_Sc  # scripted group (container) (typed FeaturePython)
  Dunit = g/cm3
  Dvalue = 2.989
  Group = -> [Sc_element001]
  conduct = 2
  density = 1
  expand = 3
  formula = Sc
  name = G4_Sc
  specific = 4
FEATURE [App::DocumentObjectGroupPython] Ti_element004  label="Ti_element : 002"  # scripted group (container) (typed FeaturePython)
  n = 1
  ref = Ti_element
FEATURE [App::DocumentObjectGroupPython] G4_Ti  # scripted group (container) (typed FeaturePython)
  Dunit = g/cm3
  Dvalue = 4.54
  Group = -> [Ti_element004]
  conduct = 2
  density = 1
  expand = 3
  formula = Ti
  name = G4_Ti
  specific = 4
FEATURE [App::DocumentObjectGroupPython] V_element001  label="V_element : 1"  # scripted group (container) (typed FeaturePython)
  n = 1
  ref = V_element
FEATURE [App::DocumentObjectGroupPython] G4_V  # scripted group (container) (typed FeaturePython)
  Dunit = g/cm3
  Dvalue = 6.11
  Group = -> [V_element001]
  conduct = 2
  density = 1
  expand = 3
  formula = V
  name = G4_V
  specific = 4
FEATURE [App::DocumentObjectGroupPython] Cr_element001  label="Cr_element : 1"  # scripted group (container) (typed FeaturePython)
  n = 1
  ref = Cr_element
FEATURE [App::DocumentObjectGroupPython] G4_Cr  # scripted group (container) (typed FeaturePython)
  Dunit = g/cm3
  Dvalue = 7.18
  Group = -> [Cr_element001]
  conduct = 2
  density = 1
  expand = 3
  formula = Cr
  name = G4_Cr
  specific = 4
FEATURE [App::DocumentObjectGroupPython] Mn_element001  label="Mn_element : 1"  # scripted group (container) (typed FeaturePython)
  n = 1
  ref = Mn_element
FEATURE [App::DocumentObjectGroupPython] G4_Mn  # scripted group (container) (typed FeaturePython)
  Dunit = g/cm3
  Dvalue = 7.44
  Group = -> [Mn_element001]
  conduct = 2
  density = 1
  expand = 3
  formula = Mn
  name = G4_Mn
  specific = 4
FEATURE [App::DocumentObjectGroupPython] Fe_element007  label="Fe_element : 004"  # scripted group (container) (typed FeaturePython)
  n = 1
  ref = Fe_element
FEATURE [App::DocumentObjectGroupPython] G4_Fe  # scripted group (container) (typed FeaturePython)
  Dunit = g/cm3
  Dvalue = 7.874
  Group = -> [Fe_element007]
  conduct = 2
  density = 1
  expand = 3
  formula = Fe
  name = G4_Fe
  specific = 4
FEATURE [App::DocumentObjectGroupPython] Co_element001  label="Co_element : 1"  # scripted group (container) (typed FeaturePython)
  n = 1
  ref = Co_element
FEATURE [App::DocumentObjectGroupPython] G4_Co  # scripted group (container) (typed FeaturePython)
  Dunit = g/cm3
  Dvalue = 8.9
  Group = -> [Co_element001]
  conduct = 2
  density = 1
  expand = 3
  formula = Co
  name = G4_Co
  specific = 4
FEATURE [App::DocumentObjectGroupPython] Ni_element001  label="Ni_element : 1"  # scripted group (container) (typed FeaturePython)
  n = 1
  ref = Ni_element
FEATURE [App::DocumentObjectGroupPython] G4_Ni  # scripted group (container) (typed FeaturePython)
  Dunit = g/cm3
  Dvalue = 8.902
  Group = -> [Ni_element001]
  conduct = 2
  density = 1
  expand = 3
  formula = Ni
  name = G4_Ni
  specific = 4
FEATURE [App::DocumentObjectGroupPython] Cu_element001  label="Cu_element : 1"  # scripted group (container) (typed FeaturePython)
  n = 1
  ref = Cu_element
FEATURE [App::DocumentObjectGroupPython] G4_Cu  # scripted group (container) (typed FeaturePython)
  Dunit = g/cm3
  Dvalue = 8.96
  Group = -> [Cu_element001]
  conduct = 2
  density = 1
  expand = 3
  formula = Cu
  name = G4_Cu
  specific = 4
FEATURE [App::DocumentObjectGroupPython] Zn_element001  label="Zn_element : 1"  # scripted group (container) (typed FeaturePython)
  n = 1
  ref = Zn_element
FEATURE [App::DocumentObjectGroupPython] G4_Zn  # scripted group (container) (typed FeaturePython)
  Dunit = g/cm3
  Dvalue = 7.133
  Group = -> [Zn_element001]
  conduct = 2
  density = 1
  expand = 3
  formula = Zn
  name = G4_Zn
  specific = 4
FEATURE [App::DocumentObjectGroupPython] Ga_element002  label="Ga_element : 002"  # scripted group (container) (typed FeaturePython)
  n = 1
  ref = Ga_element
FEATURE [App::DocumentObjectGroupPython] G4_Ga  # scripted group (container) (typed FeaturePython)
  Dunit = g/cm3
  Dvalue = 5.904
  Group = -> [Ga_element002]
  conduct = 2
  density = 1
  expand = 3
  formula = Ga
  name = G4_Ga
  specific = 4
FEATURE [App::DocumentObjectGroupPython] Ge_element002  label="Ge_element : 1"  # scripted group (container) (typed FeaturePython)
  n = 1
  ref = Ge_element
FEATURE [App::DocumentObjectGroupPython] G4_Ge  # scripted group (container) (typed FeaturePython)
  Dunit = g/cm3
  Dvalue = 5.323
  Group = -> [Ge_element002]
  conduct = 2
  density = 1
  expand = 3
  formula = Ge
  name = G4_Ge
  specific = 4
FEATURE [App::DocumentObjectGroupPython] As_element003  label="As_element : 002"  # scripted group (container) (typed FeaturePython)
  n = 1
  ref = As_element
FEATURE [App::DocumentObjectGroupPython] G4_As  # scripted group (container) (typed FeaturePython)
  Dunit = g/cm3
  Dvalue = 5.73
  Group = -> [As_element003]
  conduct = 2
  density = 1
  expand = 3
  formula = As
  name = G4_As
  specific = 4
FEATURE [App::DocumentObjectGroupPython] Se_element001  label="Se_element : 1"  # scripted group (container) (typed FeaturePython)
  n = 1
  ref = Se_element
FEATURE [App::DocumentObjectGroupPython] G4_Se  # scripted group (container) (typed FeaturePython)
  Dunit = g/cm3
  Dvalue = 4.5
  Group = -> [Se_element001]
  conduct = 2
  density = 1
  expand = 3
  formula = Se
  name = G4_Se
  specific = 4
FEATURE [App::DocumentObjectGroupPython] Br_element007  label="Br_element : 004"  # scripted group (container) (typed FeaturePython)
  n = 1
  ref = Br_element
FEATURE [App::DocumentObjectGroupPython] G4_Br  # scripted group (container) (typed FeaturePython)
  Dunit = g/cm3
  Dvalue = 0.0070721
  Group = -> [Br_element007]
  conduct = 2
  density = 1
  expand = 3
  formula = Br
  name = G4_Br
  specific = 4
FEATURE [App::DocumentObjectGroupPython] Kr_element001  label="Kr_element : 1"  # scripted group (container) (typed FeaturePython)
  n = 1
  ref = Kr_element
FEATURE [App::DocumentObjectGroupPython] G4_Kr  # scripted group (container) (typed FeaturePython)
  Dunit = g/cm3
  Dvalue = 0.00347832
  Group = -> [Kr_element001]
  conduct = 2
  density = 1
  expand = 3
  formula = Kr
  name = G4_Kr
  specific = 4
FEATURE [App::DocumentObjectGroupPython] Rb_element001  label="Rb_element : 1"  # scripted group (container) (typed FeaturePython)
  n = 1
  ref = Rb_element
FEATURE [App::DocumentObjectGroupPython] G4_Rb  # scripted group (container) (typed FeaturePython)
  Dunit = g/cm3
  Dvalue = 1.532
  Group = -> [Rb_element001]
  conduct = 2
  density = 1
  expand = 3
  formula = Rb
  name = G4_Rb
  specific = 4
FEATURE [App::DocumentObjectGroupPython] Sr_element001  label="Sr_element : 1"  # scripted group (container) (typed FeaturePython)
  n = 1
  ref = Sr_element
FEATURE [App::DocumentObjectGroupPython] G4_Sr  # scripted group (container) (typed FeaturePython)
  Dunit = g/cm3
  Dvalue = 2.54
  Group = -> [Sr_element001]
  conduct = 2
  density = 1
  expand = 3
  formula = Sr
  name = G4_Sr
  specific = 4
FEATURE [App::DocumentObjectGroupPython] Y_element001  label="Y_element : 1"  # scripted group (container) (typed FeaturePython)
  n = 1
  ref = Y_element
FEATURE [App::DocumentObjectGroupPython] G4_Y  # scripted group (container) (typed FeaturePython)
  Dunit = g/cm3
  Dvalue = 4.469
  Group = -> [Y_element001]
  conduct = 2
  density = 1
  expand = 3
  formula = Y
  name = G4_Y
  specific = 4
FEATURE [App::DocumentObjectGroupPython] Zr_element001  label="Zr_element : 1"  # scripted group (container) (typed FeaturePython)
  n = 1
  ref = Zr_element
FEATURE [App::DocumentObjectGroupPython] G4_Zr  # scripted group (container) (typed FeaturePython)
  Dunit = g/cm3
  Dvalue = 6.506
  Group = -> [Zr_element001]
  conduct = 2
  density = 1
  expand = 3
  formula = Zr
  name = G4_Zr
  specific = 4
FEATURE [App::DocumentObjectGroupPython] Nb_element001  label="Nb_element : 1"  # scripted group (container) (typed FeaturePython)
  n = 1
  ref = Nb_element
FEATURE [App::DocumentObjectGroupPython] G4_Nb  # scripted group (container) (typed FeaturePython)
  Dunit = g/cm3
  Dvalue = 8.57
  Group = -> [Nb_element001]
  conduct = 2
  density = 1
  expand = 3
  formula = Nb
  name = G4_Nb
  specific = 4
FEATURE [App::DocumentObjectGroupPython] Mo_element001  label="Mo_element : 1"  # scripted group (container) (typed FeaturePython)
  n = 1
  ref = Mo_element
FEATURE [App::DocumentObjectGroupPython] G4_Mo  # scripted group (container) (typed FeaturePython)
  Dunit = g/cm3
  Dvalue = 10.22
  Group = -> [Mo_element001]
  conduct = 2
  density = 1
  expand = 3
  formula = Mo
  name = G4_Mo
  specific = 4
FEATURE [App::DocumentObjectGroupPython] Tc_element001  label="Tc_element : 1"  # scripted group (container) (typed FeaturePython)
  n = 1
  ref = Tc_element
FEATURE [App::DocumentObjectGroupPython] G4_Tc  # scripted group (container) (typed FeaturePython)
  Dunit = g/cm3
  Dvalue = 11.5
  Group = -> [Tc_element001]
  conduct = 2
  density = 1
  expand = 3
  formula = Tc
  name = G4_Tc
  specific = 4
FEATURE [App::DocumentObjectGroupPython] Ru_element001  label="Ru_element : 1"  # scripted group (container) (typed FeaturePython)
  n = 1
  ref = Ru_element
FEATURE [App::DocumentObjectGroupPython] G4_Ru  # scripted group (container) (typed FeaturePython)
  Dunit = g/cm3
  Dvalue = 12.41
  Group = -> [Ru_element001]
  conduct = 2
  density = 1
  expand = 3
  formula = Ru
  name = G4_Ru
  specific = 4
FEATURE [App::DocumentObjectGroupPython] Rh_element001  label="Rh_element : 1"  # scripted group (container) (typed FeaturePython)
  n = 1
  ref = Rh_element
FEATURE [App::DocumentObjectGroupPython] G4_Rh  # scripted group (container) (typed FeaturePython)
  Dunit = g/cm3
  Dvalue = 12.41
  Group = -> [Rh_element001]
  conduct = 2
  density = 1
  expand = 3
  formula = Rh
  name = G4_Rh
  specific = 4
FEATURE [App::DocumentObjectGroupPython] Pd_element001  label="Pd_element : 1"  # scripted group (container) (typed FeaturePython)
  n = 1
  ref = Pd_element
FEATURE [App::DocumentObjectGroupPython] G4_Pd  # scripted group (container) (typed FeaturePython)
  Dunit = g/cm3
  Dvalue = 12.02
  Group = -> [Pd_element001]
  conduct = 2
  density = 1
  expand = 3
  formula = Pd
  name = G4_Pd
  specific = 4
FEATURE [App::DocumentObjectGroupPython] Ag_element006  label="Ag_element : 004"  # scripted group (container) (typed FeaturePython)
  n = 1
  ref = Ag_element
FEATURE [App::DocumentObjectGroupPython] G4_Ag  # scripted group (container) (typed FeaturePython)
  Dunit = g/cm3
  Dvalue = 10.5
  Group = -> [Ag_element006]
  conduct = 2
  density = 1
  expand = 3
  formula = Ag
  name = G4_Ag
  specific = 4
FEATURE [App::DocumentObjectGroupPython] Cd_element003  label="Cd_element : 003"  # scripted group (container) (typed FeaturePython)
  n = 1
  ref = Cd_element
FEATURE [App::DocumentObjectGroupPython] G4_Cd  # scripted group (container) (typed FeaturePython)
  Dunit = g/cm3
  Dvalue = 8.65
  Group = -> [Cd_element003]
  conduct = 2
  density = 1
  expand = 3
  formula = Cd
  name = G4_Cd
  specific = 4
FEATURE [App::DocumentObjectGroupPython] In_element001  label="In_element : 1"  # scripted group (container) (typed FeaturePython)
  n = 1
  ref = In_element
FEATURE [App::DocumentObjectGroupPython] G4_In  # scripted group (container) (typed FeaturePython)
  Dunit = g/cm3
  Dvalue = 7.31
  Group = -> [In_element001]
  conduct = 2
  density = 1
  expand = 3
  formula = In
  name = G4_In
  specific = 4
FEATURE [App::DocumentObjectGroupPython] Sn_element001  label="Sn_element : 1"  # scripted group (container) (typed FeaturePython)
  n = 1
  ref = Sn_element
FEATURE [App::DocumentObjectGroupPython] G4_Sn  # scripted group (container) (typed FeaturePython)
  Dunit = g/cm3
  Dvalue = 7.31
  Group = -> [Sn_element001]
  conduct = 2
  density = 1
  expand = 3
  formula = Sn
  name = G4_Sn
  specific = 4
FEATURE [App::DocumentObjectGroupPython] Sb_element001  label="Sb_element : 1"  # scripted group (container) (typed FeaturePython)
  n = 1
  ref = Sb_element
FEATURE [App::DocumentObjectGroupPython] G4_Sb  # scripted group (container) (typed FeaturePython)
  Dunit = g/cm3
  Dvalue = 6.691
  Group = -> [Sb_element001]
  conduct = 2
  density = 1
  expand = 3
  formula = Sb
  name = G4_Sb
  specific = 4
FEATURE [App::DocumentObjectGroupPython] Te_element002  label="Te_element : 002"  # scripted group (container) (typed FeaturePython)
  n = 1
  ref = Te_element
FEATURE [App::DocumentObjectGroupPython] G4_Te  # scripted group (container) (typed FeaturePython)
  Dunit = g/cm3
  Dvalue = 6.24
  Group = -> [Te_element002]
  conduct = 2
  density = 1
  expand = 3
  formula = Te
  name = G4_Te
  specific = 4
FEATURE [App::DocumentObjectGroupPython] I_element010  label="I_element : 006"  # scripted group (container) (typed FeaturePython)
  n = 1
  ref = I_element
FEATURE [App::DocumentObjectGroupPython] G4_I  # scripted group (container) (typed FeaturePython)
  Dunit = g/cm3
  Dvalue = 4.93
  Group = -> [I_element010]
  conduct = 2
  density = 1
  expand = 3
  formula = I
  name = G4_I
  specific = 4
FEATURE [App::DocumentObjectGroupPython] Xe_element001  label="Xe_element : 1"  # scripted group (container) (typed FeaturePython)
  n = 1
  ref = Xe_element
FEATURE [App::DocumentObjectGroupPython] G4_Xe  # scripted group (container) (typed FeaturePython)
  Dunit = g/cm3
  Dvalue = 0.00548536
  Group = -> [Xe_element001]
  conduct = 2
  density = 1
  expand = 3
  formula = Xe
  name = G4_Xe
  specific = 4
FEATURE [App::DocumentObjectGroupPython] Cs_element003  label="Cs_element : 003"  # scripted group (container) (typed FeaturePython)
  n = 1
  ref = Cs_element
FEATURE [App::DocumentObjectGroupPython] G4_Cs  # scripted group (container) (typed FeaturePython)
  Dunit = g/cm3
  Dvalue = 1.873
  Group = -> [Cs_element003]
  conduct = 2
  density = 1
  expand = 3
  formula = Cs
  name = G4_Cs
  specific = 4
FEATURE [App::DocumentObjectGroupPython] Ba_element003  label="Ba_element : 003"  # scripted group (container) (typed FeaturePython)
  n = 1
  ref = Ba_element
FEATURE [App::DocumentObjectGroupPython] G4_Ba  # scripted group (container) (typed FeaturePython)
  Dunit = g/cm3
  Dvalue = 3.5
  Group = -> [Ba_element003]
  conduct = 2
  density = 1
  expand = 3
  formula = Ba
  name = G4_Ba
  specific = 4
FEATURE [App::DocumentObjectGroupPython] La_element003  label="La_element : 003"  # scripted group (container) (typed FeaturePython)
  n = 1
  ref = La_element
FEATURE [App::DocumentObjectGroupPython] G4_La  # scripted group (container) (typed FeaturePython)
  Dunit = g/cm3
  Dvalue = 6.154
  Group = -> [La_element003]
  conduct = 2
  density = 1
  expand = 3
  formula = La
  name = G4_La
  specific = 4
FEATURE [App::DocumentObjectGroupPython] Ce_element002  label="Ce_element : 1"  # scripted group (container) (typed FeaturePython)
  n = 1
  ref = Ce_element
FEATURE [App::DocumentObjectGroupPython] G4_Ce  # scripted group (container) (typed FeaturePython)
  Dunit = g/cm3
  Dvalue = 6.657
  Group = -> [Ce_element002]
  conduct = 2
  density = 1
  expand = 3
  formula = Ce
  name = G4_Ce
  specific = 4
FEATURE [App::DocumentObjectGroupPython] Pr_element001  label="Pr_element : 1"  # scripted group (container) (typed FeaturePython)
  n = 1
  ref = Pr_element
FEATURE [App::DocumentObjectGroupPython] G4_Pr  # scripted group (container) (typed FeaturePython)
  Dunit = g/cm3
  Dvalue = 6.71
  Group = -> [Pr_element001]
  conduct = 2
  density = 1
  expand = 3
  formula = Pr
  name = G4_Pr
  specific = 4
FEATURE [App::DocumentObjectGroupPython] Nd_element001  label="Nd_element : 1"  # scripted group (container) (typed FeaturePython)
  n = 1
  ref = Nd_element
FEATURE [App::DocumentObjectGroupPython] G4_Nd  # scripted group (container) (typed FeaturePython)
  Dunit = g/cm3
  Dvalue = 6.9
  Group = -> [Nd_element001]
  conduct = 2
  density = 1
  expand = 3
  formula = Nd
  name = G4_Nd
  specific = 4
FEATURE [App::DocumentObjectGroupPython] Pm_element001  label="Pm_element : 1"  # scripted group (container) (typed FeaturePython)
  n = 1
  ref = Pm_element
FEATURE [App::DocumentObjectGroupPython] G4_Pm  # scripted group (container) (typed FeaturePython)
  Dunit = g/cm3
  Dvalue = 7.22
  Group = -> [Pm_element001]
  conduct = 2
  density = 1
  expand = 3
  formula = Pm
  name = G4_Pm
  specific = 4
FEATURE [App::DocumentObjectGroupPython] Sm_element001  label="Sm_element : 1"  # scripted group (container) (typed FeaturePython)
  n = 1
  ref = Sm_element
FEATURE [App::DocumentObjectGroupPython] G4_Sm  # scripted group (container) (typed FeaturePython)
  Dunit = g/cm3
  Dvalue = 7.46
  Group = -> [Sm_element001]
  conduct = 2
  density = 1
  expand = 3
  formula = Sm
  name = G4_Sm
  specific = 4
FEATURE [App::DocumentObjectGroupPython] Eu_element001  label="Eu_element : 1"  # scripted group (container) (typed FeaturePython)
  n = 1
  ref = Eu_element
FEATURE [App::DocumentObjectGroupPython] G4_Eu  # scripted group (container) (typed FeaturePython)
  Dunit = g/cm3
  Dvalue = 5.243
  Group = -> [Eu_element001]
  conduct = 2
  density = 1
  expand = 3
  formula = Eu
  name = G4_Eu
  specific = 4
FEATURE [App::DocumentObjectGroupPython] Gd_element002  label="Gd_element : 1"  # scripted group (container) (typed FeaturePython)
  n = 1
  ref = Gd_element
FEATURE [App::DocumentObjectGroupPython] G4_Gd  # scripted group (container) (typed FeaturePython)
  Dunit = g/cm3
  Dvalue = 7.9004
  Group = -> [Gd_element002]
  conduct = 2
  density = 1
  expand = 3
  formula = Gd
  name = G4_Gd
  specific = 4
FEATURE [App::DocumentObjectGroupPython] Tb_element001  label="Tb_element : 1"  # scripted group (container) (typed FeaturePython)
  n = 1
  ref = Tb_element
FEATURE [App::DocumentObjectGroupPython] G4_Tb  # scripted group (container) (typed FeaturePython)
  Dunit = g/cm3
  Dvalue = 8.229
  Group = -> [Tb_element001]
  conduct = 2
  density = 1
  expand = 3
  formula = Tb
  name = G4_Tb
  specific = 4
FEATURE [App::DocumentObjectGroupPython] Dy_element001  label="Dy_element : 1"  # scripted group (container) (typed FeaturePython)
  n = 1
  ref = Dy_element
FEATURE [App::DocumentObjectGroupPython] G4_Dy  # scripted group (container) (typed FeaturePython)
  Dunit = g/cm3
  Dvalue = 8.55
  Group = -> [Dy_element001]
  conduct = 2
  density = 1
  expand = 3
  formula = Dy
  name = G4_Dy
  specific = 4
FEATURE [App::DocumentObjectGroupPython] Ho_element001  label="Ho_element : 1"  # scripted group (container) (typed FeaturePython)
  n = 1
  ref = Ho_element
FEATURE [App::DocumentObjectGroupPython] G4_Ho  # scripted group (container) (typed FeaturePython)
  Dunit = g/cm3
  Dvalue = 8.795
  Group = -> [Ho_element001]
  conduct = 2
  density = 1
  expand = 3
  formula = Ho
  name = G4_Ho
  specific = 4
FEATURE [App::DocumentObjectGroupPython] Er_element001  label="Er_element : 1"  # scripted group (container) (typed FeaturePython)
  n = 1
  ref = Er_element
FEATURE [App::DocumentObjectGroupPython] G4_Er  # scripted group (container) (typed FeaturePython)
  Dunit = g/cm3
  Dvalue = 9.066
  Group = -> [Er_element001]
  conduct = 2
  density = 1
  expand = 3
  formula = Er
  name = G4_Er
  specific = 4
FEATURE [App::DocumentObjectGroupPython] Tm_element001  label="Tm_element : 1"  # scripted group (container) (typed FeaturePython)
  n = 1
  ref = Tm_element
FEATURE [App::DocumentObjectGroupPython] G4_Tm  # scripted group (container) (typed FeaturePython)
  Dunit = g/cm3
  Dvalue = 9.321
  Group = -> [Tm_element001]
  conduct = 2
  density = 1
  expand = 3
  formula = Tm
  name = G4_Tm
  specific = 4
FEATURE [App::DocumentObjectGroupPython] Yb_element001  label="Yb_element : 1"  # scripted group (container) (typed FeaturePython)
  n = 1
  ref = Yb_element
FEATURE [App::DocumentObjectGroupPython] G4_Yb  # scripted group (container) (typed FeaturePython)
  Dunit = g/cm3
  Dvalue = 6.73
  Group = -> [Yb_element001]
  conduct = 2
  density = 1
  expand = 3
  formula = Yb
  name = G4_Yb
  specific = 4
FEATURE [App::DocumentObjectGroupPython] Lu_element001  label="Lu_element : 1"  # scripted group (container) (typed FeaturePython)
  n = 1
  ref = Lu_element
FEATURE [App::DocumentObjectGroupPython] G4_Lu  # scripted group (container) (typed FeaturePython)
  Dunit = g/cm3
  Dvalue = 9.84
  Group = -> [Lu_element001]
  conduct = 2
  density = 1
  expand = 3
  formula = Lu
  name = G4_Lu
  specific = 4
FEATURE [App::DocumentObjectGroupPython] Hf_element001  label="Hf_element : 1"  # scripted group (container) (typed FeaturePython)
  n = 1
  ref = Hf_element
FEATURE [App::DocumentObjectGroupPython] G4_Hf  # scripted group (container) (typed FeaturePython)
  Dunit = g/cm3
  Dvalue = 13.31
  Group = -> [Hf_element001]
  conduct = 2
  density = 1
  expand = 3
  formula = Hf
  name = G4_Hf
  specific = 4
FEATURE [App::DocumentObjectGroupPython] Ta_element001  label="Ta_element : 1"  # scripted group (container) (typed FeaturePython)
  n = 1
  ref = Ta_element
FEATURE [App::DocumentObjectGroupPython] G4_Ta  # scripted group (container) (typed FeaturePython)
  Dunit = g/cm3
  Dvalue = 16.654
  Group = -> [Ta_element001]
  conduct = 2
  density = 1
  expand = 3
  formula = Ta
  name = G4_Ta
  specific = 4
FEATURE [App::DocumentObjectGroupPython] W_element004  label="W_element : 004"  # scripted group (container) (typed FeaturePython)
  n = 1
  ref = W_element
FEATURE [App::DocumentObjectGroupPython] G4_W  # scripted group (container) (typed FeaturePython)
  Dunit = g/cm3
  Dvalue = 19.3
  Group = -> [W_element004]
  conduct = 2
  density = 1
  expand = 3
  formula = W
  name = G4_W
  specific = 4
FEATURE [App::DocumentObjectGroupPython] Re_element001  label="Re_element : 1"  # scripted group (container) (typed FeaturePython)
  n = 1
  ref = Re_element
FEATURE [App::DocumentObjectGroupPython] G4_Re  # scripted group (container) (typed FeaturePython)
  Dunit = g/cm3
  Dvalue = 21.02
  Group = -> [Re_element001]
  conduct = 2
  density = 1
  expand = 3
  formula = Re
  name = G4_Re
  specific = 4
FEATURE [App::DocumentObjectGroupPython] Os_element001  label="Os_element : 1"  # scripted group (container) (typed FeaturePython)
  n = 1
  ref = Os_element
FEATURE [App::DocumentObjectGroupPython] G4_Os  # scripted group (container) (typed FeaturePython)
  Dunit = g/cm3
  Dvalue = 22.57
  Group = -> [Os_element001]
  conduct = 2
  density = 1
  expand = 3
  formula = Os
  name = G4_Os
  specific = 4
FEATURE [App::DocumentObjectGroupPython] Ir_element001  label="Ir_element : 1"  # scripted group (container) (typed FeaturePython)
  n = 1
  ref = Ir_element
FEATURE [App::DocumentObjectGroupPython] G4_Ir  # scripted group (container) (typed FeaturePython)
  Dunit = g/cm3
  Dvalue = 22.42
  Group = -> [Ir_element001]
  conduct = 2
  density = 1
  expand = 3
  formula = Ir
  name = G4_Ir
  specific = 4
FEATURE [App::DocumentObjectGroupPython] Pt_element001  label="Pt_element : 1"  # scripted group (container) (typed FeaturePython)
  n = 1
  ref = Pt_element
FEATURE [App::DocumentObjectGroupPython] G4_Pt  # scripted group (container) (typed FeaturePython)
  Dunit = g/cm3
  Dvalue = 21.45
  Group = -> [Pt_element001]
  conduct = 2
  density = 1
  expand = 3
  formula = Pt
  name = G4_Pt
  specific = 4
FEATURE [App::DocumentObjectGroupPython] Au_element001  label="Au_element : 1"  # scripted group (container) (typed FeaturePython)
  n = 1
  ref = Au_element
FEATURE [App::DocumentObjectGroupPython] G4_Au  # scripted group (container) (typed FeaturePython)
  Dunit = g/cm3
  Dvalue = 19.32
  Group = -> [Au_element001]
  conduct = 2
  density = 1
  expand = 3
  formula = Au
  name = G4_Au
  specific = 4
FEATURE [App::DocumentObjectGroupPython] Hg_element002  label="Hg_element : 002"  # scripted group (container) (typed FeaturePython)
  n = 1
  ref = Hg_element
FEATURE [App::DocumentObjectGroupPython] G4_Hg  # scripted group (container) (typed FeaturePython)
  Dunit = g/cm3
  Dvalue = 13.546
  Group = -> [Hg_element002]
  conduct = 2
  density = 1
  expand = 3
  formula = Hg
  name = G4_Hg
  specific = 4
FEATURE [App::DocumentObjectGroupPython] Tl_element002  label="Tl_element : 002"  # scripted group (container) (typed FeaturePython)
  n = 1
  ref = Tl_element
FEATURE [App::DocumentObjectGroupPython] G4_Tl  # scripted group (container) (typed FeaturePython)
  Dunit = g/cm3
  Dvalue = 11.72
  Group = -> [Tl_element002]
  conduct = 2
  density = 1
  expand = 3
  formula = Tl
  name = G4_Tl
  specific = 4
FEATURE [App::DocumentObjectGroupPython] Pb_element003  label="Pb_element : 1"  # scripted group (container) (typed FeaturePython)
  n = 1
  ref = Pb_element
FEATURE [App::DocumentObjectGroupPython] G4_Pb  # scripted group (container) (typed FeaturePython)
  Dunit = g/cm3
  Dvalue = 11.35
  Group = -> [Pb_element003]
  conduct = 2
  density = 1
  expand = 3
  formula = Pb
  name = G4_Pb
  specific = 4
FEATURE [App::DocumentObjectGroupPython] Bi_element002  label="Bi_element : 1"  # scripted group (container) (typed FeaturePython)
  n = 1
  ref = Bi_element
FEATURE [App::DocumentObjectGroupPython] G4_Bi  # scripted group (container) (typed FeaturePython)
  Dunit = g/cm3
  Dvalue = 9.747
  Group = -> [Bi_element002]
  conduct = 2
  density = 1
  expand = 3
  formula = Bi
  name = G4_Bi
  specific = 4
FEATURE [App::DocumentObjectGroupPython] Po_element001  label="Po_element : 1"  # scripted group (container) (typed FeaturePython)
  n = 1
  ref = Po_element
FEATURE [App::DocumentObjectGroupPython] G4_Po  # scripted group (container) (typed FeaturePython)
  Dunit = g/cm3
  Dvalue = 9.32
  Group = -> [Po_element001]
  conduct = 2
  density = 1
  expand = 3
  formula = Po
  name = G4_Po
  specific = 4
FEATURE [App::DocumentObjectGroupPython] At_element001  label="At_element : 1"  # scripted group (container) (typed FeaturePython)
  n = 1
  ref = At_element
FEATURE [App::DocumentObjectGroupPython] G4_At  # scripted group (container) (typed FeaturePython)
  Dunit = g/cm3
  Dvalue = 9.32
  Group = -> [At_element001]
  conduct = 2
  density = 1
  expand = 3
  formula = At
  name = G4_At
  specific = 4
FEATURE [App::DocumentObjectGroupPython] Rn_element001  label="Rn_element : 1"  # scripted group (container) (typed FeaturePython)
  n = 1
  ref = Rn_element
FEATURE [App::DocumentObjectGroupPython] G4_Rn  # scripted group (container) (typed FeaturePython)
  Dunit = g/cm3
  Dvalue = 0.00900662
  Group = -> [Rn_element001]
  conduct = 2
  density = 1
  expand = 3
  formula = Rn
  name = G4_Rn
  specific = 4
FEATURE [App::DocumentObjectGroupPython] Fr_element001  label="Fr_element : 1"  # scripted group (container) (typed FeaturePython)
  n = 1
  ref = Fr_element
FEATURE [App::DocumentObjectGroupPython] G4_Fr  # scripted group (container) (typed FeaturePython)
  Dunit = g/cm3
  Dvalue = 1
  Group = -> [Fr_element001]
  conduct = 2
  density = 1
  expand = 3
  formula = Fr
  name = G4_Fr
  specific = 4
FEATURE [App::DocumentObjectGroupPython] Ra_element001  label="Ra_element : 1"  # scripted group (container) (typed FeaturePython)
  n = 1
  ref = Ra_element
FEATURE [App::DocumentObjectGroupPython] G4_Ra  # scripted group (container) (typed FeaturePython)
  Dunit = g/cm3
  Dvalue = 5
  Group = -> [Ra_element001]
  conduct = 2
  density = 1
  expand = 3
  formula = Ra
  name = G4_Ra
  specific = 4
FEATURE [App::DocumentObjectGroupPython] Ac_element001  label="Ac_element : 1"  # scripted group (container) (typed FeaturePython)
  n = 1
  ref = Ac_element
FEATURE [App::DocumentObjectGroupPython] G4_Ac  # scripted group (container) (typed FeaturePython)
  Dunit = g/cm3
  Dvalue = 10.07
  Group = -> [Ac_element001]
  conduct = 2
  density = 1
  expand = 3
  formula = Ac
  name = G4_Ac
  specific = 4
FEATURE [App::DocumentObjectGroupPython] Th_element001  label="Th_element : 1"  # scripted group (container) (typed FeaturePython)
  n = 1
  ref = Th_element
FEATURE [App::DocumentObjectGroupPython] G4_Th  # scripted group (container) (typed FeaturePython)
  Dunit = g/cm3
  Dvalue = 11.72
  Group = -> [Th_element001]
  conduct = 2
  density = 1
  expand = 3
  formula = Th
  name = G4_Th
  specific = 4
FEATURE [App::DocumentObjectGroupPython] Pa_element001  label="Pa_element : 1"  # scripted group (container) (typed FeaturePython)
  n = 1
  ref = Pa_element
FEATURE [App::DocumentObjectGroupPython] G4_Pa  # scripted group (container) (typed FeaturePython)
  Dunit = g/cm3
  Dvalue = 15.37
  Group = -> [Pa_element001]
  conduct = 2
  density = 1
  expand = 3
  formula = Pa
  name = G4_Pa
  specific = 4
FEATURE [App::DocumentObjectGroupPython] U_element004  label="U_element : 004"  # scripted group (container) (typed FeaturePython)
  n = 1
  ref = U_element
FEATURE [App::DocumentObjectGroupPython] G4_U  # scripted group (container) (typed FeaturePython)
  Dunit = g/cm3
  Dvalue = 18.95
  Group = -> [U_element004]
  conduct = 2
  density = 1
  expand = 3
  formula = U
  name = G4_U
  specific = 4
FEATURE [App::DocumentObjectGroupPython] Np_element001  label="Np_element : 1"  # scripted group (container) (typed FeaturePython)
  n = 1
  ref = Np_element
FEATURE [App::DocumentObjectGroupPython] G4_Np  # scripted group (container) (typed FeaturePython)
  Dunit = g/cm3
  Dvalue = 20.25
  Group = -> [Np_element001]
  conduct = 2
  density = 1
  expand = 3
  formula = Np
  name = G4_Np
  specific = 4
FEATURE [App::DocumentObjectGroupPython] Pu_element002  label="Pu_element : 002"  # scripted group (container) (typed FeaturePython)
  n = 1
  ref = Pu_element
FEATURE [App::DocumentObjectGroupPython] G4_Pu  # scripted group (container) (typed FeaturePython)
  Dunit = g/cm3
  Dvalue = 19.84
  Group = -> [Pu_element002]
  conduct = 2
  density = 1
  expand = 3
  formula = Pu
  name = G4_Pu
  specific = 4
FEATURE [App::DocumentObjectGroupPython] Am_element001  label="Am_element : 1"  # scripted group (container) (typed FeaturePython)
  n = 1
  ref = Am_element
FEATURE [App::DocumentObjectGroupPython] G4_Am  # scripted group (container) (typed FeaturePython)
  Dunit = g/cm3
  Dvalue = 13.67
  Group = -> [Am_element001]
  conduct = 2
  density = 1
  expand = 3
  formula = Am
  name = G4_Am
  specific = 4
FEATURE [App::DocumentObjectGroupPython] Cm_element001  label="Cm_element : 1"  # scripted group (container) (typed FeaturePython)
  n = 1
  ref = Cm_element
FEATURE [App::DocumentObjectGroupPython] G4_Cm  # scripted group (container) (typed FeaturePython)
  Dunit = g/cm3
  Dvalue = 13.51
  Group = -> [Cm_element001]
  conduct = 2
  density = 1
  expand = 3
  formula = Cm
  name = G4_Cm
  specific = 4
FEATURE [App::DocumentObjectGroupPython] Bk_element001  label="Bk_element : 1"  # scripted group (container) (typed FeaturePython)
  n = 1
  ref = Bk_element
FEATURE [App::DocumentObjectGroupPython] G4_Bk  # scripted group (container) (typed FeaturePython)
  Dunit = g/cm3
  Dvalue = 14
  Group = -> [Bk_element001]
  conduct = 2
  density = 1
  expand = 3
  formula = Bk
  name = G4_Bk
  specific = 4
FEATURE [App::DocumentObjectGroupPython] Cf_element001  label="Cf_element : 1"  # scripted group (container) (typed FeaturePython)
  n = 1
  ref = Cf_element
FEATURE [App::DocumentObjectGroupPython] G4_Cf  # scripted group (container) (typed FeaturePython)
  Dunit = g/cm3
  Dvalue = 10
  Group = -> [Cf_element001]
  conduct = 2
  density = 1
  expand = 3
  formula = Cf
  name = G4_Cf
  specific = 4
FEATURE [App::DocumentObjectGroupPython] Element  # scripted group (container) (typed FeaturePython)
  Group = -> [G4_H,G4_He,G4_Li,G4_Be,G4_B,G4_C,G4_N,G4_O,G4_F,G4_Ne,G4_Na,G4_Mg,G4_Al,G4_Si,G4_P,G4_S,G4_Cl,G4_Ar,G4_K,G4_Ca,G4_Sc,G4_Ti,G4_V,G4_Cr,G4_Mn,G4_Fe,G4_Co,G4_Ni,G4_Cu,G4_Zn,G4_Ga,G4_Ge,G4_As,G4_Se,G4_Br,G4_Kr,G4_Rb,G4_Sr,G4_Y,G4_Zr,G4_Nb,G4_Mo,G4_Tc,G4_Ru,G4_Rh,G4_Pd,G4_Ag,G4_Cd,G4_In,G4_Sn,G4_Sb,G4_Te,G4_I,G4_Xe,G4_Cs,G4_Ba,G4_La,G4_Ce,G4_Pr,G4_Nd,G4_Pm,G4_Sm,G4_Eu,G4_Gd,G4_Tb,G4_Dy,G4_Ho,G4_Er,+30 more]
FEATURE [App::DocumentObjectGroupPython] H_element114  label="H_element : 063"  # scripted group (container) (typed FeaturePython)
  n = 2
  ref = H_element
FEATURE [App::DocumentObjectGroupPython] G4_lH2  # scripted group (container) (typed FeaturePython)
  Dunit = g/cm3
  Dvalue = 0.0708
  Group = -> [H_element114]
  conduct = 2
  density = 1
  expand = 3
  formula = G4_lH2
  name = G4_lH2
  specific = 4
FEATURE [App::DocumentObjectGroupPython] N_element049  label="N_element : 022"  # scripted group (container) (typed FeaturePython)
  n = 2
  ref = N_element
FEATURE [App::DocumentObjectGroupPython] G4_lN2  # scripted group (container) (typed FeaturePython)
  Dunit = g/cm3
  Dvalue = 0.807
  Group = -> [N_element049]
  conduct = 2
  density = 1
  expand = 3
  formula = G4_lN2
  name = G4_lN2
  specific = 4
FEATURE [App::DocumentObjectGroupPython] O_element106  label="O_element : 060"  # scripted group (container) (typed FeaturePython)
  n = 2
  ref = O_element
FEATURE [App::DocumentObjectGroupPython] G4_lO2  # scripted group (container) (typed FeaturePython)
  Dunit = g/cm3
  Dvalue = 1.141
  Group = -> [O_element106]
  conduct = 2
  density = 1
  expand = 3
  formula = G4_lO2
  name = G4_lO2
  specific = 4
FEATURE [App::DocumentObjectGroupPython] Ar  label="Ar : 1"  # scripted group (container) (typed FeaturePython)
  n = 1
  ref = Ar
FEATURE [App::DocumentObjectGroupPython] G4_lAr  # scripted group (container) (typed FeaturePython)
  Dunit = g/cm3
  Dvalue = 1.396
  Group = -> [Ar]
  conduct = 2
  density = 1
  expand = 3
  formula = G4_lAr
  name = G4_lAr
  specific = 4
FEATURE [App::DocumentObjectGroupPython] Br  label="Br : 1"  # scripted group (container) (typed FeaturePython)
  n = 1
  ref = Br
FEATURE [App::DocumentObjectGroupPython] G4_lBr  # scripted group (container) (typed FeaturePython)
  Dunit = g/cm3
  Dvalue = 3.1028
  Group = -> [Br]
  conduct = 2
  density = 1
  expand = 3
  formula = G4_lBr
  name = G4_lBr
  specific = 4
FEATURE [App::DocumentObjectGroupPython] Kr  label="Kr : 1"  # scripted group (container) (typed FeaturePython)
  n = 1
  ref = Kr
FEATURE [App::DocumentObjectGroupPython] G4_lKr  # scripted group (container) (typed FeaturePython)
  Dunit = g/cm3
  Dvalue = 2.418
  Group = -> [Kr]
  conduct = 2
  density = 1
  expand = 3
  formula = G4_lKr
  name = G4_lKr
  specific = 4
FEATURE [App::DocumentObjectGroupPython] Xe  label="Xe : 1"  # scripted group (container) (typed FeaturePython)
  n = 1
  ref = Xe
FEATURE [App::DocumentObjectGroupPython] G4_lXe  # scripted group (container) (typed FeaturePython)
  Dunit = g/cm3
  Dvalue = 2.953
  Group = -> [Xe]
  conduct = 2
  density = 1
  expand = 3
  formula = G4_lXe
  name = G4_lXe
  specific = 4
FEATURE [App::DocumentObjectGroupPython] O_element107  label="O_element : 061"  # scripted group (container) (typed FeaturePython)
  n = 4
  ref = O_element
FEATURE [App::DocumentObjectGroupPython] Pb_element004  label="Pb_element : 002"  # scripted group (container) (typed FeaturePython)
  n = 1
  ref = Pb_element
FEATURE [App::DocumentObjectGroupPython] W_element005  label="W_element : 005"  # scripted group (container) (typed FeaturePython)
  n = 1
  ref = W_element
FEATURE [App::DocumentObjectGroupPython] G4_PbWO4  # scripted group (container) (typed FeaturePython)
  Dunit = g/cm3
  Dvalue = 8.28
  Group = -> [O_element107,Pb_element004,W_element005]
  conduct = 2
  density = 1
  expand = 3
  formula = G4_PbWO4
  name = G4_PbWO4
  specific = 4
FEATURE [App::DocumentObjectGroupPython] alactic  label="alactic : 1"  # scripted group (container) (typed FeaturePython)
  n = 1
  ref = alactic
FEATURE [App::DocumentObjectGroupPython] G4_Galactic  # scripted group (container) (typed FeaturePython)
  Dunit = g/cm3
  Dvalue = 0
  Group = -> [alactic]
  conduct = 2
  density = 1
  expand = 3
  formula = G4_Galactic
  name = G4_Galactic
  specific = 4
FEATURE [App::DocumentObjectGroupPython] RAPHITE_POROUS  label="RAPHITE_POROUS : 1"  # scripted group (container) (typed FeaturePython)
  n = 1
  ref = RAPHITE_POROUS
FEATURE [App::DocumentObjectGroupPython] G4_GRAPHITE_POROUS  # scripted group (container) (typed FeaturePython)
  Dunit = g/cm3
  Dvalue = 1.7
  Group = -> [RAPHITE_POROUS]
  conduct = 2
  density = 1
  expand = 3
  formula = G4_GRAPHITE_POROUS
  name = G4_GRAPHITE_POROUS
  specific = 4
FEATURE [App::DocumentObjectGroupPython] H_element115  label="H_element : 0.150"  # scripted group (container) (typed FeaturePython)
  n = 0.080538
FEATURE [App::DocumentObjectGroupPython] C_element125  label="C_element : 0.600"  # scripted group (container) (typed FeaturePython)
  n = 0.599848
FEATURE [App::DocumentObjectGroupPython] O_element108  label="O_element : 0.320"  # scripted group (container) (typed FeaturePython)
  n = 0.319614
FEATURE [App::DocumentObjectGroupPython] G4_LUCITE  # scripted group (container) (typed FeaturePython)
  Dunit = g/cm3
  Dvalue = 1.19
  Group = -> [H_element115,C_element125,O_element108]
  conduct = 2
  density = 1
  expand = 3
  formula = G4_LUCITE
  name = G4_LUCITE
  specific = 4
FEATURE [App::DocumentObjectGroupPython] Cu_element002  label="Cu_element : 62"  # scripted group (container) (typed FeaturePython)
  n = 62
  ref = Cu_element
FEATURE [App::DocumentObjectGroupPython] Zn_element002  label="Zn_element : 35"  # scripted group (container) (typed FeaturePython)
  n = 35
  ref = Zn_element
FEATURE [App::DocumentObjectGroupPython] Pb_element005  label="Pb_element : 3"  # scripted group (container) (typed FeaturePython)
  n = 3
  ref = Pb_element
FEATURE [App::DocumentObjectGroupPython] G4_BRASS  # scripted group (container) (typed FeaturePython)
  Dunit = g/cm3
  Dvalue = 8.52
  Group = -> [Cu_element002,Zn_element002,Pb_element005]
  conduct = 2
  density = 1
  expand = 3
  formula = G4_BRASS
  name = G4_BRASS
  specific = 4
FEATURE [App::DocumentObjectGroupPython] Cu_element003  label="Cu_element : 89"  # scripted group (container) (typed FeaturePython)
  n = 89
  ref = Cu_element
FEATURE [App::DocumentObjectGroupPython] Zn_element003  label="Zn_element : 9"  # scripted group (container) (typed FeaturePython)
  n = 9
  ref = Zn_element
FEATURE [App::DocumentObjectGroupPython] Pb_element006  label="Pb_element : 2"  # scripted group (container) (typed FeaturePython)
  n = 2
  ref = Pb_element
FEATURE [App::DocumentObjectGroupPython] G4_BRONZE  # scripted group (container) (typed FeaturePython)
  Dunit = g/cm3
  Dvalue = 8.82
  Group = -> [Cu_element003,Zn_element003,Pb_element006]
  conduct = 2
  density = 1
  expand = 3
  formula = G4_BRONZE
  name = G4_BRONZE
  specific = 4
FEATURE [App::DocumentObjectGroupPython] Fe_element008  label="Fe_element : 74"  # scripted group (container) (typed FeaturePython)
  n = 74
  ref = Fe_element
FEATURE [App::DocumentObjectGroupPython] Cr_element002  label="Cr_element : 18"  # scripted group (container) (typed FeaturePython)
  n = 18
  ref = Cr_element
FEATURE [App::DocumentObjectGroupPython] Ni_element002  label="Ni_element : 8"  # scripted group (container) (typed FeaturePython)
  n = 8
  ref = Ni_element
FEATURE [App::DocumentObjectGroupPython] G4_STAINLESS_STEEL  label="G4_STAINLESS-STEEL"  # scripted group (container) (typed FeaturePython)
  Dunit = g/cm3
  Dvalue = 8
  Group = -> [Fe_element008,Cr_element002,Ni_element002]
  conduct = 2
  density = 1
  expand = 3
  formula = G4_STAINLESS-STEEL
  name = G4_STAINLESS-STEEL
  specific = 4
FEATURE [App::DocumentObjectGroupPython] H_element116  label="H_element : 064"  # scripted group (container) (typed FeaturePython)
  n = 18
  ref = H_element
FEATURE [App::DocumentObjectGroupPython] C_element126  label="C_element : 071"  # scripted group (container) (typed FeaturePython)
  n = 12
  ref = C_element
FEATURE [App::DocumentObjectGroupPython] O_element109  label="O_element : 062"  # scripted group (container) (typed FeaturePython)
  n = 7
  ref = O_element
FEATURE [App::DocumentObjectGroupPython] G4_CR39  # scripted group (container) (typed FeaturePython)
  Dunit = g/cm3
  Dvalue = 1.32
  Group = -> [H_element116,C_element126,O_element109]
  conduct = 2
  density = 1
  expand = 3
  formula = G4_CR39
  name = G4_CR39
  specific = 4
FEATURE [App::DocumentObjectGroupPython] H_element117  label="H_element : 38"  # scripted group (container) (typed FeaturePython)
  n = 38
  ref = H_element
FEATURE [App::DocumentObjectGroupPython] C_element127  label="C_element : 072"  # scripted group (container) (typed FeaturePython)
  n = 18
  ref = C_element
FEATURE [App::DocumentObjectGroupPython] O_element110  label="O_element : 063"  # scripted group (container) (typed FeaturePython)
  n = 1
  ref = O_element
FEATURE [App::DocumentObjectGroupPython] G4_OCTADECANOL  # scripted group (container) (typed FeaturePython)
  Dunit = g/cm3
  Dvalue = 0.812
  Group = -> [H_element117,C_element127,O_element110]
  conduct = 2
  density = 1
  expand = 3
  formula = G4_OCTADECANOL
  name = G4_OCTADECANOL
  specific = 4
FEATURE [App::DocumentObjectGroupPython] HEP  # scripted group (container) (typed FeaturePython)
  Group = -> [G4_lH2,G4_lN2,G4_lO2,G4_lAr,G4_lBr,G4_lKr,G4_lXe,G4_PbWO4,G4_Galactic,G4_GRAPHITE_POROUS,G4_LUCITE,G4_BRASS,G4_BRONZE,G4_STAINLESS_STEEL,G4_CR39,G4_OCTADECANOL]
FEATURE [App::DocumentObjectGroupPython] C_element128  label="C_element : 073"  # scripted group (container) (typed FeaturePython)
  n = 14
  ref = C_element
FEATURE [App::DocumentObjectGroupPython] H_element118  label="H_element : 065"  # scripted group (container) (typed FeaturePython)
  n = 10
  ref = H_element
FEATURE [App::DocumentObjectGroupPython] O_element111  label="O_element : 064"  # scripted group (container) (typed FeaturePython)
  n = 2
  ref = O_element
FEATURE [App::DocumentObjectGroupPython] N_element050  label="N_element : 023"  # scripted group (container) (typed FeaturePython)
  n = 2
  ref = N_element
FEATURE [App::DocumentObjectGroupPython] G4_KEVLAR  # scripted group (container) (typed FeaturePython)
  Dunit = g/cm3
  Dvalue = 1.44
  Group = -> [C_element128,H_element118,O_element111,N_element050]
  conduct = 2
  density = 1
  expand = 3
  formula = G4_KEVLAR
  name = G4_KEVLAR
  specific = 4
FEATURE [App::DocumentObjectGroupPython] C_element129  label="C_element : 074"  # scripted group (container) (typed FeaturePython)
  n = 10
  ref = C_element
FEATURE [App::DocumentObjectGroupPython] H_element119  label="H_element : 066"  # scripted group (container) (typed FeaturePython)
  n = 8
  ref = H_element
FEATURE [App::DocumentObjectGroupPython] O_element112  label="O_element : 065"  # scripted group (container) (typed FeaturePython)
  n = 4
  ref = O_element
FEATURE [App::DocumentObjectGroupPython] G4_DACRON  # scripted group (container) (typed FeaturePython)
  Dunit = g/cm3
  Dvalue = 1.4
  Group = -> [C_element129,H_element119,O_element112]
  conduct = 2
  density = 1
  expand = 3
  formula = G4_DACRON
  name = G4_DACRON
  specific = 4
FEATURE [App::DocumentObjectGroupPython] C_element130  label="C_element : 075"  # scripted group (container) (typed FeaturePython)
  n = 4
  ref = C_element
FEATURE [App::DocumentObjectGroupPython] H_element120  label="H_element : 067"  # scripted group (container) (typed FeaturePython)
  n = 5
  ref = H_element
FEATURE [App::DocumentObjectGroupPython] Cl_element030  label="Cl_element : 016"  # scripted group (container) (typed FeaturePython)
  n = 1
  ref = Cl_element
FEATURE [App::DocumentObjectGroupPython] G4_NEOPRENE  # scripted group (container) (typed FeaturePython)
  Dunit = g/cm3
  Dvalue = 1.23
  Group = -> [C_element130,H_element120,Cl_element030]
  conduct = 2
  density = 1
  expand = 3
  formula = G4_NEOPRENE
  name = G4_NEOPRENE
  specific = 4
FEATURE [App::DocumentObjectGroupPython] Space  # scripted group (container) (typed FeaturePython)
  Group = -> [G4_KEVLAR,G4_DACRON,G4_NEOPRENE]
FEATURE [App::DocumentObjectGroupPython] H_element121  label="H_element : 068"  # scripted group (container) (typed FeaturePython)
  n = 5
  ref = H_element
FEATURE [App::DocumentObjectGroupPython] C_element131  label="C_element : 076"  # scripted group (container) (typed FeaturePython)
  n = 4
  ref = C_element
FEATURE [App::DocumentObjectGroupPython] N_element051  label="N_element : 3"  # scripted group (container) (typed FeaturePython)
  n = 3
  ref = N_element
FEATURE [App::DocumentObjectGroupPython] O_element113  label="O_element : 066"  # scripted group (container) (typed FeaturePython)
  n = 1
  ref = O_element
FEATURE [App::DocumentObjectGroupPython] G4_CYTOSINE  # scripted group (container) (typed FeaturePython)
  Dunit = g/cm3
  Dvalue = 1.55
  Group = -> [H_element121,C_element131,N_element051,O_element113]
  conduct = 2
  density = 1
  expand = 3
  formula = G4_CYTOSINE
  name = G4_CYTOSINE
  specific = 4
FEATURE [App::DocumentObjectGroupPython] H_element122  label="H_element : 069"  # scripted group (container) (typed FeaturePython)
  n = 6
  ref = H_element
FEATURE [App::DocumentObjectGroupPython] C_element132  label="C_element : 077"  # scripted group (container) (typed FeaturePython)
  n = 5
  ref = C_element
FEATURE [App::DocumentObjectGroupPython] N_element052  label="N_element : 024"  # scripted group (container) (typed FeaturePython)
  n = 2
  ref = N_element
FEATURE [App::DocumentObjectGroupPython] O_element114  label="O_element : 067"  # scripted group (container) (typed FeaturePython)
  n = 2
  ref = O_element
FEATURE [App::DocumentObjectGroupPython] G4_THYMINE  # scripted group (container) (typed FeaturePython)
  Dunit = g/cm3
  Dvalue = 1.23
  Group = -> [H_element122,C_element132,N_element052,O_element114]
  conduct = 2
  density = 1
  expand = 3
  formula = G4_THYMINE
  name = G4_THYMINE
  specific = 4
FEATURE [App::DocumentObjectGroupPython] H_element123  label="H_element : 070"  # scripted group (container) (typed FeaturePython)
  n = 4
  ref = H_element
FEATURE [App::DocumentObjectGroupPython] C_element133  label="C_element : 078"  # scripted group (container) (typed FeaturePython)
  n = 4
  ref = C_element
FEATURE [App::DocumentObjectGroupPython] N_element053  label="N_element : 025"  # scripted group (container) (typed FeaturePython)
  n = 2
  ref = N_element
FEATURE [App::DocumentObjectGroupPython] O_element115  label="O_element : 068"  # scripted group (container) (typed FeaturePython)
  n = 2
  ref = O_element
FEATURE [App::DocumentObjectGroupPython] G4_URACIL  # scripted group (container) (typed FeaturePython)
  Dunit = g/cm3
  Dvalue = 1.32
  Group = -> [H_element123,C_element133,N_element053,O_element115]
  conduct = 2
  density = 1
  expand = 3
  formula = G4_URACIL
  name = G4_URACIL
  specific = 4
FEATURE [App::DocumentObjectGroupPython] H_element124  label="H_element : 071"  # scripted group (container) (typed FeaturePython)
  n = 4
  ref = H_element
FEATURE [App::DocumentObjectGroupPython] C_element134  label="C_element : 079"  # scripted group (container) (typed FeaturePython)
  n = 5
  ref = C_element
FEATURE [App::DocumentObjectGroupPython] N_element054  label="N_element : 026"  # scripted group (container) (typed FeaturePython)
  n = 5
  ref = N_element
FEATURE [App::DocumentObjectGroupPython] G4_DNA_ADENINE  # scripted group (container) (typed FeaturePython)
  Dunit = g/cm3
  Dvalue = 1
  Group = -> [H_element124,C_element134,N_element054]
  conduct = 2
  density = 1
  expand = 3
  formula = G4_DNA_ADENINE
  name = G4_DNA_ADENINE
  specific = 4
FEATURE [App::DocumentObjectGroupPython] H_element125  label="H_element : 072"  # scripted group (container) (typed FeaturePython)
  n = 4
  ref = H_element
FEATURE [App::DocumentObjectGroupPython] C_element135  label="C_element : 080"  # scripted group (container) (typed FeaturePython)
  n = 5
  ref = C_element
FEATURE [App::DocumentObjectGroupPython] N_element055  label="N_element : 027"  # scripted group (container) (typed FeaturePython)
  n = 5
  ref = N_element
FEATURE [App::DocumentObjectGroupPython] O_element116  label="O_element : 069"  # scripted group (container) (typed FeaturePython)
  n = 1
  ref = O_element
FEATURE [App::DocumentObjectGroupPython] G4_DNA_GUANINE  # scripted group (container) (typed FeaturePython)
  Dunit = g/cm3
  Dvalue = 1
  Group = -> [H_element125,C_element135,N_element055,O_element116]
  conduct = 2
  density = 1
  expand = 3
  formula = G4_DNA_GUANINE
  name = G4_DNA_GUANINE
  specific = 4
FEATURE [App::DocumentObjectGroupPython] H_element126  label="H_element : 073"  # scripted group (container) (typed FeaturePython)
  n = 4
  ref = H_element
FEATURE [App::DocumentObjectGroupPython] C_element136  label="C_element : 081"  # scripted group (container) (typed FeaturePython)
  n = 4
  ref = C_element
FEATURE [App::DocumentObjectGroupPython] N_element056  label="N_element : 028"  # scripted group (container) (typed FeaturePython)
  n = 3
  ref = N_element
FEATURE [App::DocumentObjectGroupPython] O_element117  label="O_element : 070"  # scripted group (container) (typed FeaturePython)
  n = 1
  ref = O_element
FEATURE [App::DocumentObjectGroupPython] G4_DNA_CYTOSINE  # scripted group (container) (typed FeaturePython)
  Dunit = g/cm3
  Dvalue = 1
  Group = -> [H_element126,C_element136,N_element056,O_element117]
  conduct = 2
  density = 1
  expand = 3
  formula = G4_DNA_CYTOSINE
  name = G4_DNA_CYTOSINE
  specific = 4
FEATURE [App::DocumentObjectGroupPython] H_element127  label="H_element : 074"  # scripted group (container) (typed FeaturePython)
  n = 5
  ref = H_element
FEATURE [App::DocumentObjectGroupPython] C_element137  label="C_element : 082"  # scripted group (container) (typed FeaturePython)
  n = 5
  ref = C_element
FEATURE [App::DocumentObjectGroupPython] N_element057  label="N_element : 029"  # scripted group (container) (typed FeaturePython)
  n = 2
  ref = N_element
FEATURE [App::DocumentObjectGroupPython] O_element118  label="O_element : 071"  # scripted group (container) (typed FeaturePython)
  n = 2
  ref = O_element
FEATURE [App::DocumentObjectGroupPython] G4_DNA_THYMINE  # scripted group (container) (typed FeaturePython)
  Dunit = g/cm3
  Dvalue = 1
  Group = -> [H_element127,C_element137,N_element057,O_element118]
  conduct = 2
  density = 1
  expand = 3
  formula = G4_DNA_THYMINE
  name = G4_DNA_THYMINE
  specific = 4
FEATURE [App::DocumentObjectGroupPython] H_element128  label="H_element : 075"  # scripted group (container) (typed FeaturePython)
  n = 3
  ref = H_element
FEATURE [App::DocumentObjectGroupPython] C_element138  label="C_element : 083"  # scripted group (container) (typed FeaturePython)
  n = 4
  ref = C_element
FEATURE [App::DocumentObjectGroupPython] N_element058  label="N_element : 030"  # scripted group (container) (typed FeaturePython)
  n = 2
  ref = N_element
FEATURE [App::DocumentObjectGroupPython] O_element119  label="O_element : 072"  # scripted group (container) (typed FeaturePython)
  n = 2
  ref = O_element
FEATURE [App::DocumentObjectGroupPython] G4_DNA_URACIL  # scripted group (container) (typed FeaturePython)
  Dunit = g/cm3
  Dvalue = 1
  Group = -> [H_element128,C_element138,N_element058,O_element119]
  conduct = 2
  density = 1
  expand = 3
  formula = G4_DNA_URACIL
  name = G4_DNA_URACIL
  specific = 4
FEATURE [App::DocumentObjectGroupPython] H_element129  label="H_element : 076"  # scripted group (container) (typed FeaturePython)
  n = 10
  ref = H_element
FEATURE [App::DocumentObjectGroupPython] C_element139  label="C_element : 084"  # scripted group (container) (typed FeaturePython)
  n = 10
  ref = C_element
FEATURE [App::DocumentObjectGroupPython] N_element059  label="N_element : 031"  # scripted group (container) (typed FeaturePython)
  n = 5
  ref = N_element
FEATURE [App::DocumentObjectGroupPython] O_element120  label="O_element : 073"  # scripted group (container) (typed FeaturePython)
  n = 4
  ref = O_element
FEATURE [App::DocumentObjectGroupPython] G4_DNA_ADENOSINE  # scripted group (container) (typed FeaturePython)
  Dunit = g/cm3
  Dvalue = 1
  Group = -> [H_element129,C_element139,N_element059,O_element120]
  conduct = 2
  density = 1
  expand = 3
  formula = G4_DNA_ADENOSINE
  name = G4_DNA_ADENOSINE
  specific = 4
FEATURE [App::DocumentObjectGroupPython] H_element130  label="H_element : 077"  # scripted group (container) (typed FeaturePython)
  n = 10
  ref = H_element
FEATURE [App::DocumentObjectGroupPython] C_element140  label="C_element : 085"  # scripted group (container) (typed FeaturePython)
  n = 10
  ref = C_element
FEATURE [App::DocumentObjectGroupPython] N_element060  label="N_element : 032"  # scripted group (container) (typed FeaturePython)
  n = 5
  ref = N_element
FEATURE [App::DocumentObjectGroupPython] O_element121  label="O_element : 074"  # scripted group (container) (typed FeaturePython)
  n = 5
  ref = O_element
FEATURE [App::DocumentObjectGroupPython] G4_DNA_GUANOSINE  # scripted group (container) (typed FeaturePython)
  Dunit = g/cm3
  Dvalue = 1
  Group = -> [H_element130,C_element140,N_element060,O_element121]
  conduct = 2
  density = 1
  expand = 3
  formula = G4_DNA_GUANOSINE
  name = G4_DNA_GUANOSINE
  specific = 4
FEATURE [App::DocumentObjectGroupPython] H_element131  label="H_element : 078"  # scripted group (container) (typed FeaturePython)
  n = 10
  ref = H_element
FEATURE [App::DocumentObjectGroupPython] C_element141  label="C_element : 086"  # scripted group (container) (typed FeaturePython)
  n = 9
  ref = C_element
FEATURE [App::DocumentObjectGroupPython] N_element061  label="N_element : 033"  # scripted group (container) (typed FeaturePython)
  n = 3
  ref = N_element
FEATURE [App::DocumentObjectGroupPython] O_element122  label="O_element : 075"  # scripted group (container) (typed FeaturePython)
  n = 5
  ref = O_element
FEATURE [App::DocumentObjectGroupPython] G4_DNA_CYTIDINE  # scripted group (container) (typed FeaturePython)
  Dunit = g/cm3
  Dvalue = 1
  Group = -> [H_element131,C_element141,N_element061,O_element122]
  conduct = 2
  density = 1
  expand = 3
  formula = G4_DNA_CYTIDINE
  name = G4_DNA_CYTIDINE
  specific = 4
FEATURE [App::DocumentObjectGroupPython] H_element132  label="H_element : 079"  # scripted group (container) (typed FeaturePython)
  n = 9
  ref = H_element
FEATURE [App::DocumentObjectGroupPython] C_element142  label="C_element : 087"  # scripted group (container) (typed FeaturePython)
  n = 9
  ref = C_element
FEATURE [App::DocumentObjectGroupPython] N_element062  label="N_element : 034"  # scripted group (container) (typed FeaturePython)
  n = 2
  ref = N_element
FEATURE [App::DocumentObjectGroupPython] O_element123  label="O_element : 076"  # scripted group (container) (typed FeaturePython)
  n = 6
  ref = O_element
FEATURE [App::DocumentObjectGroupPython] G4_DNA_URIDINE  # scripted group (container) (typed FeaturePython)
  Dunit = g/cm3
  Dvalue = 1
  Group = -> [H_element132,C_element142,N_element062,O_element123]
  conduct = 2
  density = 1
  expand = 3
  formula = G4_DNA_URIDINE
  name = G4_DNA_URIDINE
  specific = 4
FEATURE [App::DocumentObjectGroupPython] H_element133  label="H_element : 080"  # scripted group (container) (typed FeaturePython)
  n = 11
  ref = H_element
FEATURE [App::DocumentObjectGroupPython] C_element143  label="C_element : 088"  # scripted group (container) (typed FeaturePython)
  n = 10
  ref = C_element
FEATURE [App::DocumentObjectGroupPython] N_element063  label="N_element : 035"  # scripted group (container) (typed FeaturePython)
  n = 2
  ref = N_element
FEATURE [App::DocumentObjectGroupPython] O_element124  label="O_element : 077"  # scripted group (container) (typed FeaturePython)
  n = 6
  ref = O_element
FEATURE [App::DocumentObjectGroupPython] G4_DNA_METHYLURIDINE  # scripted group (container) (typed FeaturePython)
  Dunit = g/cm3
  Dvalue = 1
  Group = -> [H_element133,C_element143,N_element063,O_element124]
  conduct = 2
  density = 1
  expand = 3
  formula = G4_DNA_METHYLURIDINE
  name = G4_DNA_METHYLURIDINE
  specific = 4
FEATURE [App::DocumentObjectGroupPython] P_element014  label="P_element : 003"  # scripted group (container) (typed FeaturePython)
  n = 1
  ref = P_element
FEATURE [App::DocumentObjectGroupPython] O_element125  label="O_element : 078"  # scripted group (container) (typed FeaturePython)
  n = 3
  ref = O_element
FEATURE [App::DocumentObjectGroupPython] G4_DNA_MONOPHOSPHATE  # scripted group (container) (typed FeaturePython)
  Dunit = g/cm3
  Dvalue = 1
  Group = -> [P_element014,O_element125]
  conduct = 2
  density = 1
  expand = 3
  formula = G4_DNA_MONOPHOSPHATE
  name = G4_DNA_MONOPHOSPHATE
  specific = 4
FEATURE [App::DocumentObjectGroupPython] H_element134  label="H_element : 081"  # scripted group (container) (typed FeaturePython)
  n = 10
  ref = H_element
FEATURE [App::DocumentObjectGroupPython] C_element144  label="C_element : 089"  # scripted group (container) (typed FeaturePython)
  n = 10
  ref = C_element
FEATURE [App::DocumentObjectGroupPython] N_element064  label="N_element : 036"  # scripted group (container) (typed FeaturePython)
  n = 5
  ref = N_element
FEATURE [App::DocumentObjectGroupPython] O_element126  label="O_element : 079"  # scripted group (container) (typed FeaturePython)
  n = 7
  ref = O_element
FEATURE [App::DocumentObjectGroupPython] P_element015  label="P_element : 004"  # scripted group (container) (typed FeaturePython)
  n = 1
  ref = P_element
FEATURE [App::DocumentObjectGroupPython] G4_DNA_A  # scripted group (container) (typed FeaturePython)
  Dunit = g/cm3
  Dvalue = 1
  Group = -> [H_element134,C_element144,N_element064,O_element126,P_element015]
  conduct = 2
  density = 1
  expand = 3
  formula = G4_DNA_A
  name = G4_DNA_A
  specific = 4
FEATURE [App::DocumentObjectGroupPython] H_element135  label="H_element : 082"  # scripted group (container) (typed FeaturePython)
  n = 10
  ref = H_element
FEATURE [App::DocumentObjectGroupPython] C_element145  label="C_element : 090"  # scripted group (container) (typed FeaturePython)
  n = 10
  ref = C_element
FEATURE [App::DocumentObjectGroupPython] N_element065  label="N_element : 037"  # scripted group (container) (typed FeaturePython)
  n = 5
  ref = N_element
FEATURE [App::DocumentObjectGroupPython] O_element127  label="O_element : 8"  # scripted group (container) (typed FeaturePython)
  n = 8
  ref = O_element
FEATURE [App::DocumentObjectGroupPython] P_element016  label="P_element : 005"  # scripted group (container) (typed FeaturePython)
  n = 1
  ref = P_element
FEATURE [App::DocumentObjectGroupPython] G4_DNA_G  # scripted group (container) (typed FeaturePython)
  Dunit = g/cm3
  Dvalue = 1
  Group = -> [H_element135,C_element145,N_element065,O_element127,P_element016]
  conduct = 2
  density = 1
  expand = 3
  formula = G4_DNA_G
  name = G4_DNA_G
  specific = 4
FEATURE [App::DocumentObjectGroupPython] H_element136  label="H_element : 083"  # scripted group (container) (typed FeaturePython)
  n = 10
  ref = H_element
FEATURE [App::DocumentObjectGroupPython] C_element146  label="C_element : 091"  # scripted group (container) (typed FeaturePython)
  n = 9
  ref = C_element
FEATURE [App::DocumentObjectGroupPython] N_element066  label="N_element : 038"  # scripted group (container) (typed FeaturePython)
  n = 3
  ref = N_element
FEATURE [App::DocumentObjectGroupPython] O_element128  label="O_element : 080"  # scripted group (container) (typed FeaturePython)
  n = 8
  ref = O_element
FEATURE [App::DocumentObjectGroupPython] P_element017  label="P_element : 006"  # scripted group (container) (typed FeaturePython)
  n = 1
  ref = P_element
FEATURE [App::DocumentObjectGroupPython] G4_DNA_C  # scripted group (container) (typed FeaturePython)
  Dunit = g/cm3
  Dvalue = 1
  Group = -> [H_element136,C_element146,N_element066,O_element128,P_element017]
  conduct = 2
  density = 1
  expand = 3
  formula = G4_DNA_C
  name = G4_DNA_C
  specific = 4
FEATURE [App::DocumentObjectGroupPython] H_element137  label="H_element : 084"  # scripted group (container) (typed FeaturePython)
  n = 9
  ref = H_element
FEATURE [App::DocumentObjectGroupPython] C_element147  label="C_element : 092"  # scripted group (container) (typed FeaturePython)
  n = 9
  ref = C_element
FEATURE [App::DocumentObjectGroupPython] N_element067  label="N_element : 039"  # scripted group (container) (typed FeaturePython)
  n = 2
  ref = N_element
FEATURE [App::DocumentObjectGroupPython] O_element129  label="O_element : 9"  # scripted group (container) (typed FeaturePython)
  n = 9
  ref = O_element
FEATURE [App::DocumentObjectGroupPython] P_element018  label="P_element : 007"  # scripted group (container) (typed FeaturePython)
  n = 1
  ref = P_element
FEATURE [App::DocumentObjectGroupPython] G4_DNA_U  # scripted group (container) (typed FeaturePython)
  Dunit = g/cm3
  Dvalue = 1
  Group = -> [H_element137,C_element147,N_element067,O_element129,P_element018]
  conduct = 2
  density = 1
  expand = 3
  formula = G4_DNA_U
  name = G4_DNA_U
  specific = 4
FEATURE [App::DocumentObjectGroupPython] H_element138  label="H_element : 085"  # scripted group (container) (typed FeaturePython)
  n = 11
  ref = H_element
FEATURE [App::DocumentObjectGroupPython] C_element148  label="C_element : 093"  # scripted group (container) (typed FeaturePython)
  n = 10
  ref = C_element
FEATURE [App::DocumentObjectGroupPython] N_element068  label="N_element : 040"  # scripted group (container) (typed FeaturePython)
  n = 2
  ref = N_element
FEATURE [App::DocumentObjectGroupPython] O_element130  label="O_element : 081"  # scripted group (container) (typed FeaturePython)
  n = 9
  ref = O_element
FEATURE [App::DocumentObjectGroupPython] P_element019  label="P_element : 008"  # scripted group (container) (typed FeaturePython)
  n = 1
  ref = P_element
FEATURE [App::DocumentObjectGroupPython] G4_DNA_MU  # scripted group (container) (typed FeaturePython)
  Dunit = g/cm3
  Dvalue = 1
  Group = -> [H_element138,C_element148,N_element068,O_element130,P_element019]
  conduct = 2
  density = 1
  expand = 3
  formula = G4_DNA_MU
  name = G4_DNA_MU
  specific = 4
FEATURE [App::DocumentObjectGroupPython] BioChemical  # scripted group (container) (typed FeaturePython)
  Group = -> [G4_CYTOSINE,G4_THYMINE,G4_URACIL,G4_DNA_ADENINE,G4_DNA_GUANINE,G4_DNA_CYTOSINE,G4_DNA_THYMINE,G4_DNA_URACIL,G4_DNA_ADENOSINE,G4_DNA_GUANOSINE,G4_DNA_CYTIDINE,G4_DNA_URIDINE,G4_DNA_METHYLURIDINE,G4_DNA_MONOPHOSPHATE,G4_DNA_A,G4_DNA_G,G4_DNA_C,G4_DNA_U,G4_DNA_MU]
FEATURE [App::DocumentObjectGroupPython] G4Materials  # scripted group (container) (typed FeaturePython)
  Group = -> [NIST,Element,HEP,Space,BioChemical]
  version = 1
FEATURE [App::DocumentObjectGroupPython] Geant4  # scripted group (container) (typed FeaturePython)
  Group = -> [G4Isotopes,G4Elements,G4Materials]
FEATURE [Part::FeaturePython] GDMLBox_WorldBox  # WARN: FeaturePython — macro-defined, semantics opaque (R4)
  lunit = 2
  material = 8
  x = 114.01
  y = 147.706
  z = 147.706
FEATURE [Part::FeaturePython] GDMLBox_Box  # WARN: FeaturePython — macro-defined, semantics opaque (R4)
  Placement = pos=(0,0,37.85) rot=(0,0,1;0rad)
  lunit = 2
  material = 1
  x = 27.8
  y = 27.8
  z = 8
FEATURE [Part::FeaturePython] GDMLBox_Box003  # WARN: FeaturePython — macro-defined, semantics opaque (R4)
  Placement = pos=(-11.99,-11.99,5) rot=(0,0,1;0rad)
  lunit = 2
  material = 0
  x = 3.22
  y = 3.22
  z = 2
FEATURE [Part::FeaturePython] Array  label="Child_Array"  # Draft array (typed FeaturePython)
  AlwaysSyncPlacement = false
  Angle = 360
  ArrayType = 0
  Axis = (0,0,1)
  Base = -> GDMLBox_Box003
  Center = (0,0,0)
  Count = 64
  ExpandArray = false
  Fuse = false
  IntervalAxis = (0,0,0)
  IntervalX = (3.4,0,0)
  IntervalY = (0,3.4,0)
  IntervalZ = (0,0,100)
  NumberCircles = 3
  NumberPolar = 5
  NumberX = 8
  NumberY = 8
  NumberZ = 1
  Placement = pos=(0,0,37.85) rot=(0,0,1;0rad)
  PlacementList = 64 placements: [(-11.99,-11.99,5),(-11.99,-8.59,5),(-11.99,-5.19,5),(-11.99,-1.79,5),(-11.99,1.61,5),(-11.99,5.01,5),(-11.99,8.41,5),(-11.99,11.81,5),(-8.59,-11.99,5),(-8.59,-8.59,5),(-8.59,-5.19,5),(-8.59,-1.79,5),(-8.59,1.61,5),(-8.59,5.01,5),(-8.59,8.41,5),(-8.59,11.81,5),(-5.19,-11.99,5),(-5.19,-8.59,5),(-5.19,-5.19,5),(-5.19,-1.79,5),(-5.19,1.61,5),(-5.19,5.01,5),(-5.19,8.41,5),(-5.19,11.81,5),+40 more]
  RadialDistance = 50
  ScaleList = (64) [(1,1,1),(1,1,1),(1,1,1),(1,1,1),(1,1,1),(1,1,1),(1,1,1),(1,1,1),(1,1,1),(1,1,1),(1,1,1),(1,1,1),(1,1,1),(1,1,1),(1,1,1),(1,1,1),(1,1,1),(1,1,1),+46 more]
  Symmetry = 1
  TangentialDistance = 25
FEATURE [App::DocumentObjectGroupPython] G4_Pyrex_Glass001  label="G4_Pyrex_Glass : 1.000"  # scripted group (container) (typed FeaturePython)
  n = 1
FEATURE [App::DocumentObjectGroupPython] Glass  # scripted group (container) (typed FeaturePython)
  Dunit = g/cm3
  Dvalue = 1.032
  Group = -> [G4_Pyrex_Glass001]
  RINDEX = RINDEXLAR
  conduct = 2
  density = 1
  expand = 3
  name = Glass
  specific = 4
FEATURE [App::DocumentObjectGroupPython] G4_CESIUM_IODIDE  label="G4_CESIUM_IODIDE : 1.000"  # scripted group (container) (typed FeaturePython)
  n = 1
FEATURE [App::DocumentObjectGroupPython] LYSO  # scripted group (container) (typed FeaturePython)
  ABSLENGTH = ABSLENGTHLAR
  Dunit = g/cm3
  Dvalue = 7.1
  FASTCOMPONENT = SCINTLAR
  FASTTIMECONSTANT = FTC
  Group = -> [G4_CESIUM_IODIDE]
  RAYLEIGH = RAYLEIGHLAR
  REEMISSIONPROB = SCINTLAR
  RESOLUTIONSCALE = RS
  RINDEX = RINDEXLAR
  SCINTILLATIONYIELD = SY
  SLOWCOMPONENT = SCINTLAR
  SLOWTIMECONSTANT = STC
  YIELDRATIO = YR
  conduct = 2
  density = 1
  expand = 3
  name = LYSO
  specific = 4
FEATURE [App::DocumentObjectGroupPython] Materials  # scripted group (container) (typed FeaturePython)
  Group = -> [Air,Geant4,Glass,LYSO]
FEATURE [Part::FeaturePython] Array001  label="Parent_Array"  # Draft array (typed FeaturePython)
  AlwaysSyncPlacement = false
  Angle = 360
  ArrayType = 1
  Axis = (0,1,0)
  Base = -> Array
  Center = (0,0,0)
  Count = 8
  ExpandArray = false
  Fuse = false
  IntervalAxis = (0,0,0)
  IntervalX = (50,0,0)
  IntervalY = (0,50,0)
  IntervalZ = (0,0,50)
  NumberCircles = 3
  NumberPolar = 8
  NumberX = 2
  NumberY = 2
  NumberZ = 1
  PlacementList = 8 placements: [(0,0,37.85),(26.764,0,26.764),(37.85,0,7.10543e-15),(26.764,0,-26.764),(4.63529e-15,0,-37.85),(-26.764,0,-26.764),(-37.85,0,-7.10543e-15),(-26.764,0,26.764)]
  RadialDistance = 50
  ScaleList = (8) [(1,1,1),(1,1,1),(1,1,1),(1,1,1),(1,1,1),(1,1,1),(1,1,1),(1,1,1)]
  Symmetry = 1
  TangentialDistance = 25
FEATURE [App::Part] Part
  Group = -> [GDMLBox_Box003,Array,Array001]
  Origin = -> Origin003
FEATURE [Part::FeaturePython] Array002  # Draft array (typed FeaturePython)
  AlwaysSyncPlacement = false
  Angle = 360
  ArrayType = 1
  Axis = (0,1,0)
  Base = -> GDMLBox_Box
  Center = (0,0,0)
  Count = 8
  ExpandArray = false
  Fuse = false
  IntervalAxis = (0,0,0)
  IntervalX = (50,0,0)
  IntervalY = (0,50,0)
  IntervalZ = (0,0,50)
  NumberCircles = 3
  NumberPolar = 8
  NumberX = 2
  NumberY = 2
  NumberZ = 1
  PlacementList = 8 placements: [(0,0,37.85),(26.764,0,26.764),(37.85,0,7.10543e-15),(26.764,0,-26.764),(4.63529e-15,0,-37.85),(-26.764,0,-26.764),(-37.85,0,-7.10543e-15),(-26.764,0,26.764)]
  RadialDistance = 50
  ScaleList = (8) [(1,1,1),(1,1,1),(1,1,1),(1,1,1),(1,1,1),(1,1,1),(1,1,1),(1,1,1)]
  Symmetry = 1
  TangentialDistance = 25
FEATURE [App::Part] Part001
  Group = -> [GDMLBox_Box,Array002]
  Origin = -> Origin002
  SkinSurface = 0
FEATURE [Part::FeaturePython] GDMLSphere_Sphere  # WARN: FeaturePython — macro-defined, semantics opaque (R4)
  aunit = 1
  deltaphi = 360
  deltatheta = 180
  lunit = 2
  material = 164
  rmax = 5
  rmin = 0
  startphi = 0
  starttheta = 0
FEATURE [App::Part] LV_Sphere
  Group = -> [GDMLSphere_Sphere]
  Origin = -> Origin004
FEATURE [App::Part] worldVOL
  Group = -> [GDMLBox_WorldBox,Part001,Part,LV_Sphere]
  Origin = -> Origin
FEATURE [App::FeaturePython] ScintWrap1  # WARN: FeaturePython — macro-defined, semantics opaque (R4)
  PV1 = Part001
  PV2 = LV_Sphere
  Surface = ScintWrap
